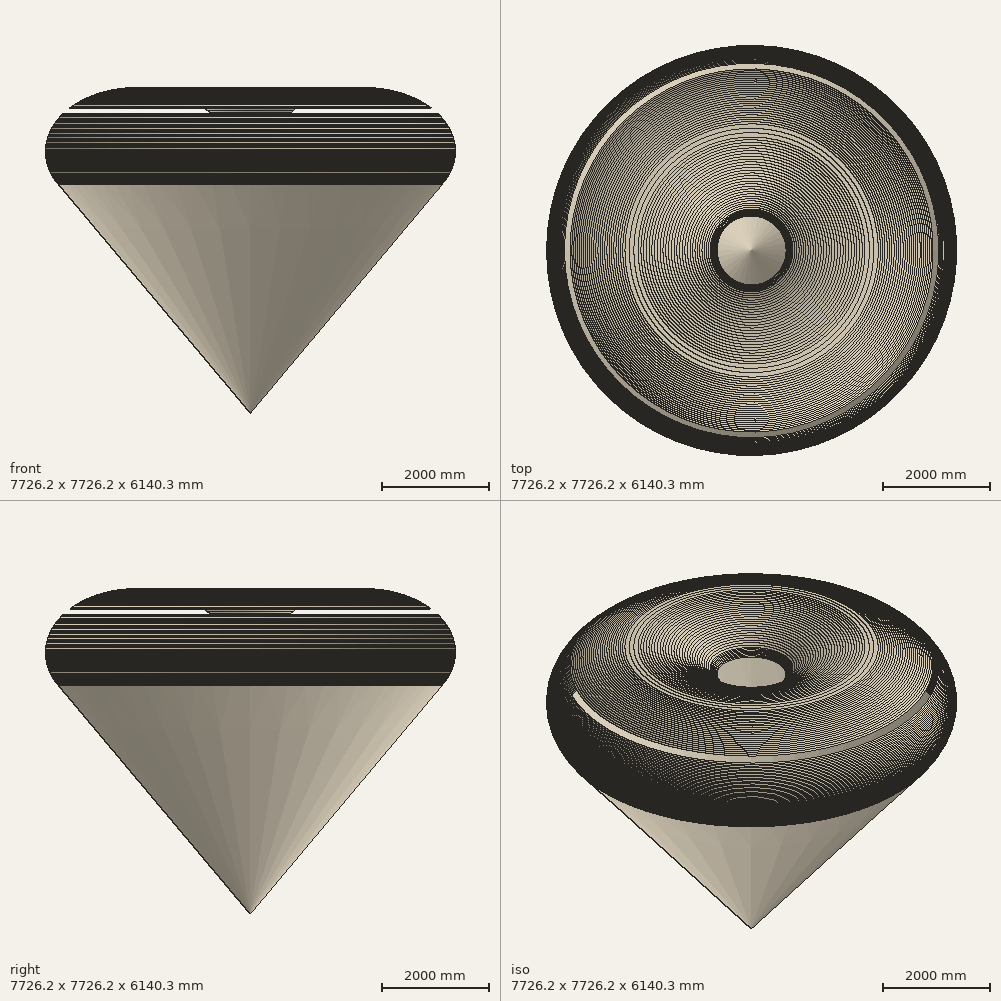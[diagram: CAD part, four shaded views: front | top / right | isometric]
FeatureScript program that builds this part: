
annotation { "Feature Type Name" : "Feature", "Feature Type Description" : "" }
export const myFeature = defineFeature(function(context is Context, id is Id, definition is map)
    precondition{}
    {
        {
            var Q0;
            Q0=qCreatedBy(makeId("Front.planeOp"),FACE);
            var sketch = newSketch(context, id + "F0", { "sketchPlane" : qUnion([Q0])});
            skCircle(sketch, "E0", {"center": v(-6064.54, 1467.13) * mm, "radius": 655.98 * mm});
            skLineSegment(sketch, "E1", {"start": v(-3070, -4796.93) * mm, "end": v(-3002.74, -4740.49) * mm});
            skLineSegment(sketch, "E2", {"start": v(-5930.64, -5948.92) * mm, "end": v(-6060.41, -6057.82) * mm});
            skLineSegment(sketch, "E3", {"start": v(-3096.96, -4796.05) * mm, "end": v(-3134.07, -4768.85) * mm});
            skLineSegment(sketch, "E4", {"start": v(-3134.07, -4768.85) * mm, "end": v(-3335.22, -4786.8) * mm});
            skLineSegment(sketch, "E5", {"start": v(-3112.53, -4828.64) * mm, "end": v(-3070, -4796.93) * mm});
            skLineSegment(sketch, "E6", {"start": v(-3066.53, -4801.07) * mm, "end": v(-3109.32, -4834.33) * mm});
            skLineSegment(sketch, "E7", {"start": v(-3109.32, -4834.33) * mm, "end": v(-3122.09, -4880.14) * mm});
            skLineSegment(sketch, "E8", {"start": v(-3074.34, -4791.79) * mm, "end": v(-3116.78, -4823.52) * mm});
            skLineSegment(sketch, "E9", {"start": v(-3116.78, -4823.52) * mm, "end": v(-3165.41, -4828.64) * mm});
            skLineSegment(sketch, "E10", {"start": v(-3112.53, -4828.64) * mm, "end": v(-3155.06, -4860.36) * mm});
            skLineSegment(sketch, "E11", {"start": v(-3070, -4796.93) * mm, "end": v(-1762.35, -4796.93) * mm});
            skLineSegment(sketch, "E12", {"start": v(-2683.52, -4505.2) * mm, "end": v(-2144.54, -4505.2) * mm});
            skLineSegment(sketch, "E13", {"start": v(-2144.54, -4505.2) * mm, "end": v(-2144.54, -4796.93) * mm});
            skLineSegment(sketch, "E14", {"start": v(-2144.54, -4796.93) * mm, "end": v(-2683.52, -4796.93) * mm});
            skLineSegment(sketch, "E15", {"start": v(-2683.52, -4796.93) * mm, "end": v(-2683.52, -4505.2) * mm});
            skLineSegment(sketch, "E16", {"start": v(-2683.52, -4651.07) * mm, "end": v(-2144.54, -4651.07) * mm});
            skLineSegment(sketch, "E17", {"start": v(-5676.95, -4745.2) * mm, "end": v(-5902.44, -4455.47) * mm});
            skLineSegment(sketch, "E18", {"start": v(-5755.47, -4796.53) * mm, "end": v(-5992.33, -4535.27) * mm});
            skLineSegment(sketch, "E19", {"start": v(-2557.41, -4806.02) * mm, "end": v(-2584.41, -4759.86) * mm});
            skLineSegment(sketch, "E20", {"start": v(-2584.41, -4759.86) * mm, "end": v(-2612.27, -4714.26) * mm});
            skLineSegment(sketch, "E21", {"start": v(-2612.27, -4714.26) * mm, "end": v(-2640.96, -4669.21) * mm});
            skLineSegment(sketch, "E22", {"start": v(-2640.96, -4669.21) * mm, "end": v(-2670.47, -4624.74) * mm});
            skLineSegment(sketch, "E23", {"start": v(-2670.47, -4624.74) * mm, "end": v(-2700.77, -4580.85) * mm});
            skLineSegment(sketch, "E24", {"start": v(-2700.77, -4580.85) * mm, "end": v(-2731.85, -4537.55) * mm});
            skLineSegment(sketch, "E25", {"start": v(-2731.85, -4537.55) * mm, "end": v(-2763.68, -4494.86) * mm});
            skLineSegment(sketch, "E26", {"start": v(-2763.68, -4494.86) * mm, "end": v(-2796.25, -4452.78) * mm});
            skLineSegment(sketch, "E27", {"start": v(-2796.25, -4452.78) * mm, "end": v(-2829.53, -4411.33) * mm});
            skLineSegment(sketch, "E28", {"start": v(-2829.53, -4411.33) * mm, "end": v(-2863.5, -4370.5) * mm});
            skLineSegment(sketch, "E29", {"start": v(-2863.5, -4370.5) * mm, "end": v(-2933.46, -4290.78) * mm});
            skLineSegment(sketch, "E30", {"start": v(-2933.46, -4290.78) * mm, "end": v(-3005.97, -4213.68) * mm});
            skLineSegment(sketch, "E31", {"start": v(-3005.97, -4213.68) * mm, "end": v(-3080.85, -4139.27) * mm});
            skLineSegment(sketch, "E32", {"start": v(-3080.85, -4139.27) * mm, "end": v(-3157.98, -4067.6) * mm});
            skLineSegment(sketch, "E33", {"start": v(-3157.98, -4067.6) * mm, "end": v(-3237.2, -3998.74) * mm});
            skLineSegment(sketch, "E34", {"start": v(-3237.2, -3998.74) * mm, "end": v(-3318.34, -3932.72) * mm});
            skLineSegment(sketch, "E35", {"start": v(-3318.34, -3932.72) * mm, "end": v(-3401.29, -3869.58) * mm});
            skLineSegment(sketch, "E36", {"start": v(-3401.29, -3869.58) * mm, "end": v(-3485.88, -3809.38) * mm});
            skLineSegment(sketch, "E37", {"start": v(-3485.88, -3809.38) * mm, "end": v(-3571.98, -3752.14) * mm});
            skLineSegment(sketch, "E38", {"start": v(-3571.98, -3752.14) * mm, "end": v(-3659.44, -3697.9) * mm});
            skLineSegment(sketch, "E39", {"start": v(-3659.44, -3697.9) * mm, "end": v(-3748.14, -3646.7) * mm});
            skLineSegment(sketch, "E40", {"start": v(-3748.14, -3646.7) * mm, "end": v(-3837.94, -3598.55) * mm});
            skLineSegment(sketch, "E41", {"start": v(-3837.94, -3598.55) * mm, "end": v(-3928.7, -3553.47) * mm});
            skLineSegment(sketch, "E42", {"start": v(-3928.7, -3553.47) * mm, "end": v(-4020.28, -3511.48) * mm});
            skLineSegment(sketch, "E43", {"start": v(-4020.28, -3511.48) * mm, "end": v(-4112.57, -3472.6) * mm});
            skLineSegment(sketch, "E44", {"start": v(-4112.57, -3472.6) * mm, "end": v(-4205.43, -3436.84) * mm});
            skLineSegment(sketch, "E45", {"start": v(-4205.43, -3436.84) * mm, "end": v(-4298.75, -3404.2) * mm});
            skLineSegment(sketch, "E46", {"start": v(-4298.75, -3404.2) * mm, "end": v(-4392.4, -3374.7) * mm});
            skLineSegment(sketch, "E47", {"start": v(-4392.4, -3374.7) * mm, "end": v(-4486.26, -3348.33) * mm});
            skLineSegment(sketch, "E48", {"start": v(-4486.26, -3348.33) * mm, "end": v(-4580.2, -3325.08) * mm});
            skLineSegment(sketch, "E49", {"start": v(-4580.2, -3325.08) * mm, "end": v(-4674.13, -3304.96) * mm});
            skLineSegment(sketch, "E50", {"start": v(-4674.13, -3304.96) * mm, "end": v(-4767.9, -3287.96) * mm});
            skLineSegment(sketch, "E51", {"start": v(-4767.9, -3287.96) * mm, "end": v(-4861.44, -3274.06) * mm});
            skLineSegment(sketch, "E52", {"start": v(-4861.44, -3274.06) * mm, "end": v(-4954.6, -3263.25) * mm});
            skLineSegment(sketch, "E53", {"start": v(-4954.6, -3263.25) * mm, "end": v(-5047.31, -3255.52) * mm});
            skLineSegment(sketch, "E54", {"start": v(-5047.31, -3255.52) * mm, "end": v(-5139.44, -3250.85) * mm});
            skLineSegment(sketch, "E55", {"start": v(-5139.44, -3250.85) * mm, "end": v(-5230.89, -3249.21) * mm});
            skLineSegment(sketch, "E56", {"start": v(-5230.89, -3249.21) * mm, "end": v(-5321.56, -3250.59) * mm});
            skLineSegment(sketch, "E57", {"start": v(-5321.56, -3250.59) * mm, "end": v(-5411.35, -3254.95) * mm});
            skLineSegment(sketch, "E58", {"start": v(-5411.35, -3254.95) * mm, "end": v(-5500.17, -3262.27) * mm});
            skLineSegment(sketch, "E59", {"start": v(-5500.17, -3262.27) * mm, "end": v(-5587.91, -3272.52) * mm});
            skLineSegment(sketch, "E60", {"start": v(-5587.91, -3272.52) * mm, "end": v(-5674.5, -3285.66) * mm});
            skLineSegment(sketch, "E61", {"start": v(-5674.5, -3285.66) * mm, "end": v(-5717.32, -3293.3) * mm});
            skLineSegment(sketch, "E62", {"start": v(-5717.32, -3293.3) * mm, "end": v(-5759.82, -3301.67) * mm});
            skLineSegment(sketch, "E63", {"start": v(-5759.82, -3301.67) * mm, "end": v(-5801.98, -3310.73) * mm});
            skLineSegment(sketch, "E64", {"start": v(-5801.98, -3310.73) * mm, "end": v(-5843.8, -3320.5) * mm});
            skLineSegment(sketch, "E65", {"start": v(-5843.8, -3320.5) * mm, "end": v(-5885.26, -3330.95) * mm});
            skLineSegment(sketch, "E66", {"start": v(-5885.26, -3330.95) * mm, "end": v(-5926.35, -3342.1) * mm});
            skLineSegment(sketch, "E67", {"start": v(-5926.35, -3342.1) * mm, "end": v(-5967.06, -3353.94) * mm});
            skLineSegment(sketch, "E68", {"start": v(-5967.06, -3353.94) * mm, "end": v(-6007.38, -3366.46) * mm});
            skLineSegment(sketch, "E69", {"start": v(-6007.38, -3366.46) * mm, "end": v(-6047.3, -3379.65) * mm});
            skLineSegment(sketch, "E70", {"start": v(-6047.3, -3379.65) * mm, "end": v(-6086.82, -3393.52) * mm});
            skLineSegment(sketch, "E71", {"start": v(-6086.82, -3393.52) * mm, "end": v(-6125.91, -3408.05) * mm});
            skLineSegment(sketch, "E72", {"start": v(-6125.91, -3408.05) * mm, "end": v(-6164.58, -3423.24) * mm});
            skLineSegment(sketch, "E73", {"start": v(-6164.58, -3423.24) * mm, "end": v(-6202.8, -3439.08) * mm});
            skLineSegment(sketch, "E74", {"start": v(-6202.8, -3439.08) * mm, "end": v(-6240.57, -3455.57) * mm});
            skLineSegment(sketch, "E75", {"start": v(-6240.57, -3455.57) * mm, "end": v(-6277.89, -3472.7) * mm});
            skLineSegment(sketch, "E76", {"start": v(-6277.89, -3472.7) * mm, "end": v(-6314.74, -3490.46) * mm});
            skLineSegment(sketch, "E77", {"start": v(-6314.74, -3490.46) * mm, "end": v(-6351.1, -3508.86) * mm});
            skLineSegment(sketch, "E78", {"start": v(-6351.1, -3508.86) * mm, "end": v(-6387, -3527.88) * mm});
            skLineSegment(sketch, "E79", {"start": v(-6387, -3527.88) * mm, "end": v(-6422.38, -3547.52) * mm});
            skLineSegment(sketch, "E80", {"start": v(-6422.38, -3547.52) * mm, "end": v(-6457.26, -3567.77) * mm});
            skLineSegment(sketch, "E81", {"start": v(-6457.26, -3567.77) * mm, "end": v(-6491.63, -3588.62) * mm});
            skLineSegment(sketch, "E82", {"start": v(-6491.63, -3588.62) * mm, "end": v(-6525.48, -3610.07) * mm});
            skLineSegment(sketch, "E83", {"start": v(-6525.48, -3610.07) * mm, "end": v(-6558.8, -3632.11) * mm});
            skLineSegment(sketch, "E84", {"start": v(-6558.8, -3632.11) * mm, "end": v(-6591.58, -3654.74) * mm});
            skLineSegment(sketch, "E85", {"start": v(-6591.58, -3654.74) * mm, "end": v(-6623.81, -3677.95) * mm});
            skLineSegment(sketch, "E86", {"start": v(-6623.81, -3677.95) * mm, "end": v(-6655.5, -3701.73) * mm});
            skLineSegment(sketch, "E87", {"start": v(-6655.5, -3701.73) * mm, "end": v(-6686.6, -3726.07) * mm});
            skLineSegment(sketch, "E88", {"start": v(-6686.6, -3726.07) * mm, "end": v(-6717.15, -3750.97) * mm});
            skLineSegment(sketch, "E89", {"start": v(-6717.15, -3750.97) * mm, "end": v(-6747.12, -3776.42) * mm});
            skLineSegment(sketch, "E90", {"start": v(-6747.12, -3776.42) * mm, "end": v(-6776.5, -3802.42) * mm});
            skLineSegment(sketch, "E91", {"start": v(-6776.5, -3802.42) * mm, "end": v(-6805.29, -3828.96) * mm});
            skLineSegment(sketch, "E92", {"start": v(-6805.29, -3828.96) * mm, "end": v(-6833.47, -3856.02) * mm});
            skLineSegment(sketch, "E93", {"start": v(-6833.47, -3856.02) * mm, "end": v(-6861.05, -3883.6) * mm});
            skLineSegment(sketch, "E94", {"start": v(-6861.05, -3883.6) * mm, "end": v(-6888.01, -3911.71) * mm});
            skLineSegment(sketch, "E95", {"start": v(-6888.01, -3911.71) * mm, "end": v(-6914.35, -3940.33) * mm});
            skLineSegment(sketch, "E96", {"start": v(-6914.35, -3940.33) * mm, "end": v(-6940.06, -3969.44) * mm});
            skLineSegment(sketch, "E97", {"start": v(-6940.06, -3969.44) * mm, "end": v(-6965.14, -3999.05) * mm});
            skLineSegment(sketch, "E98", {"start": v(-6965.14, -3999.05) * mm, "end": v(-6989.57, -4029.15) * mm});
            skLineSegment(sketch, "E99", {"start": v(-6989.57, -4029.15) * mm, "end": v(-7013.36, -4059.73) * mm});
            skLineSegment(sketch, "E100", {"start": v(-7013.36, -4059.73) * mm, "end": v(-7036.49, -4090.78) * mm});
            skLineSegment(sketch, "E101", {"start": v(-7036.49, -4090.78) * mm, "end": v(-7058.95, -4122.3) * mm});
            skLineSegment(sketch, "E102", {"start": v(-7058.95, -4122.3) * mm, "end": v(-7080.75, -4154.26) * mm});
            skLineSegment(sketch, "E103", {"start": v(-7080.75, -4154.26) * mm, "end": v(-7101.88, -4186.69) * mm});
            skLineSegment(sketch, "E104", {"start": v(-7101.88, -4186.69) * mm, "end": v(-7122.33, -4219.56) * mm});
            skLineSegment(sketch, "E105", {"start": v(-7122.33, -4219.56) * mm, "end": v(-7142.1, -4252.86) * mm});
            skLineSegment(sketch, "E106", {"start": v(-7142.1, -4252.86) * mm, "end": v(-7161.16, -4286.6) * mm});
            skLineSegment(sketch, "E107", {"start": v(-7161.16, -4286.6) * mm, "end": v(-7179.54, -4320.74) * mm});
            skLineSegment(sketch, "E108", {"start": v(-7179.54, -4320.74) * mm, "end": v(-7197.22, -4355.31) * mm});
            skLineSegment(sketch, "E109", {"start": v(-7197.22, -4355.31) * mm, "end": v(-7214.18, -4390.28) * mm});
            skLineSegment(sketch, "E110", {"start": v(-7214.18, -4390.28) * mm, "end": v(-7230.44, -4425.65) * mm});
            skLineSegment(sketch, "E111", {"start": v(-7230.44, -4425.65) * mm, "end": v(-7245.98, -4461.42) * mm});
            skLineSegment(sketch, "E112", {"start": v(-7245.98, -4461.42) * mm, "end": v(-7260.8, -4497.56) * mm});
            skLineSegment(sketch, "E113", {"start": v(-7260.8, -4497.56) * mm, "end": v(-7274.9, -4534.09) * mm});
            skLineSegment(sketch, "E114", {"start": v(-7274.9, -4534.09) * mm, "end": v(-7288.26, -4570.98) * mm});
            skLineSegment(sketch, "E115", {"start": v(-7288.26, -4570.98) * mm, "end": v(-7300.88, -4608.23) * mm});
            skLineSegment(sketch, "E116", {"start": v(-7300.88, -4608.23) * mm, "end": v(-7312.77, -4645.84) * mm});
            skLineSegment(sketch, "E117", {"start": v(-7312.77, -4645.84) * mm, "end": v(-7323.92, -4683.8) * mm});
            skLineSegment(sketch, "E118", {"start": v(-7323.92, -4683.8) * mm, "end": v(-7334.31, -4722.09) * mm});
            skLineSegment(sketch, "E119", {"start": v(-7334.31, -4722.09) * mm, "end": v(-7343.96, -4760.72) * mm});
            skLineSegment(sketch, "E120", {"start": v(-7343.96, -4760.72) * mm, "end": v(-7352.85, -4799.67) * mm});
            skLineSegment(sketch, "E121", {"start": v(-7352.85, -4799.67) * mm, "end": v(-7360.98, -4838.93) * mm});
            skLineSegment(sketch, "E122", {"start": v(-7360.98, -4838.93) * mm, "end": v(-7368.35, -4878.51) * mm});
            skLineSegment(sketch, "E123", {"start": v(-7368.35, -4878.51) * mm, "end": v(-7374.95, -4918.4) * mm});
            skLineSegment(sketch, "E124", {"start": v(-7374.95, -4918.4) * mm, "end": v(-7380.78, -4958.57) * mm});
            skLineSegment(sketch, "E125", {"start": v(-7380.78, -4958.57) * mm, "end": v(-7385.84, -4999.04) * mm});
            skLineSegment(sketch, "E126", {"start": v(-7385.84, -4999.04) * mm, "end": v(-7390.12, -5039.79) * mm});
            skLineSegment(sketch, "E127", {"start": v(-7390.12, -5039.79) * mm, "end": v(-7393.63, -5080.8) * mm});
            skLineSegment(sketch, "E128", {"start": v(-7393.63, -5080.8) * mm, "end": v(-7396.35, -5122.1) * mm});
            skLineSegment(sketch, "E129", {"start": v(-7396.35, -5122.1) * mm, "end": v(-7398.29, -5163.65) * mm});
            skLineSegment(sketch, "E130", {"start": v(-7398.29, -5163.65) * mm, "end": v(-7399.44, -5205.45) * mm});
            skLineSegment(sketch, "E131", {"start": v(-7399.44, -5205.45) * mm, "end": v(-7399.8, -5247.5) * mm});
            skLineSegment(sketch, "E132", {"start": v(-7399.8, -5247.5) * mm, "end": v(-7399.37, -5289.8) * mm});
            skLineSegment(sketch, "E133", {"start": v(-7399.37, -5289.8) * mm, "end": v(-7398.15, -5332.32) * mm});
            skLineSegment(sketch, "E134", {"start": v(-7398.15, -5332.32) * mm, "end": v(-7396.13, -5375.06) * mm});
            skLineSegment(sketch, "E135", {"start": v(-7396.13, -5375.06) * mm, "end": v(-7393.3, -5418.03) * mm});
            skLineSegment(sketch, "E136", {"start": v(-7393.3, -5418.03) * mm, "end": v(-7389.7, -5461.21) * mm});
            skLineSegment(sketch, "E137", {"start": v(-7389.7, -5461.21) * mm, "end": v(-7385.27, -5504.6) * mm});
            skLineSegment(sketch, "E138", {"start": v(-7385.27, -5504.6) * mm, "end": v(-7380.05, -5548.2) * mm});
            skLineSegment(sketch, "E139", {"start": v(-7380.05, -5548.2) * mm, "end": v(-7367.19, -5635.94) * mm});
            skLineSegment(sketch, "E140", {"start": v(-7367.19, -5635.94) * mm, "end": v(-7351.1, -5724.42) * mm});
            skLineSegment(sketch, "E141", {"start": v(-7351.1, -5724.42) * mm, "end": v(-7331.77, -5813.57) * mm});
            skLineSegment(sketch, "E142", {"start": v(-7331.77, -5813.57) * mm, "end": v(-7309.2, -5903.35) * mm});
            skLineSegment(sketch, "E143", {"start": v(-7309.2, -5903.35) * mm, "end": v(-7283.37, -5993.7) * mm});
            skLineSegment(sketch, "E144", {"start": v(-7283.37, -5993.7) * mm, "end": v(-7254.3, -6084.6) * mm});
            skLineSegment(sketch, "E145", {"start": v(-7254.3, -6084.6) * mm, "end": v(-7221.98, -6176) * mm});
            skLineSegment(sketch, "E146", {"start": v(-7221.98, -6176) * mm, "end": v(-7186.4, -6267.84) * mm});
            skLineSegment(sketch, "E147", {"start": v(-7186.4, -6267.84) * mm, "end": v(-7147.58, -6360.1) * mm});
            skLineSegment(sketch, "E148", {"start": v(-7147.58, -6360.1) * mm, "end": v(-7105.51, -6452.72) * mm});
            skLineSegment(sketch, "E149", {"start": v(-7105.51, -6452.72) * mm, "end": v(-7060.21, -6545.7) * mm});
            skLineSegment(sketch, "E150", {"start": v(-7060.21, -6545.7) * mm, "end": v(-7011.69, -6638.97) * mm});
            skLineSegment(sketch, "E151", {"start": v(-7011.69, -6638.97) * mm, "end": v(-6959.95, -6732.52) * mm});
            skLineSegment(sketch, "E152", {"start": v(-6959.95, -6732.52) * mm, "end": v(-6905, -6826.3) * mm});
            skLineSegment(sketch, "E153", {"start": v(-6905, -6826.3) * mm, "end": v(-6846.88, -6920.32) * mm});
            skLineSegment(sketch, "E154", {"start": v(-6846.88, -6920.32) * mm, "end": v(-6785.58, -7014.52) * mm});
            skLineSegment(sketch, "E155", {"start": v(-6785.58, -7014.52) * mm, "end": v(-6721.12, -7108.88) * mm});
            skLineSegment(sketch, "E156", {"start": v(-6721.12, -7108.88) * mm, "end": v(-6653.54, -7203.4) * mm});
            skLineSegment(sketch, "E157", {"start": v(-6653.54, -7203.4) * mm, "end": v(-6582.85, -7298.04) * mm});
            skLineSegment(sketch, "E158", {"start": v(-6582.85, -7298.04) * mm, "end": v(-6509.08, -7392.8) * mm});
            skLineSegment(sketch, "E159", {"start": v(-6509.08, -7392.8) * mm, "end": v(-6432.24, -7487.66) * mm});
            skLineSegment(sketch, "E160", {"start": v(-6432.24, -7487.66) * mm, "end": v(-6352.38, -7582.62) * mm});
            skLineSegment(sketch, "E161", {"start": v(-6352.38, -7582.62) * mm, "end": v(-6183.7, -7772.78) * mm});
            skLineSegment(sketch, "E162", {"start": v(-6183.7, -7772.78) * mm, "end": v(-6003.28, -7963.27) * mm});
            skLineSegment(sketch, "E163", {"start": v(-6003.28, -7963.27) * mm, "end": v(-5811.43, -8154.13) * mm});
            skLineSegment(sketch, "E164", {"start": v(-5811.43, -8154.13) * mm, "end": v(-5608.46, -8345.43) * mm});
            skLineSegment(sketch, "E165", {"start": v(-5608.46, -8345.43) * mm, "end": v(-5394.75, -8537.32) * mm});
            skLineSegment(sketch, "E166", {"start": v(-5394.75, -8537.32) * mm, "end": v(-5170.66, -8730) * mm});
            skLineSegment(sketch, "E167", {"start": v(-5170.66, -8730) * mm, "end": v(-4936.62, -8923.7) * mm});
            skLineSegment(sketch, "E168", {"start": v(-4936.62, -8923.7) * mm, "end": v(-4440.49, -9315.6) * mm});
            skLineSegment(sketch, "E169", {"start": v(-4440.49, -9315.6) * mm, "end": v(-3910.27, -9716.36) * mm});
            skLineSegment(sketch, "E170", {"start": v(-3910.27, -9716.36) * mm, "end": v(-2765.64, -10563.66) * mm});
            skLineSegment(sketch, "E171", {"start": v(-3092.98, -4789.79) * mm, "end": v(-3093.29, -4801.97) * mm});
            skLineSegment(sketch, "E172", {"start": v(-3093.29, -4801.97) * mm, "end": v(-3104.06, -4799.16) * mm});
            skLineSegment(sketch, "E173", {"start": v(-3104.06, -4799.16) * mm, "end": v(-3092.98, -4789.79) * mm});
            skCircle(sketch, "E174", {"center": v(-6064.54, 1467.13) * mm, "radius": 755.98 * mm});
            skLineSegment(sketch, "E175", {"start": v(-6318.54, 1625.88) * mm, "end": v(-5810.54, 1625.88) * mm});
            skLineSegment(sketch, "E176", {"start": v(-5810.54, 1625.88) * mm, "end": v(-5810.54, 1308.38) * mm});
            skLineSegment(sketch, "E177", {"start": v(-5810.54, 1308.38) * mm, "end": v(-6318.54, 1308.38) * mm});
            skLineSegment(sketch, "E178", {"start": v(-6318.54, 1308.38) * mm, "end": v(-6318.54, 1625.88) * mm});
            skLineSegment(sketch, "E179", {"start": v(-6318.54, 1546.5) * mm, "end": v(-5810.54, 1546.5) * mm});
            skLineSegment(sketch, "E180", {"start": v(-6318.54, 1387.75) * mm, "end": v(-5810.54, 1387.75) * mm});
            skLineSegment(sketch, "E181", {"start": v(-5310.22, 1517.13) * mm, "end": v(-6818.86, 1517.13) * mm});
            skLineSegment(sketch, "E182", {"start": v(-5310.22, 1417.13) * mm, "end": v(-6818.86, 1417.13) * mm});
            skLineSegment(sketch, "E183", {"start": v(-6022.98, -5953.64) * mm, "end": v(-2397.59, -10274.2) * mm});
            skLineSegment(sketch, "E184", {"start": v(-2397.59, -5504) * mm, "end": v(-2397.59, -10274.2) * mm});
            skLineSegment(sketch, "E185", {"start": v(-3047.01, -4730.04) * mm, "end": v(-2397.59, -5504) * mm});
            skLineSegment(sketch, "E186", {"start": v(-5818.02, -4534.01) * mm, "end": v(-5785.77, -4509.6) * mm});
            skLineSegment(sketch, "E187", {"start": v(-5785.77, -4509.6) * mm, "end": v(-5752.56, -4485.8) * mm});
            skLineSegment(sketch, "E188", {"start": v(-5752.56, -4485.8) * mm, "end": v(-5718.42, -4462.66) * mm});
            skLineSegment(sketch, "E189", {"start": v(-5718.42, -4462.66) * mm, "end": v(-5683.4, -4440.2) * mm});
            skLineSegment(sketch, "E190", {"start": v(-5683.4, -4440.2) * mm, "end": v(-5647.54, -4418.42) * mm});
            skLineSegment(sketch, "E191", {"start": v(-5647.54, -4418.42) * mm, "end": v(-5610.89, -4397.38) * mm});
            skLineSegment(sketch, "E192", {"start": v(-5610.89, -4397.38) * mm, "end": v(-5573.47, -4377.08) * mm});
            skLineSegment(sketch, "E193", {"start": v(-5573.47, -4377.08) * mm, "end": v(-5535.35, -4357.54) * mm});
            skLineSegment(sketch, "E194", {"start": v(-5535.35, -4357.54) * mm, "end": v(-5496.58, -4338.78) * mm});
            skLineSegment(sketch, "E195", {"start": v(-5496.58, -4338.78) * mm, "end": v(-5457.18, -4320.82) * mm});
            skLineSegment(sketch, "E196", {"start": v(-5457.18, -4320.82) * mm, "end": v(-5417.23, -4303.66) * mm});
            skLineSegment(sketch, "E197", {"start": v(-5417.23, -4303.66) * mm, "end": v(-5376.76, -4287.33) * mm});
            skLineSegment(sketch, "E198", {"start": v(-5376.76, -4287.33) * mm, "end": v(-5335.84, -4271.82) * mm});
            skLineSegment(sketch, "E199", {"start": v(-5335.84, -4271.82) * mm, "end": v(-5294.5, -4257.15) * mm});
            skLineSegment(sketch, "E200", {"start": v(-5294.5, -4257.15) * mm, "end": v(-5252.8, -4243.33) * mm});
            skLineSegment(sketch, "E201", {"start": v(-5252.8, -4243.33) * mm, "end": v(-5210.8, -4230.35) * mm});
            skLineSegment(sketch, "E202", {"start": v(-5210.8, -4230.35) * mm, "end": v(-5168.52, -4218.21) * mm});
            skLineSegment(sketch, "E203", {"start": v(-5168.52, -4218.21) * mm, "end": v(-5126.04, -4206.93) * mm});
            skLineSegment(sketch, "E204", {"start": v(-5126.04, -4206.93) * mm, "end": v(-5083.4, -4196.49) * mm});
            skLineSegment(sketch, "E205", {"start": v(-5083.4, -4196.49) * mm, "end": v(-5040.66, -4186.9) * mm});
            skLineSegment(sketch, "E206", {"start": v(-5040.66, -4186.9) * mm, "end": v(-4997.84, -4178.13) * mm});
            skLineSegment(sketch, "E207", {"start": v(-4997.84, -4178.13) * mm, "end": v(-4955.01, -4170.2) * mm});
            skLineSegment(sketch, "E208", {"start": v(-4955.01, -4170.2) * mm, "end": v(-4912.21, -4163.08) * mm});
            skLineSegment(sketch, "E209", {"start": v(-4912.21, -4163.08) * mm, "end": v(-4869.48, -4156.78) * mm});
            skLineSegment(sketch, "E210", {"start": v(-4869.48, -4156.78) * mm, "end": v(-4826.87, -4151.27) * mm});
            skLineSegment(sketch, "E211", {"start": v(-4826.87, -4151.27) * mm, "end": v(-4784.4, -4146.55) * mm});
            skLineSegment(sketch, "E212", {"start": v(-4784.4, -4146.55) * mm, "end": v(-4700.1, -4139.4) * mm});
            skLineSegment(sketch, "E213", {"start": v(-4700.1, -4139.4) * mm, "end": v(-4616.88, -4135.23) * mm});
            skLineSegment(sketch, "E214", {"start": v(-4616.88, -4135.23) * mm, "end": v(-4535, -4133.87) * mm});
            skLineSegment(sketch, "E215", {"start": v(-4535, -4133.87) * mm, "end": v(-4484.8, -4134.38) * mm});
            skLineSegment(sketch, "E216", {"start": v(-4484.8, -4134.38) * mm, "end": v(-4434.07, -4135.93) * mm});
            skLineSegment(sketch, "E217", {"start": v(-4434.07, -4135.93) * mm, "end": v(-4382.85, -4138.57) * mm});
            skLineSegment(sketch, "E218", {"start": v(-4382.85, -4138.57) * mm, "end": v(-4331.2, -4142.32) * mm});
            skLineSegment(sketch, "E219", {"start": v(-4331.2, -4142.32) * mm, "end": v(-4279.2, -4147.21) * mm});
            skLineSegment(sketch, "E220", {"start": v(-4279.2, -4147.21) * mm, "end": v(-4226.92, -4153.27) * mm});
            skLineSegment(sketch, "E221", {"start": v(-4226.92, -4153.27) * mm, "end": v(-4174.42, -4160.53) * mm});
            skLineSegment(sketch, "E222", {"start": v(-4174.42, -4160.53) * mm, "end": v(-4121.79, -4169) * mm});
            skLineSegment(sketch, "E223", {"start": v(-4121.79, -4169) * mm, "end": v(-4069.1, -4178.72) * mm});
            skLineSegment(sketch, "E224", {"start": v(-4069.1, -4178.72) * mm, "end": v(-4016.45, -4189.7) * mm});
            skLineSegment(sketch, "E225", {"start": v(-4016.45, -4189.7) * mm, "end": v(-3963.91, -4201.93) * mm});
            skLineSegment(sketch, "E226", {"start": v(-3963.91, -4201.93) * mm, "end": v(-3911.59, -4215.44) * mm});
            skLineSegment(sketch, "E227", {"start": v(-3911.59, -4215.44) * mm, "end": v(-3859.56, -4230.24) * mm});
            skLineSegment(sketch, "E228", {"start": v(-3859.56, -4230.24) * mm, "end": v(-3807.92, -4246.32) * mm});
            skLineSegment(sketch, "E229", {"start": v(-3807.92, -4246.32) * mm, "end": v(-3756.77, -4263.68) * mm});
            skLineSegment(sketch, "E230", {"start": v(-3756.77, -4263.68) * mm, "end": v(-3706.2, -4282.3) * mm});
            skLineSegment(sketch, "E231", {"start": v(-3706.2, -4282.3) * mm, "end": v(-3656.3, -4302.2) * mm});
            skLineSegment(sketch, "E232", {"start": v(-3656.3, -4302.2) * mm, "end": v(-3607.17, -4323.32) * mm});
            skLineSegment(sketch, "E233", {"start": v(-3607.17, -4323.32) * mm, "end": v(-3558.9, -4345.67) * mm});
            skLineSegment(sketch, "E234", {"start": v(-3558.9, -4345.67) * mm, "end": v(-3511.6, -4369.22) * mm});
            skLineSegment(sketch, "E235", {"start": v(-3511.6, -4369.22) * mm, "end": v(-3465.32, -4393.93) * mm});
            skLineSegment(sketch, "E236", {"start": v(-3465.32, -4393.93) * mm, "end": v(-3420.18, -4419.77) * mm});
            skLineSegment(sketch, "E237", {"start": v(-3420.18, -4419.77) * mm, "end": v(-3376.25, -4446.7) * mm});
            skLineSegment(sketch, "E238", {"start": v(-3376.25, -4446.7) * mm, "end": v(-3333.6, -4474.68) * mm});
            skLineSegment(sketch, "E239", {"start": v(-3333.6, -4474.68) * mm, "end": v(-3292.34, -4503.66) * mm});
            skLineSegment(sketch, "E240", {"start": v(-3292.34, -4503.66) * mm, "end": v(-3252.5, -4533.6) * mm});
            skLineSegment(sketch, "E241", {"start": v(-3252.5, -4533.6) * mm, "end": v(-3214.18, -4564.43) * mm});
            skLineSegment(sketch, "E242", {"start": v(-3214.18, -4564.43) * mm, "end": v(-3177.41, -4596.1) * mm});
            skLineSegment(sketch, "E243", {"start": v(-3177.41, -4596.1) * mm, "end": v(-3159.64, -4612.24) * mm});
            skLineSegment(sketch, "E244", {"start": v(-3159.64, -4612.24) * mm, "end": v(-3142.27, -4628.57) * mm});
            skLineSegment(sketch, "E245", {"start": v(-3142.27, -4628.57) * mm, "end": v(-3125.32, -4645.07) * mm});
            skLineSegment(sketch, "E246", {"start": v(-3125.32, -4645.07) * mm, "end": v(-3108.8, -4661.75) * mm});
            skLineSegment(sketch, "E247", {"start": v(-3108.8, -4661.75) * mm, "end": v(-3092.7, -4678.6) * mm});
            skLineSegment(sketch, "E248", {"start": v(-3092.7, -4678.6) * mm, "end": v(-3077.03, -4695.6) * mm});
            skLineSegment(sketch, "E249", {"start": v(-3077.03, -4695.6) * mm, "end": v(-3061.8, -4712.75) * mm});
            skLineSegment(sketch, "E250", {"start": v(-3061.8, -4712.75) * mm, "end": v(-3047.01, -4730.04) * mm});
            skArc(sketch, "E251", {"start": v(-5860.11, -4568.03) * mm, "mid": v(-5880.68, -4585.61) * mm, "end": v(-5900.9, -4603.6) * mm});
            skLineSegment(sketch, "E252", {"start": v(-5860.11, -4568.03) * mm, "end": v(-5818.02, -4534.01) * mm});
            skLineSegment(sketch, "E253", {"start": v(-6022.98, -5953.64) * mm, "end": v(-6038.12, -5935.22) * mm});
            skLineSegment(sketch, "E254", {"start": v(-6038.12, -5935.22) * mm, "end": v(-6052.76, -5916.67) * mm});
            skLineSegment(sketch, "E255", {"start": v(-6052.76, -5916.67) * mm, "end": v(-6066.9, -5897.99) * mm});
            skLineSegment(sketch, "E256", {"start": v(-6066.9, -5897.99) * mm, "end": v(-6080.54, -5879.19) * mm});
            skLineSegment(sketch, "E257", {"start": v(-6080.54, -5879.19) * mm, "end": v(-6093.66, -5860.27) * mm});
            skLineSegment(sketch, "E258", {"start": v(-6093.66, -5860.27) * mm, "end": v(-6106.28, -5841.26) * mm});
            skLineSegment(sketch, "E259", {"start": v(-6106.28, -5841.26) * mm, "end": v(-6118.39, -5822.16) * mm});
            skLineSegment(sketch, "E260", {"start": v(-6118.39, -5822.16) * mm, "end": v(-6129.98, -5802.98) * mm});
            skLineSegment(sketch, "E261", {"start": v(-6129.98, -5802.98) * mm, "end": v(-6141.07, -5783.73) * mm});
            skLineSegment(sketch, "E262", {"start": v(-6141.07, -5783.73) * mm, "end": v(-6151.64, -5764.42) * mm});
            skLineSegment(sketch, "E263", {"start": v(-6151.64, -5764.42) * mm, "end": v(-6161.7, -5745.05) * mm});
            skLineSegment(sketch, "E264", {"start": v(-6161.7, -5745.05) * mm, "end": v(-6171.25, -5725.64) * mm});
            skLineSegment(sketch, "E265", {"start": v(-6171.25, -5725.64) * mm, "end": v(-6180.3, -5706.2) * mm});
            skLineSegment(sketch, "E266", {"start": v(-6180.3, -5706.2) * mm, "end": v(-6188.84, -5686.74) * mm});
            skLineSegment(sketch, "E267", {"start": v(-6188.84, -5686.74) * mm, "end": v(-6196.87, -5667.26) * mm});
            skLineSegment(sketch, "E268", {"start": v(-6196.87, -5667.26) * mm, "end": v(-6204.41, -5647.78) * mm});
            skLineSegment(sketch, "E269", {"start": v(-6204.41, -5647.78) * mm, "end": v(-6211.45, -5628.3) * mm});
            skLineSegment(sketch, "E270", {"start": v(-6211.45, -5628.3) * mm, "end": v(-6218, -5608.83) * mm});
            skLineSegment(sketch, "E271", {"start": v(-6218, -5608.83) * mm, "end": v(-6224.05, -5589.38) * mm});
            skLineSegment(sketch, "E272", {"start": v(-6224.05, -5589.38) * mm, "end": v(-6229.62, -5569.96) * mm});
            skLineSegment(sketch, "E273", {"start": v(-6229.62, -5569.96) * mm, "end": v(-6234.72, -5550.57) * mm});
            skLineSegment(sketch, "E274", {"start": v(-6234.72, -5550.57) * mm, "end": v(-6239.33, -5531.23) * mm});
            skLineSegment(sketch, "E275", {"start": v(-6239.33, -5531.23) * mm, "end": v(-6243.48, -5511.94) * mm});
            skLineSegment(sketch, "E276", {"start": v(-6243.48, -5511.94) * mm, "end": v(-6247.16, -5492.71) * mm});
            skLineSegment(sketch, "E277", {"start": v(-6247.16, -5492.71) * mm, "end": v(-6250.38, -5473.55) * mm});
            skLineSegment(sketch, "E278", {"start": v(-6250.38, -5473.55) * mm, "end": v(-6253.16, -5454.46) * mm});
            skLineSegment(sketch, "E279", {"start": v(-6253.16, -5454.46) * mm, "end": v(-6255.48, -5435.45) * mm});
            skLineSegment(sketch, "E280", {"start": v(-6255.48, -5435.45) * mm, "end": v(-6257.37, -5416.53) * mm});
            skLineSegment(sketch, "E281", {"start": v(-6257.37, -5416.53) * mm, "end": v(-6258.83, -5397.7) * mm});
            skLineSegment(sketch, "E282", {"start": v(-6258.83, -5397.7) * mm, "end": v(-6259.86, -5378.98) * mm});
            skLineSegment(sketch, "E283", {"start": v(-6259.86, -5378.98) * mm, "end": v(-6260.47, -5360.35) * mm});
            skLineSegment(sketch, "E284", {"start": v(-6260.47, -5360.35) * mm, "end": v(-6260.67, -5341.84) * mm});
            skLineSegment(sketch, "E285", {"start": v(-6260.67, -5341.84) * mm, "end": v(-6260.37, -5319.19) * mm});
            skLineSegment(sketch, "E286", {"start": v(-6260.37, -5319.19) * mm, "end": v(-6259.45, -5296.37) * mm});
            skLineSegment(sketch, "E287", {"start": v(-6259.45, -5296.37) * mm, "end": v(-6257.9, -5273.4) * mm});
            skLineSegment(sketch, "E288", {"start": v(-6257.9, -5273.4) * mm, "end": v(-6255.7, -5250.29) * mm});
            skLineSegment(sketch, "E289", {"start": v(-6255.7, -5250.29) * mm, "end": v(-6252.86, -5227.04) * mm});
            skLineSegment(sketch, "E290", {"start": v(-6252.86, -5227.04) * mm, "end": v(-6249.35, -5203.68) * mm});
            skLineSegment(sketch, "E291", {"start": v(-6249.35, -5203.68) * mm, "end": v(-6245.16, -5180.2) * mm});
            skLineSegment(sketch, "E292", {"start": v(-6245.16, -5180.2) * mm, "end": v(-6240.27, -5156.65) * mm});
            skLineSegment(sketch, "E293", {"start": v(-6240.27, -5156.65) * mm, "end": v(-6234.69, -5133) * mm});
            skLineSegment(sketch, "E294", {"start": v(-6234.69, -5133) * mm, "end": v(-6228.4, -5109.3) * mm});
            skLineSegment(sketch, "E295", {"start": v(-6228.4, -5109.3) * mm, "end": v(-6221.38, -5085.53) * mm});
            skLineSegment(sketch, "E296", {"start": v(-6221.38, -5085.53) * mm, "end": v(-6213.64, -5061.73) * mm});
            skLineSegment(sketch, "E297", {"start": v(-6213.64, -5061.73) * mm, "end": v(-6205.16, -5037.91) * mm});
            skLineSegment(sketch, "E298", {"start": v(-6205.16, -5037.91) * mm, "end": v(-6195.94, -5014.08) * mm});
            skLineSegment(sketch, "E299", {"start": v(-6195.94, -5014.08) * mm, "end": v(-6185.97, -4990.27) * mm});
            skLineSegment(sketch, "E300", {"start": v(-6185.97, -4990.27) * mm, "end": v(-6175.25, -4966.48) * mm});
            skLineSegment(sketch, "E301", {"start": v(-6175.25, -4966.48) * mm, "end": v(-6163.76, -4942.73) * mm});
            skLineSegment(sketch, "E302", {"start": v(-6163.76, -4942.73) * mm, "end": v(-6151.52, -4919.05) * mm});
            skLineSegment(sketch, "E303", {"start": v(-6151.52, -4919.05) * mm, "end": v(-6138.52, -4895.44) * mm});
            skLineSegment(sketch, "E304", {"start": v(-6138.52, -4895.44) * mm, "end": v(-6124.75, -4871.93) * mm});
            skLineSegment(sketch, "E305", {"start": v(-6124.75, -4871.93) * mm, "end": v(-6110.21, -4848.53) * mm});
            skLineSegment(sketch, "E306", {"start": v(-6110.21, -4848.53) * mm, "end": v(-6094.91, -4825.25) * mm});
            skLineSegment(sketch, "E307", {"start": v(-6094.91, -4825.25) * mm, "end": v(-6078.85, -4802.13) * mm});
            skLineSegment(sketch, "E308", {"start": v(-6078.85, -4802.13) * mm, "end": v(-6062.03, -4779.17) * mm});
            skLineSegment(sketch, "E309", {"start": v(-6062.03, -4779.17) * mm, "end": v(-6044.46, -4756.4) * mm});
            skLineSegment(sketch, "E310", {"start": v(-6044.46, -4756.4) * mm, "end": v(-6026.14, -4733.82) * mm});
            skLineSegment(sketch, "E311", {"start": v(-6026.14, -4733.82) * mm, "end": v(-6007.07, -4711.47) * mm});
            skLineSegment(sketch, "E312", {"start": v(-6007.07, -4711.47) * mm, "end": v(-5987.27, -4689.35) * mm});
            skLineSegment(sketch, "E313", {"start": v(-5987.27, -4689.35) * mm, "end": v(-5966.74, -4667.49) * mm});
            skLineSegment(sketch, "E314", {"start": v(-5966.74, -4667.49) * mm, "end": v(-5945.5, -4645.9) * mm});
            skLineSegment(sketch, "E315", {"start": v(-5945.5, -4645.9) * mm, "end": v(-5923.55, -4624.6) * mm});
            skLineSegment(sketch, "E316", {"start": v(-5923.55, -4624.6) * mm, "end": v(-5900.9, -4603.6) * mm});
            skLineSegment(sketch, "E317", {"start": v(172.04, -1272.82) * mm, "end": v(73.16, -1224.9) * mm});
            skLineSegment(sketch, "E318", {"start": v(73.16, -1224.9) * mm, "end": v(70.63, -1223.72) * mm});
            skLineSegment(sketch, "E319", {"start": v(70.63, -1223.72) * mm, "end": v(-22.45, -1181.77) * mm});
            skLineSegment(sketch, "E320", {"start": v(-22.45, -1181.77) * mm, "end": v(-24.89, -1180.7) * mm});
            skLineSegment(sketch, "E321", {"start": v(-24.89, -1180.7) * mm, "end": v(-121.14, -1140.38) * mm});
            skLineSegment(sketch, "E322", {"start": v(-121.14, -1140.38) * mm, "end": v(-123.72, -1139.34) * mm});
            skLineSegment(sketch, "E323", {"start": v(-123.72, -1139.34) * mm, "end": v(-221.12, -1101.68) * mm});
            skLineSegment(sketch, "E324", {"start": v(-221.12, -1101.68) * mm, "end": v(-223.76, -1100.7) * mm});
            skLineSegment(sketch, "E325", {"start": v(-223.76, -1100.7) * mm, "end": v(-322.24, -1065.77) * mm});
            skLineSegment(sketch, "E326", {"start": v(-322.24, -1065.77) * mm, "end": v(-324.94, -1064.86) * mm});
            skLineSegment(sketch, "E327", {"start": v(-324.94, -1064.86) * mm, "end": v(-424.42, -1032.73) * mm});
            skLineSegment(sketch, "E328", {"start": v(-424.42, -1032.73) * mm, "end": v(-427.16, -1031.89) * mm});
            skLineSegment(sketch, "E329", {"start": v(-427.16, -1031.89) * mm, "end": v(-527.57, -1002.61) * mm});
            skLineSegment(sketch, "E330", {"start": v(-527.57, -1002.61) * mm, "end": v(-530.33, -1001.85) * mm});
            skLineSegment(sketch, "E331", {"start": v(-530.33, -1001.85) * mm, "end": v(-631.58, -975.46) * mm});
            skLineSegment(sketch, "E332", {"start": v(-631.58, -975.46) * mm, "end": v(-634.37, -974.77) * mm});
            skLineSegment(sketch, "E333", {"start": v(-634.37, -974.77) * mm, "end": v(-736.37, -951.3) * mm});
            skLineSegment(sketch, "E334", {"start": v(-736.37, -951.3) * mm, "end": v(-739.2, -950.69) * mm});
            skLineSegment(sketch, "E335", {"start": v(-739.2, -950.69) * mm, "end": v(-841.51, -930.23) * mm});
            skLineSegment(sketch, "E336", {"start": v(-841.51, -930.23) * mm, "end": v(-844.34, -929.7) * mm});
            skLineSegment(sketch, "E337", {"start": v(-844.34, -929.7) * mm, "end": v(-946.37, -912.33) * mm});
            skLineSegment(sketch, "E338", {"start": v(-946.37, -912.33) * mm, "end": v(-949.2, -911.9) * mm});
            skLineSegment(sketch, "E339", {"start": v(-949.2, -911.9) * mm, "end": v(-1051.7, -897.44) * mm});
            skLineSegment(sketch, "E340", {"start": v(-1051.7, -897.44) * mm, "end": v(-1054.53, -897.08) * mm});
            skLineSegment(sketch, "E341", {"start": v(-1054.53, -897.08) * mm, "end": v(-1157.42, -885.57) * mm});
            skLineSegment(sketch, "E342", {"start": v(-1157.42, -885.57) * mm, "end": v(-1160.27, -885.3) * mm});
            skLineSegment(sketch, "E343", {"start": v(-1160.27, -885.3) * mm, "end": v(-1263.46, -876.73) * mm});
            skLineSegment(sketch, "E344", {"start": v(-1263.46, -876.73) * mm, "end": v(-1266.32, -876.53) * mm});
            skLineSegment(sketch, "E345", {"start": v(-1266.32, -876.53) * mm, "end": v(-1369.71, -870.93) * mm});
            skLineSegment(sketch, "E346", {"start": v(-1369.71, -870.93) * mm, "end": v(-1372.58, -870.81) * mm});
            skLineSegment(sketch, "E347", {"start": v(-1372.58, -870.81) * mm, "end": v(-1476.1, -868.17) * mm});
            skLineSegment(sketch, "E348", {"start": v(-1476.1, -868.17) * mm, "end": v(-1478.96, -868.14) * mm});
            skLineSegment(sketch, "E349", {"start": v(-1478.96, -868.14) * mm, "end": v(-1582.51, -868.45) * mm});
            skLineSegment(sketch, "E350", {"start": v(-1582.51, -868.45) * mm, "end": v(-1585.37, -868.5) * mm});
            skLineSegment(sketch, "E351", {"start": v(-1585.37, -868.5) * mm, "end": v(-1688.88, -871.78) * mm});
            skLineSegment(sketch, "E352", {"start": v(-1688.88, -871.78) * mm, "end": v(-1691.74, -871.9) * mm});
            skLineSegment(sketch, "E353", {"start": v(-1691.74, -871.9) * mm, "end": v(-1795.1, -878.15) * mm});
            skLineSegment(sketch, "E354", {"start": v(-1795.1, -878.15) * mm, "end": v(-1797.96, -878.36) * mm});
            skLineSegment(sketch, "E355", {"start": v(-1797.96, -878.36) * mm, "end": v(-1901.09, -887.56) * mm});
            skLineSegment(sketch, "E356", {"start": v(-1901.09, -887.56) * mm, "end": v(-1903.94, -887.86) * mm});
            skLineSegment(sketch, "E357", {"start": v(-1903.94, -887.86) * mm, "end": v(-2006.75, -900) * mm});
            skLineSegment(sketch, "E358", {"start": v(-2006.75, -900) * mm, "end": v(-2009.6, -900.38) * mm});
            skLineSegment(sketch, "E359", {"start": v(-2009.6, -900.38) * mm, "end": v(-2112, -915.46) * mm});
            skLineSegment(sketch, "E360", {"start": v(-2112, -915.46) * mm, "end": v(-2114.82, -915.91) * mm});
            skLineSegment(sketch, "E361", {"start": v(-2114.82, -915.91) * mm, "end": v(-2216.74, -933.9) * mm});
            skLineSegment(sketch, "E362", {"start": v(-2216.74, -933.9) * mm, "end": v(-2219.55, -934.44) * mm});
            skLineSegment(sketch, "E363", {"start": v(-2219.55, -934.44) * mm, "end": v(-2320.89, -955.34) * mm});
            skLineSegment(sketch, "E364", {"start": v(-2320.89, -955.34) * mm, "end": v(-2323.67, -955.96) * mm});
            skLineSegment(sketch, "E365", {"start": v(-2323.67, -955.96) * mm, "end": v(-2424.35, -979.73) * mm});
            skLineSegment(sketch, "E366", {"start": v(-2424.35, -979.73) * mm, "end": v(-2427.1, -980.43) * mm});
            skLineSegment(sketch, "E367", {"start": v(-2427.1, -980.43) * mm, "end": v(-2527.03, -1007.04) * mm});
            skLineSegment(sketch, "E368", {"start": v(-2527.03, -1007.04) * mm, "end": v(-2529.76, -1007.81) * mm});
            skLineSegment(sketch, "E369", {"start": v(-2529.76, -1007.81) * mm, "end": v(-2628.85, -1037.24) * mm});
            skLineSegment(sketch, "E370", {"start": v(-2628.85, -1037.24) * mm, "end": v(-2631.55, -1038.09) * mm});
            skLineSegment(sketch, "E371", {"start": v(-2631.55, -1038.09) * mm, "end": v(-2729.73, -1070.3) * mm});
            skLineSegment(sketch, "E372", {"start": v(-2729.73, -1070.3) * mm, "end": v(-2732.38, -1071.21) * mm});
            skLineSegment(sketch, "E373", {"start": v(-2732.38, -1071.21) * mm, "end": v(-2829.56, -1106.15) * mm});
            skLineSegment(sketch, "E374", {"start": v(-2829.56, -1106.15) * mm, "end": v(-2832.17, -1107.13) * mm});
            skLineSegment(sketch, "E375", {"start": v(-2832.17, -1107.13) * mm, "end": v(-2928.28, -1144.73) * mm});
            skLineSegment(sketch, "E376", {"start": v(-2928.28, -1144.73) * mm, "end": v(-2930.83, -1145.77) * mm});
            skLineSegment(sketch, "E377", {"start": v(-2930.83, -1145.77) * mm, "end": v(-3025.82, -1185.97) * mm});
            skLineSegment(sketch, "E378", {"start": v(-3025.82, -1185.97) * mm, "end": v(-3028.28, -1187.05) * mm});
            skLineSegment(sketch, "E379", {"start": v(-3028.28, -1187.05) * mm, "end": v(-3122.08, -1229.77) * mm});
            skLineSegment(sketch, "E380", {"start": v(-3122.08, -1229.77) * mm, "end": v(-3124.44, -1230.88) * mm});
            skLineSegment(sketch, "E381", {"start": v(-3124.44, -1230.88) * mm, "end": v(-3217.03, -1275.98) * mm});
            skLineSegment(sketch, "E382", {"start": v(-3217.03, -1275.98) * mm, "end": v(-3219.25, -1277.1) * mm});
            skLineSegment(sketch, "E383", {"start": v(-3219.25, -1277.1) * mm, "end": v(-3310.63, -1324.45) * mm});
            skLineSegment(sketch, "E384", {"start": v(-3310.63, -1324.45) * mm, "end": v(-3399.12, -1370.3) * mm});
            skLineSegment(sketch, "E385", {"start": v(-3399.12, -1370.3) * mm, "end": v(-3353.56, -1458.95) * mm});
            skLineSegment(sketch, "E386", {"start": v(-3353.56, -1458.95) * mm, "end": v(-3305.7, -1552.06) * mm});
            skLineSegment(sketch, "E387", {"start": v(-3305.7, -1552.06) * mm, "end": v(-3257.82, -1644.5) * mm});
            skLineSegment(sketch, "E388", {"start": v(-3257.82, -1644.5) * mm, "end": v(-3208.64, -1738.63) * mm});
            skLineSegment(sketch, "E389", {"start": v(-3208.64, -1738.63) * mm, "end": v(-3158.2, -1834.18) * mm});
            skLineSegment(sketch, "E390", {"start": v(-3158.2, -1834.18) * mm, "end": v(-3107.77, -1928.61) * mm});
            skLineSegment(sketch, "E391", {"start": v(-3107.77, -1928.61) * mm, "end": v(-3056.52, -2023.57) * mm});
            skLineSegment(sketch, "E392", {"start": v(-3056.52, -2023.57) * mm, "end": v(-3004.73, -2118.52) * mm});
            skLineSegment(sketch, "E393", {"start": v(-3004.73, -2118.52) * mm, "end": v(-2952.67, -2213.08) * mm});
            skLineSegment(sketch, "E394", {"start": v(-2952.67, -2213.08) * mm, "end": v(-2900.58, -2306.87) * mm});
            skLineSegment(sketch, "E395", {"start": v(-2900.58, -2306.87) * mm, "end": v(-2848.75, -2399.54) * mm});
            skLineSegment(sketch, "E396", {"start": v(-2848.75, -2399.54) * mm, "end": v(-2797.42, -2490.78) * mm});
            skLineSegment(sketch, "E397", {"start": v(-2797.42, -2490.78) * mm, "end": v(-2746.84, -2580.33) * mm});
            skLineSegment(sketch, "E398", {"start": v(-2746.84, -2580.33) * mm, "end": v(-2697.22, -2668.01) * mm});
            skLineSegment(sketch, "E399", {"start": v(-2697.22, -2668.01) * mm, "end": v(-2645.62, -2758.9) * mm});
            skLineSegment(sketch, "E400", {"start": v(-2645.62, -2758.9) * mm, "end": v(-2594.67, -2848.54) * mm});
            skLineSegment(sketch, "E401", {"start": v(-2594.67, -2848.54) * mm, "end": v(-2543, -2939.38) * mm});
            skLineSegment(sketch, "E402", {"start": v(-2543, -2939.38) * mm, "end": v(-2490.75, -3031.36) * mm});
            skLineSegment(sketch, "E403", {"start": v(-2490.75, -3031.36) * mm, "end": v(-2438.23, -3124.23) * mm});
            skLineSegment(sketch, "E404", {"start": v(-2438.23, -3124.23) * mm, "end": v(-2384.58, -3219.73) * mm});
            skLineSegment(sketch, "E405", {"start": v(-2384.58, -3219.73) * mm, "end": v(-2334.09, -3310.92) * mm});
            skLineSegment(sketch, "E406", {"start": v(-2334.09, -3310.92) * mm, "end": v(-2284.32, -3402.27) * mm});
            skLineSegment(sketch, "E407", {"start": v(-2284.32, -3402.27) * mm, "end": v(-2235.5, -3493.8) * mm});
            skLineSegment(sketch, "E408", {"start": v(-2235.5, -3493.8) * mm, "end": v(-2187.87, -3585.62) * mm});
            skLineSegment(sketch, "E409", {"start": v(-2187.87, -3585.62) * mm, "end": v(-2141.7, -3677.7) * mm});
            skLineSegment(sketch, "E410", {"start": v(-2141.7, -3677.7) * mm, "end": v(-2095.46, -3774.38) * mm});
            skLineSegment(sketch, "E411", {"start": v(-2095.46, -3774.38) * mm, "end": v(-2052.24, -3869.54) * mm});
            skLineSegment(sketch, "E412", {"start": v(-2052.24, -3869.54) * mm, "end": v(-2012.32, -3962.97) * mm});
            skLineSegment(sketch, "E413", {"start": v(-2012.32, -3962.97) * mm, "end": v(-1975.75, -4054.63) * mm});
            skLineSegment(sketch, "E414", {"start": v(-1975.75, -4054.63) * mm, "end": v(-1941.88, -4145.48) * mm});
            skLineSegment(sketch, "E415", {"start": v(-1941.88, -4145.48) * mm, "end": v(-1904.17, -4246.63) * mm});
            skLineSegment(sketch, "E416", {"start": v(-1904.17, -4246.63) * mm, "end": v(-1806.2, -4201.3) * mm});
            skLineSegment(sketch, "E417", {"start": v(-1806.2, -4201.3) * mm, "end": v(-1738, -4170.35) * mm});
            skLineSegment(sketch, "E418", {"start": v(-1738, -4170.35) * mm, "end": v(-1721.87, -4163.7) * mm});
            skLineSegment(sketch, "E419", {"start": v(-1721.87, -4163.7) * mm, "end": v(-1705.87, -4157.54) * mm});
            skLineSegment(sketch, "E420", {"start": v(-1705.87, -4157.54) * mm, "end": v(-1689.93, -4151.85) * mm});
            skLineSegment(sketch, "E421", {"start": v(-1689.93, -4151.85) * mm, "end": v(-1674, -4146.64) * mm});
            skLineSegment(sketch, "E422", {"start": v(-1674, -4146.64) * mm, "end": v(-1658.06, -4141.93) * mm});
            skLineSegment(sketch, "E423", {"start": v(-1658.06, -4141.93) * mm, "end": v(-1642.09, -4137.72) * mm});
            skLineSegment(sketch, "E424", {"start": v(-1642.09, -4137.72) * mm, "end": v(-1626.07, -4134.01) * mm});
            skLineSegment(sketch, "E425", {"start": v(-1626.07, -4134.01) * mm, "end": v(-1610.01, -4130.81) * mm});
            skLineSegment(sketch, "E426", {"start": v(-1610.01, -4130.81) * mm, "end": v(-1593.91, -4128.13) * mm});
            skLineSegment(sketch, "E427", {"start": v(-1593.91, -4128.13) * mm, "end": v(-1577.77, -4125.97) * mm});
            skLineSegment(sketch, "E428", {"start": v(-1577.77, -4125.97) * mm, "end": v(-1561.59, -4124.34) * mm});
            skLineSegment(sketch, "E429", {"start": v(-1561.59, -4124.34) * mm, "end": v(-1545.38, -4123.23) * mm});
            skLineSegment(sketch, "E430", {"start": v(-1545.38, -4123.23) * mm, "end": v(-1529.16, -4122.65) * mm});
            skLineSegment(sketch, "E431", {"start": v(-1529.16, -4122.65) * mm, "end": v(-1512.92, -4122.6) * mm});
            skLineSegment(sketch, "E432", {"start": v(-1512.92, -4122.6) * mm, "end": v(-1496.7, -4123.07) * mm});
            skLineSegment(sketch, "E433", {"start": v(-1496.7, -4123.07) * mm, "end": v(-1480.49, -4124.07) * mm});
            skLineSegment(sketch, "E434", {"start": v(-1480.49, -4124.07) * mm, "end": v(-1464.3, -4125.6) * mm});
            skLineSegment(sketch, "E435", {"start": v(-1464.3, -4125.6) * mm, "end": v(-1448.16, -4127.65) * mm});
            skLineSegment(sketch, "E436", {"start": v(-1448.16, -4127.65) * mm, "end": v(-1432.06, -4130.23) * mm});
            skLineSegment(sketch, "E437", {"start": v(-1432.06, -4130.23) * mm, "end": v(-1415.98, -4133.33) * mm});
            skLineSegment(sketch, "E438", {"start": v(-1415.98, -4133.33) * mm, "end": v(-1399.78, -4136.97) * mm});
            skLineSegment(sketch, "E439", {"start": v(-1399.78, -4136.97) * mm, "end": v(-1383.6, -4141.13) * mm});
            skLineSegment(sketch, "E440", {"start": v(-1383.6, -4141.13) * mm, "end": v(-1367.46, -4145.8) * mm});
            skLineSegment(sketch, "E441", {"start": v(-1367.46, -4145.8) * mm, "end": v(-1351.33, -4150.98) * mm});
            skLineSegment(sketch, "E442", {"start": v(-1351.33, -4150.98) * mm, "end": v(-1335.2, -4156.65) * mm});
            skLineSegment(sketch, "E443", {"start": v(-1335.2, -4156.65) * mm, "end": v(-1319, -4162.82) * mm});
            skLineSegment(sketch, "E444", {"start": v(-1319, -4162.82) * mm, "end": v(-1302.69, -4169.46) * mm});
            skLineSegment(sketch, "E445", {"start": v(-1302.69, -4169.46) * mm, "end": v(-1232.6, -4201.09) * mm});
            skLineSegment(sketch, "E446", {"start": v(-1232.6, -4201.09) * mm, "end": v(-1134.64, -4246.27) * mm});
            skLineSegment(sketch, "E447", {"start": v(-1134.64, -4246.27) * mm, "end": v(-1097, -4145.17) * mm});
            skLineSegment(sketch, "E448", {"start": v(-1097, -4145.17) * mm, "end": v(-1063.18, -4054.3) * mm});
            skLineSegment(sketch, "E449", {"start": v(-1063.18, -4054.3) * mm, "end": v(-1026.66, -3962.61) * mm});
            skLineSegment(sketch, "E450", {"start": v(-1026.66, -3962.61) * mm, "end": v(-986.8, -3869.17) * mm});
            skLineSegment(sketch, "E451", {"start": v(-986.8, -3869.17) * mm, "end": v(-943.65, -3773.99) * mm});
            skLineSegment(sketch, "E452", {"start": v(-943.65, -3773.99) * mm, "end": v(-897.5, -3677.3) * mm});
            skLineSegment(sketch, "E453", {"start": v(-897.5, -3677.3) * mm, "end": v(-851.4, -3585.2) * mm});
            skLineSegment(sketch, "E454", {"start": v(-851.4, -3585.2) * mm, "end": v(-803.82, -3493.36) * mm});
            skLineSegment(sketch, "E455", {"start": v(-803.82, -3493.36) * mm, "end": v(-755.07, -3401.8) * mm});
            skLineSegment(sketch, "E456", {"start": v(-755.07, -3401.8) * mm, "end": v(-705.37, -3310.43) * mm});
            skLineSegment(sketch, "E457", {"start": v(-705.37, -3310.43) * mm, "end": v(-654.94, -3219.21) * mm});
            skLineSegment(sketch, "E458", {"start": v(-654.94, -3219.21) * mm, "end": v(-601.36, -3123.68) * mm});
            skLineSegment(sketch, "E459", {"start": v(-601.36, -3123.68) * mm, "end": v(-548.9, -3030.79) * mm});
            skLineSegment(sketch, "E460", {"start": v(-548.9, -3030.79) * mm, "end": v(-496.7, -2938.77) * mm});
            skLineSegment(sketch, "E461", {"start": v(-496.7, -2938.77) * mm, "end": v(-445.1, -2847.9) * mm});
            skLineSegment(sketch, "E462", {"start": v(-445.1, -2847.9) * mm, "end": v(-394.2, -2758.24) * mm});
            skLineSegment(sketch, "E463", {"start": v(-394.2, -2758.24) * mm, "end": v(-342.66, -2667.31) * mm});
            skLineSegment(sketch, "E464", {"start": v(-342.66, -2667.31) * mm, "end": v(-293.1, -2579.6) * mm});
            skLineSegment(sketch, "E465", {"start": v(-293.1, -2579.6) * mm, "end": v(-242.57, -2490.03) * mm});
            skLineSegment(sketch, "E466", {"start": v(-242.57, -2490.03) * mm, "end": v(-191.3, -2398.75) * mm});
            skLineSegment(sketch, "E467", {"start": v(-191.3, -2398.75) * mm, "end": v(-139.51, -2306.05) * mm});
            skLineSegment(sketch, "E468", {"start": v(-139.51, -2306.05) * mm, "end": v(-87.48, -2212.23) * mm});
            skLineSegment(sketch, "E469", {"start": v(-87.48, -2212.23) * mm, "end": v(-35.47, -2117.65) * mm});
            skLineSegment(sketch, "E470", {"start": v(-35.47, -2117.65) * mm, "end": v(16.26, -2022.66) * mm});
            skLineSegment(sketch, "E471", {"start": v(16.26, -2022.66) * mm, "end": v(67.46, -1927.68) * mm});
            skLineSegment(sketch, "E472", {"start": v(67.46, -1927.68) * mm, "end": v(117.82, -1833.22) * mm});
            skLineSegment(sketch, "E473", {"start": v(117.82, -1833.22) * mm, "end": v(168.2, -1737.63) * mm});
            skLineSegment(sketch, "E474", {"start": v(168.2, -1737.63) * mm, "end": v(217.32, -1643.48) * mm});
            skLineSegment(sketch, "E475", {"start": v(217.32, -1643.48) * mm, "end": v(265.14, -1550.99) * mm});
            skLineSegment(sketch, "E476", {"start": v(265.14, -1550.99) * mm, "end": v(312.92, -1457.84) * mm});
            skLineSegment(sketch, "E477", {"start": v(312.92, -1457.84) * mm, "end": v(358.43, -1369.15) * mm});
            skLineSegment(sketch, "E478", {"start": v(358.43, -1369.15) * mm, "end": v(269.88, -1323.37) * mm});
            skLineSegment(sketch, "E479", {"start": v(269.88, -1323.37) * mm, "end": v(174.36, -1273.98) * mm});
            skLineSegment(sketch, "E480", {"start": v(174.36, -1273.98) * mm, "end": v(172.04, -1272.82) * mm});
            skLineSegment(sketch, "E481", {"start": v(341.38, 392.49) * mm, "end": v(352.32, 467.95) * mm});
            skLineSegment(sketch, "E482", {"start": v(352.32, 467.95) * mm, "end": v(362.92, 542) * mm});
            skLineSegment(sketch, "E483", {"start": v(362.92, 542) * mm, "end": v(372.88, 614.55) * mm});
            skLineSegment(sketch, "E484", {"start": v(372.88, 614.55) * mm, "end": v(382.74, 689.93) * mm});
            skLineSegment(sketch, "E485", {"start": v(382.74, 689.93) * mm, "end": v(391.85, 765.83) * mm});
            skLineSegment(sketch, "E486", {"start": v(391.85, 765.83) * mm, "end": v(399.97, 842.14) * mm});
            skLineSegment(sketch, "E487", {"start": v(399.97, 842.14) * mm, "end": v(406.9, 918.65) * mm});
            skLineSegment(sketch, "E488", {"start": v(406.9, 918.65) * mm, "end": v(412.68, 996.31) * mm});
            skLineSegment(sketch, "E489", {"start": v(412.68, 996.31) * mm, "end": v(412.8, 998.12) * mm});
            skLineSegment(sketch, "E490", {"start": v(412.8, 998.12) * mm, "end": v(417.04, 1073.76) * mm});
            skLineSegment(sketch, "E491", {"start": v(417.04, 1073.76) * mm, "end": v(417.12, 1075.6) * mm});
            skLineSegment(sketch, "E492", {"start": v(417.12, 1075.6) * mm, "end": v(419.94, 1150.55) * mm});
            skLineSegment(sketch, "E493", {"start": v(419.94, 1150.55) * mm, "end": v(420, 1152.37) * mm});
            skLineSegment(sketch, "E494", {"start": v(420, 1152.37) * mm, "end": v(421.41, 1225.7) * mm});
            skLineSegment(sketch, "E495", {"start": v(421.41, 1225.7) * mm, "end": v(421.43, 1227.5) * mm});
            skLineSegment(sketch, "E496", {"start": v(421.43, 1227.5) * mm, "end": v(421.53, 1302.11) * mm});
            skLineSegment(sketch, "E497", {"start": v(421.53, 1302.11) * mm, "end": v(421.52, 1303.88) * mm});
            skLineSegment(sketch, "E498", {"start": v(421.52, 1303.88) * mm, "end": v(420.24, 1381.42) * mm});
            skLineSegment(sketch, "E499", {"start": v(420.24, 1381.42) * mm, "end": v(417.58, 1461.65) * mm});
            skLineSegment(sketch, "E500", {"start": v(417.58, 1461.65) * mm, "end": v(414.26, 1538.05) * mm});
            skLineSegment(sketch, "E501", {"start": v(414.26, 1538.05) * mm, "end": v(410.26, 1613.83) * mm});
            skLineSegment(sketch, "E502", {"start": v(410.26, 1613.83) * mm, "end": v(406.02, 1687.52) * mm});
            skLineSegment(sketch, "E503", {"start": v(406.02, 1687.52) * mm, "end": v(401.46, 1762.7) * mm});
            skLineSegment(sketch, "E504", {"start": v(401.46, 1762.7) * mm, "end": v(397.1, 1837.77) * mm});
            skLineSegment(sketch, "E505", {"start": v(397.1, 1837.77) * mm, "end": v(391.7, 1930.84) * mm});
            skLineSegment(sketch, "E506", {"start": v(391.7, 1930.84) * mm, "end": v(298.48, 1931.97) * mm});
            skLineSegment(sketch, "E507", {"start": v(298.48, 1931.97) * mm, "end": v(223.15, 1932.87) * mm});
            skLineSegment(sketch, "E508", {"start": v(223.15, 1932.87) * mm, "end": v(148.05, 1934.67) * mm});
            skLineSegment(sketch, "E509", {"start": v(148.05, 1934.67) * mm, "end": v(72.44, 1937.1) * mm});
            skLineSegment(sketch, "E510", {"start": v(72.44, 1937.1) * mm, "end": v(-1.26, 1939.7) * mm});
            skLineSegment(sketch, "E511", {"start": v(-1.26, 1939.7) * mm, "end": v(-75.19, 1942.56) * mm});
            skLineSegment(sketch, "E512", {"start": v(-75.19, 1942.56) * mm, "end": v(-149.47, 1945.58) * mm});
            skLineSegment(sketch, "E513", {"start": v(-149.47, 1945.58) * mm, "end": v(-223.98, 1948.62) * mm});
            skLineSegment(sketch, "E514", {"start": v(-223.98, 1948.62) * mm, "end": v(-298.72, 1951.62) * mm});
            skLineSegment(sketch, "E515", {"start": v(-298.72, 1951.62) * mm, "end": v(-373.63, 1954.55) * mm});
            skLineSegment(sketch, "E516", {"start": v(-373.63, 1954.55) * mm, "end": v(-448.7, 1957.35) * mm});
            skLineSegment(sketch, "E517", {"start": v(-448.7, 1957.35) * mm, "end": v(-523.94, 1959.96) * mm});
            skLineSegment(sketch, "E518", {"start": v(-523.94, 1959.96) * mm, "end": v(-599.21, 1962.38) * mm});
            skLineSegment(sketch, "E519", {"start": v(-599.21, 1962.38) * mm, "end": v(-674.55, 1964.63) * mm});
            skLineSegment(sketch, "E520", {"start": v(-674.55, 1964.63) * mm, "end": v(-749.96, 1966.73) * mm});
            skLineSegment(sketch, "E521", {"start": v(-749.96, 1966.73) * mm, "end": v(-825.42, 1968.66) * mm});
            skLineSegment(sketch, "E522", {"start": v(-825.42, 1968.66) * mm, "end": v(-900.6, 1970.4) * mm});
            skLineSegment(sketch, "E523", {"start": v(-900.6, 1970.4) * mm, "end": v(-975.25, 1971.95) * mm});
            skLineSegment(sketch, "E524", {"start": v(-975.25, 1971.95) * mm, "end": v(-1049.96, 1973.34) * mm});
            skLineSegment(sketch, "E525", {"start": v(-1049.96, 1973.34) * mm, "end": v(-1124.69, 1974.54) * mm});
            skLineSegment(sketch, "E526", {"start": v(-1124.69, 1974.54) * mm, "end": v(-1199.41, 1975.57) * mm});
            skLineSegment(sketch, "E527", {"start": v(-1199.41, 1975.57) * mm, "end": v(-1274.18, 1976.44) * mm});
            skLineSegment(sketch, "E528", {"start": v(-1274.18, 1976.44) * mm, "end": v(-1348.96, 1977.12) * mm});
            skLineSegment(sketch, "E529", {"start": v(-1348.96, 1977.12) * mm, "end": v(-1423.73, 1977.63) * mm});
            skLineSegment(sketch, "E530", {"start": v(-1423.73, 1977.63) * mm, "end": v(-1498.55, 1977.97) * mm});
            skLineSegment(sketch, "E531", {"start": v(-1498.55, 1977.97) * mm, "end": v(-1573.34, 1978.11) * mm});
            skLineSegment(sketch, "E532", {"start": v(-1573.34, 1978.11) * mm, "end": v(-1648.12, 1978.1) * mm});
            skLineSegment(sketch, "E533", {"start": v(-1648.12, 1978.1) * mm, "end": v(-1722.93, 1977.94) * mm});
            skLineSegment(sketch, "E534", {"start": v(-1722.93, 1977.94) * mm, "end": v(-1797.73, 1977.57) * mm});
            skLineSegment(sketch, "E535", {"start": v(-1797.73, 1977.57) * mm, "end": v(-1872.52, 1977.03) * mm});
            skLineSegment(sketch, "E536", {"start": v(-1872.52, 1977.03) * mm, "end": v(-1947.31, 1976.32) * mm});
            skLineSegment(sketch, "E537", {"start": v(-1947.31, 1976.32) * mm, "end": v(-2022.07, 1975.42) * mm});
            skLineSegment(sketch, "E538", {"start": v(-2022.07, 1975.42) * mm, "end": v(-2096.82, 1974.36) * mm});
            skLineSegment(sketch, "E539", {"start": v(-2096.82, 1974.36) * mm, "end": v(-2171.56, 1973.11) * mm});
            skLineSegment(sketch, "E540", {"start": v(-2171.56, 1973.11) * mm, "end": v(-2246.26, 1971.67) * mm});
            skLineSegment(sketch, "E541", {"start": v(-2246.26, 1971.67) * mm, "end": v(-2320.93, 1970.07) * mm});
            skLineSegment(sketch, "E542", {"start": v(-2320.93, 1970.07) * mm, "end": v(-2395.54, 1968.3) * mm});
            skLineSegment(sketch, "E543", {"start": v(-2395.54, 1968.3) * mm, "end": v(-2470.1, 1966.35) * mm});
            skLineSegment(sketch, "E544", {"start": v(-2470.1, 1966.35) * mm, "end": v(-2544.62, 1964.24) * mm});
            skLineSegment(sketch, "E545", {"start": v(-2544.62, 1964.24) * mm, "end": v(-2619.05, 1961.98) * mm});
            skLineSegment(sketch, "E546", {"start": v(-2619.05, 1961.98) * mm, "end": v(-2693.45, 1959.56) * mm});
            skLineSegment(sketch, "E547", {"start": v(-2693.45, 1959.56) * mm, "end": v(-2767.77, 1956.95) * mm});
            skLineSegment(sketch, "E548", {"start": v(-2767.77, 1956.95) * mm, "end": v(-2841.97, 1954.16) * mm});
            skLineSegment(sketch, "E549", {"start": v(-2841.97, 1954.16) * mm, "end": v(-2915.98, 1951.25) * mm});
            skLineSegment(sketch, "E550", {"start": v(-2915.98, 1951.25) * mm, "end": v(-2989.81, 1948.27) * mm});
            skLineSegment(sketch, "E551", {"start": v(-2989.81, 1948.27) * mm, "end": v(-3063.44, 1945.25) * mm});
            skLineSegment(sketch, "E552", {"start": v(-3063.44, 1945.25) * mm, "end": v(-3136.82, 1942.27) * mm});
            skLineSegment(sketch, "E553", {"start": v(-3136.82, 1942.27) * mm, "end": v(-3209.86, 1939.45) * mm});
            skLineSegment(sketch, "E554", {"start": v(-3209.86, 1939.45) * mm, "end": v(-3282.57, 1936.9) * mm});
            skLineSegment(sketch, "E555", {"start": v(-3282.57, 1936.9) * mm, "end": v(-3354.9, 1934.75) * mm});
            skLineSegment(sketch, "E556", {"start": v(-3354.9, 1934.75) * mm, "end": v(-3426.71, 1933.22) * mm});
            skLineSegment(sketch, "E557", {"start": v(-3426.71, 1933.22) * mm, "end": v(-3498.78, 1932.52) * mm});
            skLineSegment(sketch, "E558", {"start": v(-3498.78, 1932.52) * mm, "end": v(-3592.24, 1931.62) * mm});
            skLineSegment(sketch, "E559", {"start": v(-3592.24, 1931.62) * mm, "end": v(-3597.65, 1838.32) * mm});
            skLineSegment(sketch, "E560", {"start": v(-3597.65, 1838.32) * mm, "end": v(-3602, 1763.26) * mm});
            skLineSegment(sketch, "E561", {"start": v(-3602, 1763.26) * mm, "end": v(-3606.55, 1688.05) * mm});
            skLineSegment(sketch, "E562", {"start": v(-3606.55, 1688.05) * mm, "end": v(-3610.78, 1614.35) * mm});
            skLineSegment(sketch, "E563", {"start": v(-3610.78, 1614.35) * mm, "end": v(-3614.77, 1538.57) * mm});
            skLineSegment(sketch, "E564", {"start": v(-3614.77, 1538.57) * mm, "end": v(-3618.08, 1462.17) * mm});
            skLineSegment(sketch, "E565", {"start": v(-3618.08, 1462.17) * mm, "end": v(-3620.74, 1381.92) * mm});
            skLineSegment(sketch, "E566", {"start": v(-3620.74, 1381.92) * mm, "end": v(-3622.02, 1304.37) * mm});
            skLineSegment(sketch, "E567", {"start": v(-3622.02, 1304.37) * mm, "end": v(-3622.03, 1302.6) * mm});
            skLineSegment(sketch, "E568", {"start": v(-3622.03, 1302.6) * mm, "end": v(-3621.93, 1227.98) * mm});
            skLineSegment(sketch, "E569", {"start": v(-3621.93, 1227.98) * mm, "end": v(-3621.91, 1226.19) * mm});
            skLineSegment(sketch, "E570", {"start": v(-3621.91, 1226.19) * mm, "end": v(-3620.5, 1152.83) * mm});
            skLineSegment(sketch, "E571", {"start": v(-3620.5, 1152.83) * mm, "end": v(-3620.45, 1151.02) * mm});
            skLineSegment(sketch, "E572", {"start": v(-3620.45, 1151.02) * mm, "end": v(-3617.65, 1076.05) * mm});
            skLineSegment(sketch, "E573", {"start": v(-3617.65, 1076.05) * mm, "end": v(-3617.56, 1074.22) * mm});
            skLineSegment(sketch, "E574", {"start": v(-3617.56, 1074.22) * mm, "end": v(-3613.34, 998.56) * mm});
            skLineSegment(sketch, "E575", {"start": v(-3613.34, 998.56) * mm, "end": v(-3613.23, 996.76) * mm});
            skLineSegment(sketch, "E576", {"start": v(-3613.23, 996.76) * mm, "end": v(-3607.48, 919.07) * mm});
            skLineSegment(sketch, "E577", {"start": v(-3607.48, 919.07) * mm, "end": v(-3600.57, 842.55) * mm});
            skLineSegment(sketch, "E578", {"start": v(-3600.57, 842.55) * mm, "end": v(-3592.49, 766.23) * mm});
            skLineSegment(sketch, "E579", {"start": v(-3592.49, 766.23) * mm, "end": v(-3583.42, 690.31) * mm});
            skLineSegment(sketch, "E580", {"start": v(-3583.42, 690.31) * mm, "end": v(-3573.6, 614.93) * mm});
            skLineSegment(sketch, "E581", {"start": v(-3573.6, 614.93) * mm, "end": v(-3563.7, 542.38) * mm});
            skLineSegment(sketch, "E582", {"start": v(-3563.7, 542.38) * mm, "end": v(-3553.12, 468.3) * mm});
            skLineSegment(sketch, "E583", {"start": v(-3553.12, 468.3) * mm, "end": v(-3542.22, 392.8) * mm});
            skLineSegment(sketch, "E584", {"start": v(-3542.22, 392.8) * mm, "end": v(-3531.15, 315.66) * mm});
            skLineSegment(sketch, "E585", {"start": v(-3531.15, 315.66) * mm, "end": v(-3517.8, 222.63) * mm});
            skLineSegment(sketch, "E586", {"start": v(-3517.8, 222.63) * mm, "end": v(-3424.13, 230.18) * mm});
            skLineSegment(sketch, "E587", {"start": v(-3424.13, 230.18) * mm, "end": v(-3354.92, 235.77) * mm});
            skLineSegment(sketch, "E588", {"start": v(-3354.92, 235.77) * mm, "end": v(-3286.1, 240.26) * mm});
            skLineSegment(sketch, "E589", {"start": v(-3286.1, 240.26) * mm, "end": v(-3216.81, 243.94) * mm});
            skLineSegment(sketch, "E590", {"start": v(-3216.81, 243.94) * mm, "end": v(-3147.13, 246.94) * mm});
            skLineSegment(sketch, "E591", {"start": v(-3147.13, 246.94) * mm, "end": v(-3077.11, 249.37) * mm});
            skLineSegment(sketch, "E592", {"start": v(-3077.11, 249.37) * mm, "end": v(-3006.77, 251.37) * mm});
            skLineSegment(sketch, "E593", {"start": v(-3006.77, 251.37) * mm, "end": v(-2936.15, 253.02) * mm});
            skLineSegment(sketch, "E594", {"start": v(-2936.15, 253.02) * mm, "end": v(-2865.3, 254.4) * mm});
            skLineSegment(sketch, "E595", {"start": v(-2865.3, 254.4) * mm, "end": v(-2794.27, 255.58) * mm});
            skLineSegment(sketch, "E596", {"start": v(-2794.27, 255.58) * mm, "end": v(-2723.06, 256.59) * mm});
            skLineSegment(sketch, "E597", {"start": v(-2723.06, 256.59) * mm, "end": v(-2651.7, 257.47) * mm});
            skLineSegment(sketch, "E598", {"start": v(-2651.7, 257.47) * mm, "end": v(-2580.27, 258.26) * mm});
            skLineSegment(sketch, "E599", {"start": v(-2580.27, 258.26) * mm, "end": v(-2508.76, 258.94) * mm});
            skLineSegment(sketch, "E600", {"start": v(-2508.76, 258.94) * mm, "end": v(-2437.16, 259.52) * mm});
            skLineSegment(sketch, "E601", {"start": v(-2437.16, 259.52) * mm, "end": v(-2365.48, 260.02) * mm});
            skLineSegment(sketch, "E602", {"start": v(-2365.48, 260.02) * mm, "end": v(-2293.75, 260.46) * mm});
            skLineSegment(sketch, "E603", {"start": v(-2293.75, 260.46) * mm, "end": v(-2222, 260.83) * mm});
            skLineSegment(sketch, "E604", {"start": v(-2222, 260.83) * mm, "end": v(-2150.2, 261.1) * mm});
            skLineSegment(sketch, "E605", {"start": v(-2150.2, 261.1) * mm, "end": v(-2078.35, 261.31) * mm});
            skLineSegment(sketch, "E606", {"start": v(-2078.35, 261.31) * mm, "end": v(-2006.45, 261.48) * mm});
            skLineSegment(sketch, "E607", {"start": v(-2006.45, 261.48) * mm, "end": v(-1934.52, 261.6) * mm});
            skLineSegment(sketch, "E608", {"start": v(-1934.52, 261.6) * mm, "end": v(-1862.54, 261.68) * mm});
            skLineSegment(sketch, "E609", {"start": v(-1862.54, 261.68) * mm, "end": v(-1790.54, 261.75) * mm});
            skLineSegment(sketch, "E610", {"start": v(-1790.54, 261.75) * mm, "end": v(-1718.55, 261.8) * mm});
            skLineSegment(sketch, "E611", {"start": v(-1718.55, 261.8) * mm, "end": v(-1646.55, 261.81) * mm});
            skLineSegment(sketch, "E612", {"start": v(-1646.55, 261.81) * mm, "end": v(-1574.52, 261.8) * mm});
            skLineSegment(sketch, "E613", {"start": v(-1574.52, 261.8) * mm, "end": v(-1502.5, 261.8) * mm});
            skLineSegment(sketch, "E614", {"start": v(-1502.5, 261.8) * mm, "end": v(-1430.52, 261.75) * mm});
            skLineSegment(sketch, "E615", {"start": v(-1430.52, 261.75) * mm, "end": v(-1358.53, 261.68) * mm});
            skLineSegment(sketch, "E616", {"start": v(-1358.53, 261.68) * mm, "end": v(-1286.54, 261.59) * mm});
            skLineSegment(sketch, "E617", {"start": v(-1286.54, 261.59) * mm, "end": v(-1214.61, 261.48) * mm});
            skLineSegment(sketch, "E618", {"start": v(-1214.61, 261.48) * mm, "end": v(-1142.72, 261.3) * mm});
            skLineSegment(sketch, "E619", {"start": v(-1142.72, 261.3) * mm, "end": v(-1070.86, 261.08) * mm});
            skLineSegment(sketch, "E620", {"start": v(-1070.86, 261.08) * mm, "end": v(-999.06, 260.8) * mm});
            skLineSegment(sketch, "E621", {"start": v(-999.06, 260.8) * mm, "end": v(-927.31, 260.44) * mm});
            skLineSegment(sketch, "E622", {"start": v(-927.31, 260.44) * mm, "end": v(-855.05, 259.98) * mm});
            skLineSegment(sketch, "E623", {"start": v(-855.05, 259.98) * mm, "end": v(-782.52, 259.47) * mm});
            skLineSegment(sketch, "E624", {"start": v(-782.52, 259.47) * mm, "end": v(-710.04, 258.88) * mm});
            skLineSegment(sketch, "E625", {"start": v(-710.04, 258.88) * mm, "end": v(-637.67, 258.2) * mm});
            skLineSegment(sketch, "E626", {"start": v(-637.67, 258.2) * mm, "end": v(-565.37, 257.4) * mm});
            skLineSegment(sketch, "E627", {"start": v(-565.37, 257.4) * mm, "end": v(-493.16, 256.51) * mm});
            skLineSegment(sketch, "E628", {"start": v(-493.16, 256.51) * mm, "end": v(-421.09, 255.5) * mm});
            skLineSegment(sketch, "E629", {"start": v(-421.09, 255.5) * mm, "end": v(-349.19, 254.32) * mm});
            skLineSegment(sketch, "E630", {"start": v(-349.19, 254.32) * mm, "end": v(-277.49, 252.94) * mm});
            skLineSegment(sketch, "E631", {"start": v(-277.49, 252.94) * mm, "end": v(-206, 251.28) * mm});
            skLineSegment(sketch, "E632", {"start": v(-206, 251.28) * mm, "end": v(-134.8, 249.28) * mm});
            skLineSegment(sketch, "E633", {"start": v(-134.8, 249.28) * mm, "end": v(-63.91, 246.84) * mm});
            skLineSegment(sketch, "E634", {"start": v(-63.91, 246.84) * mm, "end": v(6.7, 243.84) * mm});
            skLineSegment(sketch, "E635", {"start": v(6.7, 243.84) * mm, "end": v(79.14, 240.15) * mm});
            skLineSegment(sketch, "E636", {"start": v(79.14, 240.15) * mm, "end": v(151.1, 235.6) * mm});
            skLineSegment(sketch, "E637", {"start": v(151.1, 235.6) * mm, "end": v(223.45, 229.88) * mm});
            skLineSegment(sketch, "E638", {"start": v(223.45, 229.88) * mm, "end": v(316.95, 222.5) * mm});
            skLineSegment(sketch, "E639", {"start": v(316.95, 222.5) * mm, "end": v(330.3, 315.35) * mm});
            skLineSegment(sketch, "E640", {"start": v(330.3, 315.35) * mm, "end": v(341.38, 392.49) * mm});
            skLineSegment(sketch, "E641", {"start": v(169.84, -224.79) * mm, "end": v(138.59, -221.15) * mm});
            skLineSegment(sketch, "E642", {"start": v(138.59, -221.15) * mm, "end": v(107.3, -217.75) * mm});
            skLineSegment(sketch, "E643", {"start": v(107.3, -217.75) * mm, "end": v(76, -214.58) * mm});
            skLineSegment(sketch, "E644", {"start": v(76, -214.58) * mm, "end": v(44.72, -211.65) * mm});
            skLineSegment(sketch, "E645", {"start": v(44.72, -211.65) * mm, "end": v(13.44, -208.94) * mm});
            skLineSegment(sketch, "E646", {"start": v(13.44, -208.94) * mm, "end": v(-17.8, -206.45) * mm});
            skLineSegment(sketch, "E647", {"start": v(-17.8, -206.45) * mm, "end": v(-48.25, -204.2) * mm});
            skLineSegment(sketch, "E648", {"start": v(-48.25, -204.2) * mm, "end": v(-78.48, -202.17) * mm});
            skLineSegment(sketch, "E649", {"start": v(-78.48, -202.17) * mm, "end": v(-108.68, -200.3) * mm});
            skLineSegment(sketch, "E650", {"start": v(-108.68, -200.3) * mm, "end": v(-138.87, -198.62) * mm});
            skLineSegment(sketch, "E651", {"start": v(-138.87, -198.62) * mm, "end": v(-169.05, -197.1) * mm});
            skLineSegment(sketch, "E652", {"start": v(-169.05, -197.1) * mm, "end": v(-199.2, -195.74) * mm});
            skLineSegment(sketch, "E653", {"start": v(-199.2, -195.74) * mm, "end": v(-229.32, -194.54) * mm});
            skLineSegment(sketch, "E654", {"start": v(-229.32, -194.54) * mm, "end": v(-259.4, -193.48) * mm});
            skLineSegment(sketch, "E655", {"start": v(-259.4, -193.48) * mm, "end": v(-289.47, -192.56) * mm});
            skLineSegment(sketch, "E656", {"start": v(-289.47, -192.56) * mm, "end": v(-319.5, -191.77) * mm});
            skLineSegment(sketch, "E657", {"start": v(-319.5, -191.77) * mm, "end": v(-349.48, -191.11) * mm});
            skLineSegment(sketch, "E658", {"start": v(-349.48, -191.11) * mm, "end": v(-379.42, -190.56) * mm});
            skLineSegment(sketch, "E659", {"start": v(-379.42, -190.56) * mm, "end": v(-409.32, -190.11) * mm});
            skLineSegment(sketch, "E660", {"start": v(-409.32, -190.11) * mm, "end": v(-439.2, -189.76) * mm});
            skLineSegment(sketch, "E661", {"start": v(-439.2, -189.76) * mm, "end": v(-469.03, -189.5) * mm});
            skLineSegment(sketch, "E662", {"start": v(-469.03, -189.5) * mm, "end": v(-498.83, -189.31) * mm});
            skLineSegment(sketch, "E663", {"start": v(-498.83, -189.31) * mm, "end": v(-528.6, -189.2) * mm});
            skLineSegment(sketch, "E664", {"start": v(-528.6, -189.2) * mm, "end": v(-558.34, -189.16) * mm});
            skLineSegment(sketch, "E665", {"start": v(-558.34, -189.16) * mm, "end": v(-588.05, -189.18) * mm});
            skLineSegment(sketch, "E666", {"start": v(-588.05, -189.18) * mm, "end": v(-617.73, -189.26) * mm});
            skLineSegment(sketch, "E667", {"start": v(-617.73, -189.26) * mm, "end": v(-647.37, -189.39) * mm});
            skLineSegment(sketch, "E668", {"start": v(-647.37, -189.39) * mm, "end": v(-676.98, -189.56) * mm});
            skLineSegment(sketch, "E669", {"start": v(-676.98, -189.56) * mm, "end": v(-706.56, -189.77) * mm});
            skLineSegment(sketch, "E670", {"start": v(-706.56, -189.77) * mm, "end": v(-736.1, -190) * mm});
            skLineSegment(sketch, "E671", {"start": v(-736.1, -190) * mm, "end": v(-765.63, -190.27) * mm});
            skLineSegment(sketch, "E672", {"start": v(-765.63, -190.27) * mm, "end": v(-795.13, -190.55) * mm});
            skLineSegment(sketch, "E673", {"start": v(-795.13, -190.55) * mm, "end": v(-824.61, -190.85) * mm});
            skLineSegment(sketch, "E674", {"start": v(-824.61, -190.85) * mm, "end": v(-854.09, -191.16) * mm});
            skLineSegment(sketch, "E675", {"start": v(-854.09, -191.16) * mm, "end": v(-883.54, -191.48) * mm});
            skLineSegment(sketch, "E676", {"start": v(-883.54, -191.48) * mm, "end": v(-912.96, -191.81) * mm});
            skLineSegment(sketch, "E677", {"start": v(-912.96, -191.81) * mm, "end": v(-942.36, -192.14) * mm});
            skLineSegment(sketch, "E678", {"start": v(-942.36, -192.14) * mm, "end": v(-971.5, -192.47) * mm});
            skLineSegment(sketch, "E679", {"start": v(-971.5, -192.47) * mm, "end": v(-1000.54, -192.79) * mm});
            skLineSegment(sketch, "E680", {"start": v(-1000.54, -192.79) * mm, "end": v(-1029.57, -193.1) * mm});
            skLineSegment(sketch, "E681", {"start": v(-1029.57, -193.1) * mm, "end": v(-1058.6, -193.4) * mm});
            skLineSegment(sketch, "E682", {"start": v(-1058.6, -193.4) * mm, "end": v(-1087.61, -193.7) * mm});
            skLineSegment(sketch, "E683", {"start": v(-1087.61, -193.7) * mm, "end": v(-1116.62, -194) * mm});
            skLineSegment(sketch, "E684", {"start": v(-1116.62, -194) * mm, "end": v(-1145.62, -194.28) * mm});
            skLineSegment(sketch, "E685", {"start": v(-1145.62, -194.28) * mm, "end": v(-1174.6, -194.54) * mm});
            skLineSegment(sketch, "E686", {"start": v(-1174.6, -194.54) * mm, "end": v(-1203.6, -194.8) * mm});
            skLineSegment(sketch, "E687", {"start": v(-1203.6, -194.8) * mm, "end": v(-1232.59, -195.05) * mm});
            skLineSegment(sketch, "E688", {"start": v(-1232.59, -195.05) * mm, "end": v(-1261.56, -195.28) * mm});
            skLineSegment(sketch, "E689", {"start": v(-1261.56, -195.28) * mm, "end": v(-1290.52, -195.5) * mm});
            skLineSegment(sketch, "E690", {"start": v(-1290.52, -195.5) * mm, "end": v(-1319.47, -195.7) * mm});
            skLineSegment(sketch, "E691", {"start": v(-1319.47, -195.7) * mm, "end": v(-1348.43, -195.88) * mm});
            skLineSegment(sketch, "E692", {"start": v(-1348.43, -195.88) * mm, "end": v(-1377.4, -196.04) * mm});
            skLineSegment(sketch, "E693", {"start": v(-1377.4, -196.04) * mm, "end": v(-1406.34, -196.19) * mm});
            skLineSegment(sketch, "E694", {"start": v(-1406.34, -196.19) * mm, "end": v(-1435.3, -196.32) * mm});
            skLineSegment(sketch, "E695", {"start": v(-1435.3, -196.32) * mm, "end": v(-1464.26, -196.43) * mm});
            skLineSegment(sketch, "E696", {"start": v(-1464.26, -196.43) * mm, "end": v(-1493.22, -196.53) * mm});
            skLineSegment(sketch, "E697", {"start": v(-1493.22, -196.53) * mm, "end": v(-1522.18, -196.6) * mm});
            skLineSegment(sketch, "E698", {"start": v(-1522.18, -196.6) * mm, "end": v(-1551.14, -196.68) * mm});
            skLineSegment(sketch, "E699", {"start": v(-1551.14, -196.68) * mm, "end": v(-1580.08, -196.73) * mm});
            skLineSegment(sketch, "E700", {"start": v(-1580.08, -196.73) * mm, "end": v(-1609.02, -196.76) * mm});
            skLineSegment(sketch, "E701", {"start": v(-1609.02, -196.76) * mm, "end": v(-1637.96, -196.78) * mm});
            skLineSegment(sketch, "E702", {"start": v(-1637.96, -196.78) * mm, "end": v(-1666.9, -196.77) * mm});
            skLineSegment(sketch, "E703", {"start": v(-1666.9, -196.77) * mm, "end": v(-1695.85, -196.75) * mm});
            skLineSegment(sketch, "E704", {"start": v(-1695.85, -196.75) * mm, "end": v(-1724.8, -196.7) * mm});
            skLineSegment(sketch, "E705", {"start": v(-1724.8, -196.7) * mm, "end": v(-1753.75, -196.65) * mm});
            skLineSegment(sketch, "E706", {"start": v(-1753.75, -196.65) * mm, "end": v(-1782.71, -196.58) * mm});
            skLineSegment(sketch, "E707", {"start": v(-1782.71, -196.58) * mm, "end": v(-1811.67, -196.5) * mm});
            skLineSegment(sketch, "E708", {"start": v(-1811.67, -196.5) * mm, "end": v(-1840.62, -196.4) * mm});
            skLineSegment(sketch, "E709", {"start": v(-1840.62, -196.4) * mm, "end": v(-1869.57, -196.27) * mm});
            skLineSegment(sketch, "E710", {"start": v(-1869.57, -196.27) * mm, "end": v(-1898.52, -196.13) * mm});
            skLineSegment(sketch, "E711", {"start": v(-1898.52, -196.13) * mm, "end": v(-1927.48, -195.98) * mm});
            skLineSegment(sketch, "E712", {"start": v(-1927.48, -195.98) * mm, "end": v(-1956.43, -195.8) * mm});
            skLineSegment(sketch, "E713", {"start": v(-1956.43, -195.8) * mm, "end": v(-1985.38, -195.61) * mm});
            skLineSegment(sketch, "E714", {"start": v(-1985.38, -195.61) * mm, "end": v(-2014.33, -195.4) * mm});
            skLineSegment(sketch, "E715", {"start": v(-2014.33, -195.4) * mm, "end": v(-2043.3, -195.17) * mm});
            skLineSegment(sketch, "E716", {"start": v(-2043.3, -195.17) * mm, "end": v(-2072.29, -194.93) * mm});
            skLineSegment(sketch, "E717", {"start": v(-2072.29, -194.93) * mm, "end": v(-2101.27, -194.68) * mm});
            skLineSegment(sketch, "E718", {"start": v(-2101.27, -194.68) * mm, "end": v(-2130.26, -194.41) * mm});
            skLineSegment(sketch, "E719", {"start": v(-2130.26, -194.41) * mm, "end": v(-2159.24, -194.13) * mm});
            skLineSegment(sketch, "E720", {"start": v(-2159.24, -194.13) * mm, "end": v(-2188.24, -193.84) * mm});
            skLineSegment(sketch, "E721", {"start": v(-2188.24, -193.84) * mm, "end": v(-2217.25, -193.54) * mm});
            skLineSegment(sketch, "E722", {"start": v(-2217.25, -193.54) * mm, "end": v(-2246.26, -193.23) * mm});
            skLineSegment(sketch, "E723", {"start": v(-2246.26, -193.23) * mm, "end": v(-2275.28, -192.9) * mm});
            skLineSegment(sketch, "E724", {"start": v(-2275.28, -192.9) * mm, "end": v(-2304.31, -192.58) * mm});
            skLineSegment(sketch, "E725", {"start": v(-2304.31, -192.58) * mm, "end": v(-2333.36, -192.25) * mm});
            skLineSegment(sketch, "E726", {"start": v(-2333.36, -192.25) * mm, "end": v(-2362.42, -191.92) * mm});
            skLineSegment(sketch, "E727", {"start": v(-2362.42, -191.92) * mm, "end": v(-2391.5, -191.58) * mm});
            skLineSegment(sketch, "E728", {"start": v(-2391.5, -191.58) * mm, "end": v(-2420.6, -191.25) * mm});
            skLineSegment(sketch, "E729", {"start": v(-2420.6, -191.25) * mm, "end": v(-2449.73, -190.94) * mm});
            skLineSegment(sketch, "E730", {"start": v(-2449.73, -190.94) * mm, "end": v(-2478.87, -190.63) * mm});
            skLineSegment(sketch, "E731", {"start": v(-2478.87, -190.63) * mm, "end": v(-2508.02, -190.34) * mm});
            skLineSegment(sketch, "E732", {"start": v(-2508.02, -190.34) * mm, "end": v(-2537.19, -190.07) * mm});
            skLineSegment(sketch, "E733", {"start": v(-2537.19, -190.07) * mm, "end": v(-2566.38, -189.82) * mm});
            skLineSegment(sketch, "E734", {"start": v(-2566.38, -189.82) * mm, "end": v(-2595.6, -189.6) * mm});
            skLineSegment(sketch, "E735", {"start": v(-2595.6, -189.6) * mm, "end": v(-2624.86, -189.4) * mm});
            skLineSegment(sketch, "E736", {"start": v(-2624.86, -189.4) * mm, "end": v(-2654.14, -189.25) * mm});
            skLineSegment(sketch, "E737", {"start": v(-2654.14, -189.25) * mm, "end": v(-2683.46, -189.14) * mm});
            skLineSegment(sketch, "E738", {"start": v(-2683.46, -189.14) * mm, "end": v(-2712.81, -189.09) * mm});
            skLineSegment(sketch, "E739", {"start": v(-2712.81, -189.09) * mm, "end": v(-2742.2, -189.1) * mm});
            skLineSegment(sketch, "E740", {"start": v(-2742.2, -189.1) * mm, "end": v(-2771.6, -189.16) * mm});
            skLineSegment(sketch, "E741", {"start": v(-2771.6, -189.16) * mm, "end": v(-2801.03, -189.3) * mm});
            skLineSegment(sketch, "E742", {"start": v(-2801.03, -189.3) * mm, "end": v(-2830.5, -189.5) * mm});
            skLineSegment(sketch, "E743", {"start": v(-2830.5, -189.5) * mm, "end": v(-2860, -189.8) * mm});
            skLineSegment(sketch, "E744", {"start": v(-2860, -189.8) * mm, "end": v(-2889.54, -190.18) * mm});
            skLineSegment(sketch, "E745", {"start": v(-2889.54, -190.18) * mm, "end": v(-2919.11, -190.66) * mm});
            skLineSegment(sketch, "E746", {"start": v(-2919.11, -190.66) * mm, "end": v(-2948.72, -191.24) * mm});
            skLineSegment(sketch, "E747", {"start": v(-2948.72, -191.24) * mm, "end": v(-2978.38, -191.94) * mm});
            skLineSegment(sketch, "E748", {"start": v(-2978.38, -191.94) * mm, "end": v(-3008.07, -192.76) * mm});
            skLineSegment(sketch, "E749", {"start": v(-3008.07, -192.76) * mm, "end": v(-3037.79, -193.71) * mm});
            skLineSegment(sketch, "E750", {"start": v(-3037.79, -193.71) * mm, "end": v(-3067.53, -194.8) * mm});
            skLineSegment(sketch, "E751", {"start": v(-3067.53, -194.8) * mm, "end": v(-3097.31, -196.03) * mm});
            skLineSegment(sketch, "E752", {"start": v(-3097.31, -196.03) * mm, "end": v(-3127.13, -197.42) * mm});
            skLineSegment(sketch, "E753", {"start": v(-3127.13, -197.42) * mm, "end": v(-3156.95, -198.97) * mm});
            skLineSegment(sketch, "E754", {"start": v(-3156.95, -198.97) * mm, "end": v(-3186.79, -200.68) * mm});
            skLineSegment(sketch, "E755", {"start": v(-3186.79, -200.68) * mm, "end": v(-3216.65, -202.56) * mm});
            skLineSegment(sketch, "E756", {"start": v(-3216.65, -202.56) * mm, "end": v(-3246.54, -204.61) * mm});
            skLineSegment(sketch, "E757", {"start": v(-3246.54, -204.61) * mm, "end": v(-3276.45, -206.86) * mm});
            skLineSegment(sketch, "E758", {"start": v(-3276.45, -206.86) * mm, "end": v(-3306.37, -209.3) * mm});
            skLineSegment(sketch, "E759", {"start": v(-3306.37, -209.3) * mm, "end": v(-3336.3, -211.93) * mm});
            skLineSegment(sketch, "E760", {"start": v(-3336.3, -211.93) * mm, "end": v(-3366.25, -214.77) * mm});
            skLineSegment(sketch, "E761", {"start": v(-3366.25, -214.77) * mm, "end": v(-3396.2, -217.82) * mm});
            skLineSegment(sketch, "E762", {"start": v(-3396.2, -217.82) * mm, "end": v(-3426.14, -221.1) * mm});
            skLineSegment(sketch, "E763", {"start": v(-3426.14, -221.1) * mm, "end": v(-3456.04, -224.57) * mm});
            skLineSegment(sketch, "E764", {"start": v(-3456.04, -224.57) * mm, "end": v(-3485.57, -228.21) * mm});
            skLineSegment(sketch, "E765", {"start": v(-3485.57, -228.21) * mm, "end": v(-3585.16, -240.5) * mm});
            skLineSegment(sketch, "E766", {"start": v(-3585.16, -240.5) * mm, "end": v(-3572.53, -340.04) * mm});
            skLineSegment(sketch, "E767", {"start": v(-3572.53, -340.04) * mm, "end": v(-3558.75, -448.28) * mm});
            skLineSegment(sketch, "E768", {"start": v(-3558.75, -448.28) * mm, "end": v(-3546.16, -547.06) * mm});
            skLineSegment(sketch, "E769", {"start": v(-3546.16, -547.06) * mm, "end": v(-3447.32, -534.88) * mm});
            skLineSegment(sketch, "E770", {"start": v(-3447.32, -534.88) * mm, "end": v(-3419.17, -531.4) * mm});
            skLineSegment(sketch, "E771", {"start": v(-3419.17, -531.4) * mm, "end": v(-3391.35, -528.18) * mm});
            skLineSegment(sketch, "E772", {"start": v(-3391.35, -528.18) * mm, "end": v(-3363.5, -525.14) * mm});
            skLineSegment(sketch, "E773", {"start": v(-3363.5, -525.14) * mm, "end": v(-3335.65, -522.3) * mm});
            skLineSegment(sketch, "E774", {"start": v(-3335.65, -522.3) * mm, "end": v(-3307.74, -519.67) * mm});
            skLineSegment(sketch, "E775", {"start": v(-3307.74, -519.67) * mm, "end": v(-3279.79, -517.21) * mm});
            skLineSegment(sketch, "E776", {"start": v(-3279.79, -517.21) * mm, "end": v(-3251.8, -514.94) * mm});
            skLineSegment(sketch, "E777", {"start": v(-3251.8, -514.94) * mm, "end": v(-3223.76, -512.85) * mm});
            skLineSegment(sketch, "E778", {"start": v(-3223.76, -512.85) * mm, "end": v(-3195.68, -510.92) * mm});
            skLineSegment(sketch, "E779", {"start": v(-3195.68, -510.92) * mm, "end": v(-3167.54, -509.16) * mm});
            skLineSegment(sketch, "E780", {"start": v(-3167.54, -509.16) * mm, "end": v(-3139.36, -507.55) * mm});
            skLineSegment(sketch, "E781", {"start": v(-3139.36, -507.55) * mm, "end": v(-3111.15, -506.1) * mm});
            skLineSegment(sketch, "E782", {"start": v(-3111.15, -506.1) * mm, "end": v(-3082.92, -504.79) * mm});
            skLineSegment(sketch, "E783", {"start": v(-3082.92, -504.79) * mm, "end": v(-3054.65, -503.62) * mm});
            skLineSegment(sketch, "E784", {"start": v(-3054.65, -503.62) * mm, "end": v(-3026.33, -502.6) * mm});
            skLineSegment(sketch, "E785", {"start": v(-3026.33, -502.6) * mm, "end": v(-2997.96, -501.68) * mm});
            skLineSegment(sketch, "E786", {"start": v(-2997.96, -501.68) * mm, "end": v(-2969.57, -500.9) * mm});
            skLineSegment(sketch, "E787", {"start": v(-2969.57, -500.9) * mm, "end": v(-2941.15, -500.24) * mm});
            skLineSegment(sketch, "E788", {"start": v(-2941.15, -500.24) * mm, "end": v(-2912.67, -499.68) * mm});
            skLineSegment(sketch, "E789", {"start": v(-2912.67, -499.68) * mm, "end": v(-2884.14, -499.22) * mm});
            skLineSegment(sketch, "E790", {"start": v(-2884.14, -499.22) * mm, "end": v(-2855.58, -498.86) * mm});
            skLineSegment(sketch, "E791", {"start": v(-2855.58, -498.86) * mm, "end": v(-2826.99, -498.58) * mm});
            skLineSegment(sketch, "E792", {"start": v(-2826.99, -498.58) * mm, "end": v(-2798.36, -498.38) * mm});
            skLineSegment(sketch, "E793", {"start": v(-2798.36, -498.38) * mm, "end": v(-2769.7, -498.25) * mm});
            skLineSegment(sketch, "E794", {"start": v(-2769.7, -498.25) * mm, "end": v(-2741, -498.18) * mm});
            skLineSegment(sketch, "E795", {"start": v(-2741, -498.18) * mm, "end": v(-2712.28, -498.18) * mm});
            skLineSegment(sketch, "E796", {"start": v(-2712.28, -498.18) * mm, "end": v(-2683.54, -498.24) * mm});
            skLineSegment(sketch, "E797", {"start": v(-2683.54, -498.24) * mm, "end": v(-2654.76, -498.35) * mm});
            skLineSegment(sketch, "E798", {"start": v(-2654.76, -498.35) * mm, "end": v(-2625.94, -498.5) * mm});
            skLineSegment(sketch, "E799", {"start": v(-2625.94, -498.5) * mm, "end": v(-2597.1, -498.69) * mm});
            skLineSegment(sketch, "E800", {"start": v(-2597.1, -498.69) * mm, "end": v(-2568.22, -498.9) * mm});
            skLineSegment(sketch, "E801", {"start": v(-2568.22, -498.9) * mm, "end": v(-2539.32, -499.16) * mm});
            skLineSegment(sketch, "E802", {"start": v(-2539.32, -499.16) * mm, "end": v(-2510.4, -499.43) * mm});
            skLineSegment(sketch, "E803", {"start": v(-2510.4, -499.43) * mm, "end": v(-2481.45, -499.71) * mm});
            skLineSegment(sketch, "E804", {"start": v(-2481.45, -499.71) * mm, "end": v(-2452.49, -500.01) * mm});
            skLineSegment(sketch, "E805", {"start": v(-2452.49, -500.01) * mm, "end": v(-2423.52, -500.33) * mm});
            skLineSegment(sketch, "E806", {"start": v(-2423.52, -500.33) * mm, "end": v(-2394.53, -500.66) * mm});
            skLineSegment(sketch, "E807", {"start": v(-2394.53, -500.66) * mm, "end": v(-2365.52, -500.99) * mm});
            skLineSegment(sketch, "E808", {"start": v(-2365.52, -500.99) * mm, "end": v(-2336.5, -501.33) * mm});
            skLineSegment(sketch, "E809", {"start": v(-2336.5, -501.33) * mm, "end": v(-2307.45, -501.66) * mm});
            skLineSegment(sketch, "E810", {"start": v(-2307.45, -501.66) * mm, "end": v(-2278.39, -501.99) * mm});
            skLineSegment(sketch, "E811", {"start": v(-2278.39, -501.99) * mm, "end": v(-2249.32, -502.31) * mm});
            skLineSegment(sketch, "E812", {"start": v(-2249.32, -502.31) * mm, "end": v(-2220.24, -502.63) * mm});
            skLineSegment(sketch, "E813", {"start": v(-2220.24, -502.63) * mm, "end": v(-2191.16, -502.93) * mm});
            skLineSegment(sketch, "E814", {"start": v(-2191.16, -502.93) * mm, "end": v(-2162.07, -503.23) * mm});
            skLineSegment(sketch, "E815", {"start": v(-2162.07, -503.23) * mm, "end": v(-2132.97, -503.51) * mm});
            skLineSegment(sketch, "E816", {"start": v(-2132.97, -503.51) * mm, "end": v(-2103.87, -503.78) * mm});
            skLineSegment(sketch, "E817", {"start": v(-2103.87, -503.78) * mm, "end": v(-2074.77, -504.04) * mm});
            skLineSegment(sketch, "E818", {"start": v(-2074.77, -504.04) * mm, "end": v(-2045.66, -504.28) * mm});
            skLineSegment(sketch, "E819", {"start": v(-2045.66, -504.28) * mm, "end": v(-2016.55, -504.51) * mm});
            skLineSegment(sketch, "E820", {"start": v(-2016.55, -504.51) * mm, "end": v(-1987.43, -504.73) * mm});
            skLineSegment(sketch, "E821", {"start": v(-1987.43, -504.73) * mm, "end": v(-1958.3, -504.92) * mm});
            skLineSegment(sketch, "E822", {"start": v(-1958.3, -504.92) * mm, "end": v(-1929.17, -505.1) * mm});
            skLineSegment(sketch, "E823", {"start": v(-1929.17, -505.1) * mm, "end": v(-1900.04, -505.25) * mm});
            skLineSegment(sketch, "E824", {"start": v(-1900.04, -505.25) * mm, "end": v(-1870.92, -505.4) * mm});
            skLineSegment(sketch, "E825", {"start": v(-1870.92, -505.4) * mm, "end": v(-1841.79, -505.51) * mm});
            skLineSegment(sketch, "E826", {"start": v(-1841.79, -505.51) * mm, "end": v(-1812.67, -505.62) * mm});
            skLineSegment(sketch, "E827", {"start": v(-1812.67, -505.62) * mm, "end": v(-1783.55, -505.7) * mm});
            skLineSegment(sketch, "E828", {"start": v(-1783.55, -505.7) * mm, "end": v(-1754.43, -505.78) * mm});
            skLineSegment(sketch, "E829", {"start": v(-1754.43, -505.78) * mm, "end": v(-1725.31, -505.84) * mm});
            skLineSegment(sketch, "E830", {"start": v(-1725.31, -505.84) * mm, "end": v(-1696.19, -505.89) * mm});
            skLineSegment(sketch, "E831", {"start": v(-1696.19, -505.89) * mm, "end": v(-1667.05, -505.91) * mm});
            skLineSegment(sketch, "E832", {"start": v(-1667.05, -505.91) * mm, "end": v(-1637.91, -505.92) * mm});
            skLineSegment(sketch, "E833", {"start": v(-1637.91, -505.92) * mm, "end": v(-1608.77, -505.9) * mm});
            skLineSegment(sketch, "E834", {"start": v(-1608.77, -505.9) * mm, "end": v(-1579.64, -505.87) * mm});
            skLineSegment(sketch, "E835", {"start": v(-1579.64, -505.87) * mm, "end": v(-1550.5, -505.81) * mm});
            skLineSegment(sketch, "E836", {"start": v(-1550.5, -505.81) * mm, "end": v(-1521.39, -505.74) * mm});
            skLineSegment(sketch, "E837", {"start": v(-1521.39, -505.74) * mm, "end": v(-1492.28, -505.65) * mm});
            skLineSegment(sketch, "E838", {"start": v(-1492.28, -505.65) * mm, "end": v(-1463.16, -505.55) * mm});
            skLineSegment(sketch, "E839", {"start": v(-1463.16, -505.55) * mm, "end": v(-1434.05, -505.44) * mm});
            skLineSegment(sketch, "E840", {"start": v(-1434.05, -505.44) * mm, "end": v(-1404.92, -505.3) * mm});
            skLineSegment(sketch, "E841", {"start": v(-1404.92, -505.3) * mm, "end": v(-1375.8, -505.16) * mm});
            skLineSegment(sketch, "E842", {"start": v(-1375.8, -505.16) * mm, "end": v(-1346.67, -505) * mm});
            skLineSegment(sketch, "E843", {"start": v(-1346.67, -505) * mm, "end": v(-1317.55, -504.81) * mm});
            skLineSegment(sketch, "E844", {"start": v(-1317.55, -504.81) * mm, "end": v(-1288.43, -504.61) * mm});
            skLineSegment(sketch, "E845", {"start": v(-1288.43, -504.61) * mm, "end": v(-1259.3, -504.4) * mm});
            skLineSegment(sketch, "E846", {"start": v(-1259.3, -504.4) * mm, "end": v(-1230.2, -504.16) * mm});
            skLineSegment(sketch, "E847", {"start": v(-1230.2, -504.16) * mm, "end": v(-1201.1, -503.9) * mm});
            skLineSegment(sketch, "E848", {"start": v(-1201.1, -503.9) * mm, "end": v(-1172, -503.65) * mm});
            skLineSegment(sketch, "E849", {"start": v(-1172, -503.65) * mm, "end": v(-1142.9, -503.38) * mm});
            skLineSegment(sketch, "E850", {"start": v(-1142.9, -503.38) * mm, "end": v(-1113.82, -503.1) * mm});
            skLineSegment(sketch, "E851", {"start": v(-1113.82, -503.1) * mm, "end": v(-1084.73, -502.8) * mm});
            skLineSegment(sketch, "E852", {"start": v(-1084.73, -502.8) * mm, "end": v(-1055.66, -502.5) * mm});
            skLineSegment(sketch, "E853", {"start": v(-1055.66, -502.5) * mm, "end": v(-1026.6, -502.18) * mm});
            skLineSegment(sketch, "E854", {"start": v(-1026.6, -502.18) * mm, "end": v(-997.53, -501.87) * mm});
            skLineSegment(sketch, "E855", {"start": v(-997.53, -501.87) * mm, "end": v(-968.48, -501.55) * mm});
            skLineSegment(sketch, "E856", {"start": v(-968.48, -501.55) * mm, "end": v(-939.34, -501.22) * mm});
            skLineSegment(sketch, "E857", {"start": v(-939.34, -501.22) * mm, "end": v(-909.97, -500.89) * mm});
            skLineSegment(sketch, "E858", {"start": v(-909.97, -500.89) * mm, "end": v(-880.62, -500.56) * mm});
            skLineSegment(sketch, "E859", {"start": v(-880.62, -500.56) * mm, "end": v(-851.3, -500.23) * mm});
            skLineSegment(sketch, "E860", {"start": v(-851.3, -500.23) * mm, "end": v(-822, -499.93) * mm});
            skLineSegment(sketch, "E861", {"start": v(-822, -499.93) * mm, "end": v(-792.7, -499.63) * mm});
            skLineSegment(sketch, "E862", {"start": v(-792.7, -499.63) * mm, "end": v(-763.43, -499.36) * mm});
            skLineSegment(sketch, "E863", {"start": v(-763.43, -499.36) * mm, "end": v(-734.18, -499.1) * mm});
            skLineSegment(sketch, "E864", {"start": v(-734.18, -499.1) * mm, "end": v(-704.95, -498.87) * mm});
            skLineSegment(sketch, "E865", {"start": v(-704.95, -498.87) * mm, "end": v(-675.74, -498.66) * mm});
            skLineSegment(sketch, "E866", {"start": v(-675.74, -498.66) * mm, "end": v(-646.56, -498.49) * mm});
            skLineSegment(sketch, "E867", {"start": v(-646.56, -498.49) * mm, "end": v(-617.43, -498.36) * mm});
            skLineSegment(sketch, "E868", {"start": v(-617.43, -498.36) * mm, "end": v(-588.33, -498.28) * mm});
            skLineSegment(sketch, "E869", {"start": v(-588.33, -498.28) * mm, "end": v(-559.26, -498.26) * mm});
            skLineSegment(sketch, "E870", {"start": v(-559.26, -498.26) * mm, "end": v(-530.21, -498.3) * mm});
            skLineSegment(sketch, "E871", {"start": v(-530.21, -498.3) * mm, "end": v(-501.2, -498.4) * mm});
            skLineSegment(sketch, "E872", {"start": v(-501.2, -498.4) * mm, "end": v(-472.23, -498.57) * mm});
            skLineSegment(sketch, "E873", {"start": v(-472.23, -498.57) * mm, "end": v(-443.28, -498.82) * mm});
            skLineSegment(sketch, "E874", {"start": v(-443.28, -498.82) * mm, "end": v(-414.37, -499.16) * mm});
            skLineSegment(sketch, "E875", {"start": v(-414.37, -499.16) * mm, "end": v(-385.5, -499.59) * mm});
            skLineSegment(sketch, "E876", {"start": v(-385.5, -499.59) * mm, "end": v(-356.67, -500.12) * mm});
            skLineSegment(sketch, "E877", {"start": v(-356.67, -500.12) * mm, "end": v(-327.88, -500.75) * mm});
            skLineSegment(sketch, "E878", {"start": v(-327.88, -500.75) * mm, "end": v(-299.14, -501.5) * mm});
            skLineSegment(sketch, "E879", {"start": v(-299.14, -501.5) * mm, "end": v(-270.45, -502.37) * mm});
            skLineSegment(sketch, "E880", {"start": v(-270.45, -502.37) * mm, "end": v(-241.79, -503.38) * mm});
            skLineSegment(sketch, "E881", {"start": v(-241.79, -503.38) * mm, "end": v(-213.16, -504.52) * mm});
            skLineSegment(sketch, "E882", {"start": v(-213.16, -504.52) * mm, "end": v(-184.58, -505.8) * mm});
            skLineSegment(sketch, "E883", {"start": v(-184.58, -505.8) * mm, "end": v(-156.05, -507.23) * mm});
            skLineSegment(sketch, "E884", {"start": v(-156.05, -507.23) * mm, "end": v(-127.54, -508.82) * mm});
            skLineSegment(sketch, "E885", {"start": v(-127.54, -508.82) * mm, "end": v(-99.06, -510.57) * mm});
            skLineSegment(sketch, "E886", {"start": v(-99.06, -510.57) * mm, "end": v(-70.62, -512.47) * mm});
            skLineSegment(sketch, "E887", {"start": v(-70.62, -512.47) * mm, "end": v(-42.02, -514.57) * mm});
            skLineSegment(sketch, "E888", {"start": v(-42.02, -514.57) * mm, "end": v(-12.74, -516.9) * mm});
            skLineSegment(sketch, "E889", {"start": v(-12.74, -516.9) * mm, "end": v(16.47, -519.41) * mm});
            skLineSegment(sketch, "E890", {"start": v(16.47, -519.41) * mm, "end": v(45.63, -522.14) * mm});
            skLineSegment(sketch, "E891", {"start": v(45.63, -522.14) * mm, "end": v(74.74, -525.08) * mm});
            skLineSegment(sketch, "E892", {"start": v(74.74, -525.08) * mm, "end": v(103.82, -528.24) * mm});
            skLineSegment(sketch, "E893", {"start": v(103.82, -528.24) * mm, "end": v(132.88, -531.62) * mm});
            skLineSegment(sketch, "E894", {"start": v(132.88, -531.62) * mm, "end": v(162.28, -535.26) * mm});
            skLineSegment(sketch, "E895", {"start": v(162.28, -535.26) * mm, "end": v(261.1, -547.49) * mm});
            skLineSegment(sketch, "E896", {"start": v(261.1, -547.49) * mm, "end": v(273.75, -448.72) * mm});
            skLineSegment(sketch, "E897", {"start": v(273.75, -448.72) * mm, "end": v(287.6, -340.5) * mm});
            skLineSegment(sketch, "E898", {"start": v(287.6, -340.5) * mm, "end": v(300.3, -240.94) * mm});
            skLineSegment(sketch, "E899", {"start": v(300.3, -240.94) * mm, "end": v(200.7, -228.6) * mm});
            skLineSegment(sketch, "E900", {"start": v(200.7, -228.6) * mm, "end": v(169.84, -224.79) * mm});
            skLineSegment(sketch, "E901", {"start": v(157.92, -324.08) * mm, "end": v(127.4, -320.52) * mm});
            skLineSegment(sketch, "E902", {"start": v(127.4, -320.52) * mm, "end": v(96.86, -317.2) * mm});
            skLineSegment(sketch, "E903", {"start": v(96.86, -317.2) * mm, "end": v(66.3, -314.11) * mm});
            skLineSegment(sketch, "E904", {"start": v(66.3, -314.11) * mm, "end": v(35.73, -311.24) * mm});
            skLineSegment(sketch, "E905", {"start": v(35.73, -311.24) * mm, "end": v(5.15, -308.6) * mm});
            skLineSegment(sketch, "E906", {"start": v(5.15, -308.6) * mm, "end": v(-25.44, -306.15) * mm});
            skLineSegment(sketch, "E907", {"start": v(-25.44, -306.15) * mm, "end": v(-55.28, -303.96) * mm});
            skLineSegment(sketch, "E908", {"start": v(-55.28, -303.96) * mm, "end": v(-84.92, -301.96) * mm});
            skLineSegment(sketch, "E909", {"start": v(-84.92, -301.96) * mm, "end": v(-114.55, -300.14) * mm});
            skLineSegment(sketch, "E910", {"start": v(-114.55, -300.14) * mm, "end": v(-144.18, -298.48) * mm});
            skLineSegment(sketch, "E911", {"start": v(-144.18, -298.48) * mm, "end": v(-173.82, -296.98) * mm});
            skLineSegment(sketch, "E912", {"start": v(-173.82, -296.98) * mm, "end": v(-203.45, -295.65) * mm});
            skLineSegment(sketch, "E913", {"start": v(-203.45, -295.65) * mm, "end": v(-233.07, -294.47) * mm});
            skLineSegment(sketch, "E914", {"start": v(-233.07, -294.47) * mm, "end": v(-262.7, -293.42) * mm});
            skLineSegment(sketch, "E915", {"start": v(-262.7, -293.42) * mm, "end": v(-292.3, -292.52) * mm});
            skLineSegment(sketch, "E916", {"start": v(-292.3, -292.52) * mm, "end": v(-321.9, -291.75) * mm});
            skLineSegment(sketch, "E917", {"start": v(-321.9, -291.75) * mm, "end": v(-351.5, -291.1) * mm});
            skLineSegment(sketch, "E918", {"start": v(-351.5, -291.1) * mm, "end": v(-381.09, -290.55) * mm});
            skLineSegment(sketch, "E919", {"start": v(-381.09, -290.55) * mm, "end": v(-410.66, -290.1) * mm});
            skLineSegment(sketch, "E920", {"start": v(-410.66, -290.1) * mm, "end": v(-440.23, -289.75) * mm});
            skLineSegment(sketch, "E921", {"start": v(-440.23, -289.75) * mm, "end": v(-469.78, -289.5) * mm});
            skLineSegment(sketch, "E922", {"start": v(-469.78, -289.5) * mm, "end": v(-499.32, -289.3) * mm});
            skLineSegment(sketch, "E923", {"start": v(-499.32, -289.3) * mm, "end": v(-528.85, -289.2) * mm});
            skLineSegment(sketch, "E924", {"start": v(-528.85, -289.2) * mm, "end": v(-558.37, -289.16) * mm});
            skLineSegment(sketch, "E925", {"start": v(-558.37, -289.16) * mm, "end": v(-587.88, -289.18) * mm});
            skLineSegment(sketch, "E926", {"start": v(-587.88, -289.18) * mm, "end": v(-617.38, -289.26) * mm});
            skLineSegment(sketch, "E927", {"start": v(-617.38, -289.26) * mm, "end": v(-646.86, -289.39) * mm});
            skLineSegment(sketch, "E928", {"start": v(-646.86, -289.39) * mm, "end": v(-676.34, -289.56) * mm});
            skLineSegment(sketch, "E929", {"start": v(-676.34, -289.56) * mm, "end": v(-705.8, -289.77) * mm});
            skLineSegment(sketch, "E930", {"start": v(-705.8, -289.77) * mm, "end": v(-735.26, -290) * mm});
            skLineSegment(sketch, "E931", {"start": v(-735.26, -290) * mm, "end": v(-764.71, -290.27) * mm});
            skLineSegment(sketch, "E932", {"start": v(-764.71, -290.27) * mm, "end": v(-794.15, -290.55) * mm});
            skLineSegment(sketch, "E933", {"start": v(-794.15, -290.55) * mm, "end": v(-823.58, -290.84) * mm});
            skLineSegment(sketch, "E934", {"start": v(-823.58, -290.84) * mm, "end": v(-853, -291.15) * mm});
            skLineSegment(sketch, "E935", {"start": v(-853, -291.15) * mm, "end": v(-882.43, -291.48) * mm});
            skLineSegment(sketch, "E936", {"start": v(-882.43, -291.48) * mm, "end": v(-911.84, -291.8) * mm});
            skLineSegment(sketch, "E937", {"start": v(-911.84, -291.8) * mm, "end": v(-941.24, -292.14) * mm});
            skLineSegment(sketch, "E938", {"start": v(-941.24, -292.14) * mm, "end": v(-970.4, -292.46) * mm});
            skLineSegment(sketch, "E939", {"start": v(-970.4, -292.46) * mm, "end": v(-999.45, -292.78) * mm});
            skLineSegment(sketch, "E940", {"start": v(-999.45, -292.78) * mm, "end": v(-1028.5, -293.1) * mm});
            skLineSegment(sketch, "E941", {"start": v(-1028.5, -293.1) * mm, "end": v(-1057.55, -293.4) * mm});
            skLineSegment(sketch, "E942", {"start": v(-1057.55, -293.4) * mm, "end": v(-1086.6, -293.7) * mm});
            skLineSegment(sketch, "E943", {"start": v(-1086.6, -293.7) * mm, "end": v(-1115.64, -294) * mm});
            skLineSegment(sketch, "E944", {"start": v(-1115.64, -294) * mm, "end": v(-1144.67, -294.27) * mm});
            skLineSegment(sketch, "E945", {"start": v(-1144.67, -294.27) * mm, "end": v(-1173.7, -294.54) * mm});
            skLineSegment(sketch, "E946", {"start": v(-1173.7, -294.54) * mm, "end": v(-1202.73, -294.8) * mm});
            skLineSegment(sketch, "E947", {"start": v(-1202.73, -294.8) * mm, "end": v(-1231.76, -295.04) * mm});
            skLineSegment(sketch, "E948", {"start": v(-1231.76, -295.04) * mm, "end": v(-1260.78, -295.28) * mm});
            skLineSegment(sketch, "E949", {"start": v(-1260.78, -295.28) * mm, "end": v(-1289.8, -295.5) * mm});
            skLineSegment(sketch, "E950", {"start": v(-1289.8, -295.5) * mm, "end": v(-1318.82, -295.7) * mm});
            skLineSegment(sketch, "E951", {"start": v(-1318.82, -295.7) * mm, "end": v(-1347.84, -295.87) * mm});
            skLineSegment(sketch, "E952", {"start": v(-1347.84, -295.87) * mm, "end": v(-1376.85, -296.04) * mm});
            skLineSegment(sketch, "E953", {"start": v(-1376.85, -296.04) * mm, "end": v(-1405.87, -296.19) * mm});
            skLineSegment(sketch, "E954", {"start": v(-1405.87, -296.19) * mm, "end": v(-1434.88, -296.32) * mm});
            skLineSegment(sketch, "E955", {"start": v(-1434.88, -296.32) * mm, "end": v(-1463.9, -296.43) * mm});
            skLineSegment(sketch, "E956", {"start": v(-1463.9, -296.43) * mm, "end": v(-1492.9, -296.53) * mm});
            skLineSegment(sketch, "E957", {"start": v(-1492.9, -296.53) * mm, "end": v(-1521.92, -296.6) * mm});
            skLineSegment(sketch, "E958", {"start": v(-1521.92, -296.6) * mm, "end": v(-1550.92, -296.68) * mm});
            skLineSegment(sketch, "E959", {"start": v(-1550.92, -296.68) * mm, "end": v(-1579.93, -296.73) * mm});
            skLineSegment(sketch, "E960", {"start": v(-1579.93, -296.73) * mm, "end": v(-1608.94, -296.76) * mm});
            skLineSegment(sketch, "E961", {"start": v(-1608.94, -296.76) * mm, "end": v(-1637.95, -296.78) * mm});
            skLineSegment(sketch, "E962", {"start": v(-1637.95, -296.78) * mm, "end": v(-1666.95, -296.77) * mm});
            skLineSegment(sketch, "E963", {"start": v(-1666.95, -296.77) * mm, "end": v(-1695.96, -296.75) * mm});
            skLineSegment(sketch, "E964", {"start": v(-1695.96, -296.75) * mm, "end": v(-1724.97, -296.7) * mm});
            skLineSegment(sketch, "E965", {"start": v(-1724.97, -296.7) * mm, "end": v(-1753.97, -296.65) * mm});
            skLineSegment(sketch, "E966", {"start": v(-1753.97, -296.65) * mm, "end": v(-1782.98, -296.58) * mm});
            skLineSegment(sketch, "E967", {"start": v(-1782.98, -296.58) * mm, "end": v(-1812, -296.5) * mm});
            skLineSegment(sketch, "E968", {"start": v(-1812, -296.5) * mm, "end": v(-1841, -296.4) * mm});
            skLineSegment(sketch, "E969", {"start": v(-1841, -296.4) * mm, "end": v(-1870.02, -296.27) * mm});
            skLineSegment(sketch, "E970", {"start": v(-1870.02, -296.27) * mm, "end": v(-1899.03, -296.13) * mm});
            skLineSegment(sketch, "E971", {"start": v(-1899.03, -296.13) * mm, "end": v(-1928.04, -295.97) * mm});
            skLineSegment(sketch, "E972", {"start": v(-1928.04, -295.97) * mm, "end": v(-1957.06, -295.8) * mm});
            skLineSegment(sketch, "E973", {"start": v(-1957.06, -295.8) * mm, "end": v(-1986.08, -295.6) * mm});
            skLineSegment(sketch, "E974", {"start": v(-1986.08, -295.6) * mm, "end": v(-2015.1, -295.4) * mm});
            skLineSegment(sketch, "E975", {"start": v(-2015.1, -295.4) * mm, "end": v(-2044.12, -295.17) * mm});
            skLineSegment(sketch, "E976", {"start": v(-2044.12, -295.17) * mm, "end": v(-2073.14, -294.92) * mm});
            skLineSegment(sketch, "E977", {"start": v(-2073.14, -294.92) * mm, "end": v(-2102.17, -294.67) * mm});
            skLineSegment(sketch, "E978", {"start": v(-2102.17, -294.67) * mm, "end": v(-2131.2, -294.4) * mm});
            skLineSegment(sketch, "E979", {"start": v(-2131.2, -294.4) * mm, "end": v(-2160.23, -294.13) * mm});
            skLineSegment(sketch, "E980", {"start": v(-2160.23, -294.13) * mm, "end": v(-2189.26, -293.83) * mm});
            skLineSegment(sketch, "E981", {"start": v(-2189.26, -293.83) * mm, "end": v(-2218.3, -293.53) * mm});
            skLineSegment(sketch, "E982", {"start": v(-2218.3, -293.53) * mm, "end": v(-2247.35, -293.22) * mm});
            skLineSegment(sketch, "E983", {"start": v(-2247.35, -293.22) * mm, "end": v(-2276.4, -292.9) * mm});
            skLineSegment(sketch, "E984", {"start": v(-2276.4, -292.9) * mm, "end": v(-2305.45, -292.57) * mm});
            skLineSegment(sketch, "E985", {"start": v(-2305.45, -292.57) * mm, "end": v(-2334.5, -292.24) * mm});
            skLineSegment(sketch, "E986", {"start": v(-2334.5, -292.24) * mm, "end": v(-2363.57, -291.9) * mm});
            skLineSegment(sketch, "E987", {"start": v(-2363.57, -291.9) * mm, "end": v(-2392.64, -291.58) * mm});
            skLineSegment(sketch, "E988", {"start": v(-2392.64, -291.58) * mm, "end": v(-2421.71, -291.25) * mm});
            skLineSegment(sketch, "E989", {"start": v(-2421.71, -291.25) * mm, "end": v(-2450.8, -290.93) * mm});
            skLineSegment(sketch, "E990", {"start": v(-2450.8, -290.93) * mm, "end": v(-2479.88, -290.63) * mm});
            skLineSegment(sketch, "E991", {"start": v(-2479.88, -290.63) * mm, "end": v(-2508.98, -290.34) * mm});
            skLineSegment(sketch, "E992", {"start": v(-2508.98, -290.34) * mm, "end": v(-2538.08, -290.07) * mm});
            skLineSegment(sketch, "E993", {"start": v(-2538.08, -290.07) * mm, "end": v(-2567.2, -289.81) * mm});
            skLineSegment(sketch, "E994", {"start": v(-2567.2, -289.81) * mm, "end": v(-2596.32, -289.6) * mm});
            skLineSegment(sketch, "E995", {"start": v(-2596.32, -289.6) * mm, "end": v(-2625.44, -289.4) * mm});
            skLineSegment(sketch, "E996", {"start": v(-2625.44, -289.4) * mm, "end": v(-2654.58, -289.25) * mm});
            skLineSegment(sketch, "E997", {"start": v(-2654.58, -289.25) * mm, "end": v(-2683.73, -289.14) * mm});
            skLineSegment(sketch, "E998", {"start": v(-2683.73, -289.14) * mm, "end": v(-2712.9, -289.09) * mm});
            skLineSegment(sketch, "E999", {"start": v(-2712.9, -289.09) * mm, "end": v(-2742.07, -289.1) * mm});
            skLineSegment(sketch, "E1000", {"start": v(-2742.07, -289.1) * mm, "end": v(-2771.25, -289.16) * mm});
            skLineSegment(sketch, "E1001", {"start": v(-2771.25, -289.16) * mm, "end": v(-2800.44, -289.3) * mm});
            skLineSegment(sketch, "E1002", {"start": v(-2800.44, -289.3) * mm, "end": v(-2829.65, -289.5) * mm});
            skLineSegment(sketch, "E1003", {"start": v(-2829.65, -289.5) * mm, "end": v(-2858.86, -289.8) * mm});
            skLineSegment(sketch, "E1004", {"start": v(-2858.86, -289.8) * mm, "end": v(-2888.09, -290.17) * mm});
            skLineSegment(sketch, "E1005", {"start": v(-2888.09, -290.17) * mm, "end": v(-2917.32, -290.65) * mm});
            skLineSegment(sketch, "E1006", {"start": v(-2917.32, -290.65) * mm, "end": v(-2946.57, -291.22) * mm});
            skLineSegment(sketch, "E1007", {"start": v(-2946.57, -291.22) * mm, "end": v(-2975.82, -291.9) * mm});
            skLineSegment(sketch, "E1008", {"start": v(-2975.82, -291.9) * mm, "end": v(-3005.09, -292.71) * mm});
            skLineSegment(sketch, "E1009", {"start": v(-3005.09, -292.71) * mm, "end": v(-3034.36, -293.65) * mm});
            skLineSegment(sketch, "E1010", {"start": v(-3034.36, -293.65) * mm, "end": v(-3063.64, -294.72) * mm});
            skLineSegment(sketch, "E1011", {"start": v(-3063.64, -294.72) * mm, "end": v(-3092.92, -295.94) * mm});
            skLineSegment(sketch, "E1012", {"start": v(-3092.92, -295.94) * mm, "end": v(-3122.2, -297.3) * mm});
            skLineSegment(sketch, "E1013", {"start": v(-3122.2, -297.3) * mm, "end": v(-3151.5, -298.82) * mm});
            skLineSegment(sketch, "E1014", {"start": v(-3151.5, -298.82) * mm, "end": v(-3180.79, -300.5) * mm});
            skLineSegment(sketch, "E1015", {"start": v(-3180.79, -300.5) * mm, "end": v(-3210.08, -302.34) * mm});
            skLineSegment(sketch, "E1016", {"start": v(-3210.08, -302.34) * mm, "end": v(-3239.37, -304.36) * mm});
            skLineSegment(sketch, "E1017", {"start": v(-3239.37, -304.36) * mm, "end": v(-3268.65, -306.55) * mm});
            skLineSegment(sketch, "E1018", {"start": v(-3268.65, -306.55) * mm, "end": v(-3297.93, -308.94) * mm});
            skLineSegment(sketch, "E1019", {"start": v(-3297.93, -308.94) * mm, "end": v(-3327.2, -311.51) * mm});
            skLineSegment(sketch, "E1020", {"start": v(-3327.2, -311.51) * mm, "end": v(-3356.46, -314.29) * mm});
            skLineSegment(sketch, "E1021", {"start": v(-3356.46, -314.29) * mm, "end": v(-3385.7, -317.27) * mm});
            skLineSegment(sketch, "E1022", {"start": v(-3385.7, -317.27) * mm, "end": v(-3414.94, -320.46) * mm});
            skLineSegment(sketch, "E1023", {"start": v(-3414.94, -320.46) * mm, "end": v(-3444.14, -323.86) * mm});
            skLineSegment(sketch, "E1024", {"start": v(-3444.14, -323.86) * mm, "end": v(-3473.33, -327.46) * mm});
            skLineSegment(sketch, "E1025", {"start": v(-3473.33, -327.46) * mm, "end": v(-3471.62, -340.98) * mm});
            skLineSegment(sketch, "E1026", {"start": v(-3471.62, -340.98) * mm, "end": v(-3469.9, -354.46) * mm});
            skLineSegment(sketch, "E1027", {"start": v(-3469.9, -354.46) * mm, "end": v(-3468.18, -367.97) * mm});
            skLineSegment(sketch, "E1028", {"start": v(-3468.18, -367.97) * mm, "end": v(-3466.45, -381.55) * mm});
            skLineSegment(sketch, "E1029", {"start": v(-3466.45, -381.55) * mm, "end": v(-3464.73, -395.06) * mm});
            skLineSegment(sketch, "E1030", {"start": v(-3464.73, -395.06) * mm, "end": v(-3463, -408.55) * mm});
            skLineSegment(sketch, "E1031", {"start": v(-3463, -408.55) * mm, "end": v(-3461.28, -422.06) * mm});
            skLineSegment(sketch, "E1032", {"start": v(-3461.28, -422.06) * mm, "end": v(-3459.55, -435.63) * mm});
            skLineSegment(sketch, "E1033", {"start": v(-3459.55, -435.63) * mm, "end": v(-3431.06, -432.12) * mm});
            skLineSegment(sketch, "E1034", {"start": v(-3431.06, -432.12) * mm, "end": v(-3402.54, -428.8) * mm});
            skLineSegment(sketch, "E1035", {"start": v(-3402.54, -428.8) * mm, "end": v(-3373.99, -425.7) * mm});
            skLineSegment(sketch, "E1036", {"start": v(-3373.99, -425.7) * mm, "end": v(-3345.42, -422.79) * mm});
            skLineSegment(sketch, "E1037", {"start": v(-3345.42, -422.79) * mm, "end": v(-3316.82, -420.08) * mm});
            skLineSegment(sketch, "E1038", {"start": v(-3316.82, -420.08) * mm, "end": v(-3288.2, -417.57) * mm});
            skLineSegment(sketch, "E1039", {"start": v(-3288.2, -417.57) * mm, "end": v(-3259.56, -415.24) * mm});
            skLineSegment(sketch, "E1040", {"start": v(-3259.56, -415.24) * mm, "end": v(-3230.9, -413.1) * mm});
            skLineSegment(sketch, "E1041", {"start": v(-3230.9, -413.1) * mm, "end": v(-3202.21, -411.14) * mm});
            skLineSegment(sketch, "E1042", {"start": v(-3202.21, -411.14) * mm, "end": v(-3173.51, -409.34) * mm});
            skLineSegment(sketch, "E1043", {"start": v(-3173.51, -409.34) * mm, "end": v(-3144.8, -407.7) * mm});
            skLineSegment(sketch, "E1044", {"start": v(-3144.8, -407.7) * mm, "end": v(-3116.05, -406.22) * mm});
            skLineSegment(sketch, "E1045", {"start": v(-3116.05, -406.22) * mm, "end": v(-3087.3, -404.88) * mm});
            skLineSegment(sketch, "E1046", {"start": v(-3087.3, -404.88) * mm, "end": v(-3058.53, -403.7) * mm});
            skLineSegment(sketch, "E1047", {"start": v(-3058.53, -403.7) * mm, "end": v(-3029.74, -402.65) * mm});
            skLineSegment(sketch, "E1048", {"start": v(-3029.74, -402.65) * mm, "end": v(-3000.94, -401.73) * mm});
            skLineSegment(sketch, "E1049", {"start": v(-3000.94, -401.73) * mm, "end": v(-2972.12, -400.93) * mm});
            skLineSegment(sketch, "E1050", {"start": v(-2972.12, -400.93) * mm, "end": v(-2943.29, -400.26) * mm});
            skLineSegment(sketch, "E1051", {"start": v(-2943.29, -400.26) * mm, "end": v(-2914.44, -399.7) * mm});
            skLineSegment(sketch, "E1052", {"start": v(-2914.44, -399.7) * mm, "end": v(-2885.59, -399.24) * mm});
            skLineSegment(sketch, "E1053", {"start": v(-2885.59, -399.24) * mm, "end": v(-2856.72, -398.87) * mm});
            skLineSegment(sketch, "E1054", {"start": v(-2856.72, -398.87) * mm, "end": v(-2827.83, -398.58) * mm});
            skLineSegment(sketch, "E1055", {"start": v(-2827.83, -398.58) * mm, "end": v(-2798.94, -398.38) * mm});
            skLineSegment(sketch, "E1056", {"start": v(-2798.94, -398.38) * mm, "end": v(-2770.03, -398.25) * mm});
            skLineSegment(sketch, "E1057", {"start": v(-2770.03, -398.25) * mm, "end": v(-2741.11, -398.18) * mm});
            skLineSegment(sketch, "E1058", {"start": v(-2741.11, -398.18) * mm, "end": v(-2712.19, -398.18) * mm});
            skLineSegment(sketch, "E1059", {"start": v(-2712.19, -398.18) * mm, "end": v(-2683.25, -398.24) * mm});
            skLineSegment(sketch, "E1060", {"start": v(-2683.25, -398.24) * mm, "end": v(-2654.3, -398.35) * mm});
            skLineSegment(sketch, "E1061", {"start": v(-2654.3, -398.35) * mm, "end": v(-2625.35, -398.5) * mm});
            skLineSegment(sketch, "E1062", {"start": v(-2625.35, -398.5) * mm, "end": v(-2596.38, -398.7) * mm});
            skLineSegment(sketch, "E1063", {"start": v(-2596.38, -398.7) * mm, "end": v(-2567.4, -398.91) * mm});
            skLineSegment(sketch, "E1064", {"start": v(-2567.4, -398.91) * mm, "end": v(-2538.42, -399.16) * mm});
            skLineSegment(sketch, "E1065", {"start": v(-2538.42, -399.16) * mm, "end": v(-2509.43, -399.43) * mm});
            skLineSegment(sketch, "E1066", {"start": v(-2509.43, -399.43) * mm, "end": v(-2480.43, -399.72) * mm});
            skLineSegment(sketch, "E1067", {"start": v(-2480.43, -399.72) * mm, "end": v(-2451.43, -400.02) * mm});
            skLineSegment(sketch, "E1068", {"start": v(-2451.43, -400.02) * mm, "end": v(-2422.41, -400.34) * mm});
            skLineSegment(sketch, "E1069", {"start": v(-2422.41, -400.34) * mm, "end": v(-2393.4, -400.66) * mm});
            skLineSegment(sketch, "E1070", {"start": v(-2393.4, -400.66) * mm, "end": v(-2364.37, -401) * mm});
            skLineSegment(sketch, "E1071", {"start": v(-2364.37, -401) * mm, "end": v(-2335.34, -401.33) * mm});
            skLineSegment(sketch, "E1072", {"start": v(-2335.34, -401.33) * mm, "end": v(-2306.3, -401.67) * mm});
            skLineSegment(sketch, "E1073", {"start": v(-2306.3, -401.67) * mm, "end": v(-2277.26, -402) * mm});
            skLineSegment(sketch, "E1074", {"start": v(-2277.26, -402) * mm, "end": v(-2248.22, -402.32) * mm});
            skLineSegment(sketch, "E1075", {"start": v(-2248.22, -402.32) * mm, "end": v(-2219.17, -402.63) * mm});
            skLineSegment(sketch, "E1076", {"start": v(-2219.17, -402.63) * mm, "end": v(-2190.12, -402.94) * mm});
            skLineSegment(sketch, "E1077", {"start": v(-2190.12, -402.94) * mm, "end": v(-2161.07, -403.23) * mm});
            skLineSegment(sketch, "E1078", {"start": v(-2161.07, -403.23) * mm, "end": v(-2132.02, -403.52) * mm});
            skLineSegment(sketch, "E1079", {"start": v(-2132.02, -403.52) * mm, "end": v(-2102.96, -403.79) * mm});
            skLineSegment(sketch, "E1080", {"start": v(-2102.96, -403.79) * mm, "end": v(-2073.9, -404.04) * mm});
            skLineSegment(sketch, "E1081", {"start": v(-2073.9, -404.04) * mm, "end": v(-2044.85, -404.28) * mm});
            skLineSegment(sketch, "E1082", {"start": v(-2044.85, -404.28) * mm, "end": v(-2015.79, -404.51) * mm});
            skLineSegment(sketch, "E1083", {"start": v(-2015.79, -404.51) * mm, "end": v(-1986.73, -404.73) * mm});
            skLineSegment(sketch, "E1084", {"start": v(-1986.73, -404.73) * mm, "end": v(-1957.66, -404.92) * mm});
            skLineSegment(sketch, "E1085", {"start": v(-1957.66, -404.92) * mm, "end": v(-1928.6, -405.1) * mm});
            skLineSegment(sketch, "E1086", {"start": v(-1928.6, -405.1) * mm, "end": v(-1899.53, -405.25) * mm});
            skLineSegment(sketch, "E1087", {"start": v(-1899.53, -405.25) * mm, "end": v(-1870.47, -405.4) * mm});
            skLineSegment(sketch, "E1088", {"start": v(-1870.47, -405.4) * mm, "end": v(-1841.4, -405.51) * mm});
            skLineSegment(sketch, "E1089", {"start": v(-1841.4, -405.51) * mm, "end": v(-1812.33, -405.62) * mm});
            skLineSegment(sketch, "E1090", {"start": v(-1812.33, -405.62) * mm, "end": v(-1783.27, -405.7) * mm});
            skLineSegment(sketch, "E1091", {"start": v(-1783.27, -405.7) * mm, "end": v(-1754.2, -405.78) * mm});
            skLineSegment(sketch, "E1092", {"start": v(-1754.2, -405.78) * mm, "end": v(-1725.13, -405.84) * mm});
            skLineSegment(sketch, "E1093", {"start": v(-1725.13, -405.84) * mm, "end": v(-1696.07, -405.89) * mm});
            skLineSegment(sketch, "E1094", {"start": v(-1696.07, -405.89) * mm, "end": v(-1667, -405.91) * mm});
            skLineSegment(sketch, "E1095", {"start": v(-1667, -405.91) * mm, "end": v(-1637.93, -405.92) * mm});
            skLineSegment(sketch, "E1096", {"start": v(-1637.93, -405.92) * mm, "end": v(-1608.86, -405.9) * mm});
            skLineSegment(sketch, "E1097", {"start": v(-1608.86, -405.9) * mm, "end": v(-1579.8, -405.87) * mm});
            skLineSegment(sketch, "E1098", {"start": v(-1579.8, -405.87) * mm, "end": v(-1550.73, -405.81) * mm});
            skLineSegment(sketch, "E1099", {"start": v(-1550.73, -405.81) * mm, "end": v(-1521.66, -405.74) * mm});
            skLineSegment(sketch, "E1100", {"start": v(-1521.66, -405.74) * mm, "end": v(-1492.6, -405.65) * mm});
            skLineSegment(sketch, "E1101", {"start": v(-1492.6, -405.65) * mm, "end": v(-1463.53, -405.55) * mm});
            skLineSegment(sketch, "E1102", {"start": v(-1463.53, -405.55) * mm, "end": v(-1434.47, -405.44) * mm});
            skLineSegment(sketch, "E1103", {"start": v(-1434.47, -405.44) * mm, "end": v(-1405.4, -405.3) * mm});
            skLineSegment(sketch, "E1104", {"start": v(-1405.4, -405.3) * mm, "end": v(-1376.33, -405.16) * mm});
            skLineSegment(sketch, "E1105", {"start": v(-1376.33, -405.16) * mm, "end": v(-1347.27, -405) * mm});
            skLineSegment(sketch, "E1106", {"start": v(-1347.27, -405) * mm, "end": v(-1318.2, -404.81) * mm});
            skLineSegment(sketch, "E1107", {"start": v(-1318.2, -404.81) * mm, "end": v(-1289.15, -404.61) * mm});
            skLineSegment(sketch, "E1108", {"start": v(-1289.15, -404.61) * mm, "end": v(-1260.08, -404.4) * mm});
            skLineSegment(sketch, "E1109", {"start": v(-1260.08, -404.4) * mm, "end": v(-1231.03, -404.16) * mm});
            skLineSegment(sketch, "E1110", {"start": v(-1231.03, -404.16) * mm, "end": v(-1201.97, -403.9) * mm});
            skLineSegment(sketch, "E1111", {"start": v(-1201.97, -403.9) * mm, "end": v(-1172.91, -403.65) * mm});
            skLineSegment(sketch, "E1112", {"start": v(-1172.91, -403.65) * mm, "end": v(-1143.86, -403.38) * mm});
            skLineSegment(sketch, "E1113", {"start": v(-1143.86, -403.38) * mm, "end": v(-1114.8, -403.1) * mm});
            skLineSegment(sketch, "E1114", {"start": v(-1114.8, -403.1) * mm, "end": v(-1085.76, -402.8) * mm});
            skLineSegment(sketch, "E1115", {"start": v(-1085.76, -402.8) * mm, "end": v(-1056.71, -402.5) * mm});
            skLineSegment(sketch, "E1116", {"start": v(-1056.71, -402.5) * mm, "end": v(-1027.67, -402.19) * mm});
            skLineSegment(sketch, "E1117", {"start": v(-1027.67, -402.19) * mm, "end": v(-998.63, -401.87) * mm});
            skLineSegment(sketch, "E1118", {"start": v(-998.63, -401.87) * mm, "end": v(-969.6, -401.55) * mm});
            skLineSegment(sketch, "E1119", {"start": v(-969.6, -401.55) * mm, "end": v(-940.47, -401.23) * mm});
            skLineSegment(sketch, "E1120", {"start": v(-940.47, -401.23) * mm, "end": v(-911.1, -400.9) * mm});
            skLineSegment(sketch, "E1121", {"start": v(-911.1, -400.9) * mm, "end": v(-881.73, -400.56) * mm});
            skLineSegment(sketch, "E1122", {"start": v(-881.73, -400.56) * mm, "end": v(-852.38, -400.24) * mm});
            skLineSegment(sketch, "E1123", {"start": v(-852.38, -400.24) * mm, "end": v(-823.02, -399.93) * mm});
            skLineSegment(sketch, "E1124", {"start": v(-823.02, -399.93) * mm, "end": v(-793.68, -399.64) * mm});
            skLineSegment(sketch, "E1125", {"start": v(-793.68, -399.64) * mm, "end": v(-764.34, -399.36) * mm});
            skLineSegment(sketch, "E1126", {"start": v(-764.34, -399.36) * mm, "end": v(-735.01, -399.1) * mm});
            skLineSegment(sketch, "E1127", {"start": v(-735.01, -399.1) * mm, "end": v(-705.7, -398.87) * mm});
            skLineSegment(sketch, "E1128", {"start": v(-705.7, -398.87) * mm, "end": v(-676.38, -398.66) * mm});
            skLineSegment(sketch, "E1129", {"start": v(-676.38, -398.66) * mm, "end": v(-647.08, -398.5) * mm});
            skLineSegment(sketch, "E1130", {"start": v(-647.08, -398.5) * mm, "end": v(-617.79, -398.36) * mm});
            skLineSegment(sketch, "E1131", {"start": v(-617.79, -398.36) * mm, "end": v(-588.5, -398.28) * mm});
            skLineSegment(sketch, "E1132", {"start": v(-588.5, -398.28) * mm, "end": v(-559.24, -398.26) * mm});
            skLineSegment(sketch, "E1133", {"start": v(-559.24, -398.26) * mm, "end": v(-529.98, -398.3) * mm});
            skLineSegment(sketch, "E1134", {"start": v(-529.98, -398.3) * mm, "end": v(-500.73, -398.4) * mm});
            skLineSegment(sketch, "E1135", {"start": v(-500.73, -398.4) * mm, "end": v(-471.49, -398.57) * mm});
            skLineSegment(sketch, "E1136", {"start": v(-471.49, -398.57) * mm, "end": v(-442.26, -398.83) * mm});
            skLineSegment(sketch, "E1137", {"start": v(-442.26, -398.83) * mm, "end": v(-413.05, -399.17) * mm});
            skLineSegment(sketch, "E1138", {"start": v(-413.05, -399.17) * mm, "end": v(-383.85, -399.6) * mm});
            skLineSegment(sketch, "E1139", {"start": v(-383.85, -399.6) * mm, "end": v(-354.66, -400.14) * mm});
            skLineSegment(sketch, "E1140", {"start": v(-354.66, -400.14) * mm, "end": v(-325.48, -400.78) * mm});
            skLineSegment(sketch, "E1141", {"start": v(-325.48, -400.78) * mm, "end": v(-296.32, -401.54) * mm});
            skLineSegment(sketch, "E1142", {"start": v(-296.32, -401.54) * mm, "end": v(-267.18, -402.42) * mm});
            skLineSegment(sketch, "E1143", {"start": v(-267.18, -402.42) * mm, "end": v(-238.05, -403.45) * mm});
            skLineSegment(sketch, "E1144", {"start": v(-238.05, -403.45) * mm, "end": v(-208.93, -404.6) * mm});
            skLineSegment(sketch, "E1145", {"start": v(-208.93, -404.6) * mm, "end": v(-179.84, -405.9) * mm});
            skLineSegment(sketch, "E1146", {"start": v(-179.84, -405.9) * mm, "end": v(-150.76, -407.37) * mm});
            skLineSegment(sketch, "E1147", {"start": v(-150.76, -407.37) * mm, "end": v(-121.7, -409) * mm});
            skLineSegment(sketch, "E1148", {"start": v(-121.7, -409) * mm, "end": v(-92.65, -410.77) * mm});
            skLineSegment(sketch, "E1149", {"start": v(-92.65, -410.77) * mm, "end": v(-63.63, -412.72) * mm});
            skLineSegment(sketch, "E1150", {"start": v(-63.63, -412.72) * mm, "end": v(-34.41, -414.86) * mm});
            skLineSegment(sketch, "E1151", {"start": v(-34.41, -414.86) * mm, "end": v(-4.48, -417.23) * mm});
            skLineSegment(sketch, "E1152", {"start": v(-4.48, -417.23) * mm, "end": v(25.43, -419.82) * mm});
            skLineSegment(sketch, "E1153", {"start": v(25.43, -419.82) * mm, "end": v(55.3, -422.61) * mm});
            skLineSegment(sketch, "E1154", {"start": v(55.3, -422.61) * mm, "end": v(85.16, -425.62) * mm});
            skLineSegment(sketch, "E1155", {"start": v(85.16, -425.62) * mm, "end": v(115, -428.87) * mm});
            skLineSegment(sketch, "E1156", {"start": v(115, -428.87) * mm, "end": v(144.8, -432.33) * mm});
            skLineSegment(sketch, "E1157", {"start": v(144.8, -432.33) * mm, "end": v(174.56, -436.01) * mm});
            skLineSegment(sketch, "E1158", {"start": v(174.56, -436.01) * mm, "end": v(176.3, -422.45) * mm});
            skLineSegment(sketch, "E1159", {"start": v(176.3, -422.45) * mm, "end": v(178.03, -408.94) * mm});
            skLineSegment(sketch, "E1160", {"start": v(178.03, -408.94) * mm, "end": v(179.76, -395.45) * mm});
            skLineSegment(sketch, "E1161", {"start": v(179.76, -395.45) * mm, "end": v(181.48, -381.93) * mm});
            skLineSegment(sketch, "E1162", {"start": v(181.48, -381.93) * mm, "end": v(183.22, -368.36) * mm});
            skLineSegment(sketch, "E1163", {"start": v(183.22, -368.36) * mm, "end": v(184.96, -354.85) * mm});
            skLineSegment(sketch, "E1164", {"start": v(184.96, -354.85) * mm, "end": v(186.68, -341.37) * mm});
            skLineSegment(sketch, "E1165", {"start": v(186.68, -341.37) * mm, "end": v(188.4, -327.85) * mm});
            skLineSegment(sketch, "E1166", {"start": v(188.4, -327.85) * mm, "end": v(157.92, -324.08) * mm});
            skLineSegment(sketch, "E1167", {"start": v(242.4, 406.77) * mm, "end": v(253.34, 482.2) * mm});
            skLineSegment(sketch, "E1168", {"start": v(253.34, 482.2) * mm, "end": v(263.9, 555.9) * mm});
            skLineSegment(sketch, "E1169", {"start": v(263.9, 555.9) * mm, "end": v(273.77, 627.83) * mm});
            skLineSegment(sketch, "E1170", {"start": v(273.77, 627.83) * mm, "end": v(283.52, 702.38) * mm});
            skLineSegment(sketch, "E1171", {"start": v(283.52, 702.38) * mm, "end": v(292.49, 777.08) * mm});
            skLineSegment(sketch, "E1172", {"start": v(292.49, 777.08) * mm, "end": v(300.45, 851.94) * mm});
            skLineSegment(sketch, "E1173", {"start": v(300.45, 851.94) * mm, "end": v(307.25, 926.87) * mm});
            skLineSegment(sketch, "E1174", {"start": v(307.25, 926.87) * mm, "end": v(312.95, 1003.72) * mm});
            skLineSegment(sketch, "E1175", {"start": v(312.95, 1003.72) * mm, "end": v(317.2, 1079.36) * mm});
            skLineSegment(sketch, "E1176", {"start": v(317.2, 1079.36) * mm, "end": v(320.01, 1154.3) * mm});
            skLineSegment(sketch, "E1177", {"start": v(320.01, 1154.3) * mm, "end": v(321.43, 1227.64) * mm});
            skLineSegment(sketch, "E1178", {"start": v(321.43, 1227.64) * mm, "end": v(321.53, 1302.25) * mm});
            skLineSegment(sketch, "E1179", {"start": v(321.53, 1302.25) * mm, "end": v(320.28, 1378.94) * mm});
            skLineSegment(sketch, "E1180", {"start": v(320.28, 1378.94) * mm, "end": v(317.65, 1457.82) * mm});
            skLineSegment(sketch, "E1181", {"start": v(317.65, 1457.82) * mm, "end": v(314.38, 1533.24) * mm});
            skLineSegment(sketch, "E1182", {"start": v(314.38, 1533.24) * mm, "end": v(310.4, 1608.32) * mm});
            skLineSegment(sketch, "E1183", {"start": v(310.4, 1608.32) * mm, "end": v(306.19, 1681.63) * mm});
            skLineSegment(sketch, "E1184", {"start": v(306.19, 1681.63) * mm, "end": v(301.63, 1756.8) * mm});
            skLineSegment(sketch, "E1185", {"start": v(301.63, 1756.8) * mm, "end": v(297.27, 1831.98) * mm});
            skLineSegment(sketch, "E1186", {"start": v(297.27, 1831.98) * mm, "end": v(221.36, 1832.9) * mm});
            skLineSegment(sketch, "E1187", {"start": v(221.36, 1832.9) * mm, "end": v(145.25, 1834.7) * mm});
            skLineSegment(sketch, "E1188", {"start": v(145.25, 1834.7) * mm, "end": v(69.08, 1837.16) * mm});
            skLineSegment(sketch, "E1189", {"start": v(69.08, 1837.16) * mm, "end": v(-4.96, 1839.76) * mm});
            skLineSegment(sketch, "E1190", {"start": v(-4.96, 1839.76) * mm, "end": v(-79.16, 1842.64) * mm});
            skLineSegment(sketch, "E1191", {"start": v(-79.16, 1842.64) * mm, "end": v(-153.54, 1845.66) * mm});
            skLineSegment(sketch, "E1192", {"start": v(-153.54, 1845.66) * mm, "end": v(-228.03, 1848.7) * mm});
            skLineSegment(sketch, "E1193", {"start": v(-228.03, 1848.7) * mm, "end": v(-302.68, 1851.7) * mm});
            skLineSegment(sketch, "E1194", {"start": v(-302.68, 1851.7) * mm, "end": v(-377.44, 1854.63) * mm});
            skLineSegment(sketch, "E1195", {"start": v(-377.44, 1854.63) * mm, "end": v(-452.3, 1857.41) * mm});
            skLineSegment(sketch, "E1196", {"start": v(-452.3, 1857.41) * mm, "end": v(-527.28, 1860.01) * mm});
            skLineSegment(sketch, "E1197", {"start": v(-527.28, 1860.01) * mm, "end": v(-602.31, 1862.43) * mm});
            skLineSegment(sketch, "E1198", {"start": v(-602.31, 1862.43) * mm, "end": v(-677.44, 1864.67) * mm});
            skLineSegment(sketch, "E1199", {"start": v(-677.44, 1864.67) * mm, "end": v(-752.63, 1866.76) * mm});
            skLineSegment(sketch, "E1200", {"start": v(-752.63, 1866.76) * mm, "end": v(-827.86, 1868.69) * mm});
            skLineSegment(sketch, "E1201", {"start": v(-827.86, 1868.69) * mm, "end": v(-902.8, 1870.42) * mm});
            skLineSegment(sketch, "E1202", {"start": v(-902.8, 1870.42) * mm, "end": v(-977.22, 1871.97) * mm});
            skLineSegment(sketch, "E1203", {"start": v(-977.22, 1871.97) * mm, "end": v(-1051.69, 1873.36) * mm});
            skLineSegment(sketch, "E1204", {"start": v(-1051.69, 1873.36) * mm, "end": v(-1126.18, 1874.55) * mm});
            skLineSegment(sketch, "E1205", {"start": v(-1126.18, 1874.55) * mm, "end": v(-1200.68, 1875.58) * mm});
            skLineSegment(sketch, "E1206", {"start": v(-1200.68, 1875.58) * mm, "end": v(-1275.2, 1876.44) * mm});
            skLineSegment(sketch, "E1207", {"start": v(-1275.2, 1876.44) * mm, "end": v(-1349.76, 1877.12) * mm});
            skLineSegment(sketch, "E1208", {"start": v(-1349.76, 1877.12) * mm, "end": v(-1424.3, 1877.64) * mm});
            skLineSegment(sketch, "E1209", {"start": v(-1424.3, 1877.64) * mm, "end": v(-1498.87, 1877.97) * mm});
            skLineSegment(sketch, "E1210", {"start": v(-1498.87, 1877.97) * mm, "end": v(-1573.44, 1878.11) * mm});
            skLineSegment(sketch, "E1211", {"start": v(-1573.44, 1878.11) * mm, "end": v(-1648, 1878.1) * mm});
            skLineSegment(sketch, "E1212", {"start": v(-1648, 1878.1) * mm, "end": v(-1722.57, 1877.94) * mm});
            skLineSegment(sketch, "E1213", {"start": v(-1722.57, 1877.94) * mm, "end": v(-1797.13, 1877.57) * mm});
            skLineSegment(sketch, "E1214", {"start": v(-1797.13, 1877.57) * mm, "end": v(-1871.68, 1877.04) * mm});
            skLineSegment(sketch, "E1215", {"start": v(-1871.68, 1877.04) * mm, "end": v(-1946.23, 1876.33) * mm});
            skLineSegment(sketch, "E1216", {"start": v(-1946.23, 1876.33) * mm, "end": v(-2020.76, 1875.43) * mm});
            skLineSegment(sketch, "E1217", {"start": v(-2020.76, 1875.43) * mm, "end": v(-2095.27, 1874.37) * mm});
            skLineSegment(sketch, "E1218", {"start": v(-2095.27, 1874.37) * mm, "end": v(-2169.77, 1873.13) * mm});
            skLineSegment(sketch, "E1219", {"start": v(-2169.77, 1873.13) * mm, "end": v(-2244.22, 1871.7) * mm});
            skLineSegment(sketch, "E1220", {"start": v(-2244.22, 1871.7) * mm, "end": v(-2318.66, 1870.1) * mm});
            skLineSegment(sketch, "E1221", {"start": v(-2318.66, 1870.1) * mm, "end": v(-2393.04, 1868.33) * mm});
            skLineSegment(sketch, "E1222", {"start": v(-2393.04, 1868.33) * mm, "end": v(-2467.4, 1866.38) * mm});
            skLineSegment(sketch, "E1223", {"start": v(-2467.4, 1866.38) * mm, "end": v(-2541.69, 1864.29) * mm});
            skLineSegment(sketch, "E1224", {"start": v(-2541.69, 1864.29) * mm, "end": v(-2615.9, 1862.03) * mm});
            skLineSegment(sketch, "E1225", {"start": v(-2615.9, 1862.03) * mm, "end": v(-2690.07, 1859.62) * mm});
            skLineSegment(sketch, "E1226", {"start": v(-2690.07, 1859.62) * mm, "end": v(-2764.14, 1857.01) * mm});
            skLineSegment(sketch, "E1227", {"start": v(-2764.14, 1857.01) * mm, "end": v(-2838.12, 1854.23) * mm});
            skLineSegment(sketch, "E1228", {"start": v(-2838.12, 1854.23) * mm, "end": v(-2912, 1851.33) * mm});
            skLineSegment(sketch, "E1229", {"start": v(-2912, 1851.33) * mm, "end": v(-2985.75, 1848.35) * mm});
            skLineSegment(sketch, "E1230", {"start": v(-2985.75, 1848.35) * mm, "end": v(-3059.37, 1845.33) * mm});
            skLineSegment(sketch, "E1231", {"start": v(-3059.37, 1845.33) * mm, "end": v(-3132.87, 1842.35) * mm});
            skLineSegment(sketch, "E1232", {"start": v(-3132.87, 1842.35) * mm, "end": v(-3206.18, 1839.52) * mm});
            skLineSegment(sketch, "E1233", {"start": v(-3206.18, 1839.52) * mm, "end": v(-3279.34, 1836.96) * mm});
            skLineSegment(sketch, "E1234", {"start": v(-3279.34, 1836.96) * mm, "end": v(-3352.34, 1834.79) * mm});
            skLineSegment(sketch, "E1235", {"start": v(-3352.34, 1834.79) * mm, "end": v(-3425.16, 1833.23) * mm});
            skLineSegment(sketch, "E1236", {"start": v(-3425.16, 1833.23) * mm, "end": v(-3497.82, 1832.53) * mm});
            skLineSegment(sketch, "E1237", {"start": v(-3497.82, 1832.53) * mm, "end": v(-3502.18, 1757.35) * mm});
            skLineSegment(sketch, "E1238", {"start": v(-3502.18, 1757.35) * mm, "end": v(-3506.73, 1682.17) * mm});
            skLineSegment(sketch, "E1239", {"start": v(-3506.73, 1682.17) * mm, "end": v(-3510.93, 1608.86) * mm});
            skLineSegment(sketch, "E1240", {"start": v(-3510.93, 1608.86) * mm, "end": v(-3514.88, 1533.77) * mm});
            skLineSegment(sketch, "E1241", {"start": v(-3514.88, 1533.77) * mm, "end": v(-3518.15, 1458.35) * mm});
            skLineSegment(sketch, "E1242", {"start": v(-3518.15, 1458.35) * mm, "end": v(-3520.78, 1379.44) * mm});
            skLineSegment(sketch, "E1243", {"start": v(-3520.78, 1379.44) * mm, "end": v(-3522.03, 1302.74) * mm});
            skLineSegment(sketch, "E1244", {"start": v(-3522.03, 1302.74) * mm, "end": v(-3521.93, 1228.1) * mm});
            skLineSegment(sketch, "E1245", {"start": v(-3521.93, 1228.1) * mm, "end": v(-3520.52, 1154.75) * mm});
            skLineSegment(sketch, "E1246", {"start": v(-3520.52, 1154.75) * mm, "end": v(-3517.72, 1079.79) * mm});
            skLineSegment(sketch, "E1247", {"start": v(-3517.72, 1079.79) * mm, "end": v(-3513.5, 1004.13) * mm});
            skLineSegment(sketch, "E1248", {"start": v(-3513.5, 1004.13) * mm, "end": v(-3507.82, 927.25) * mm});
            skLineSegment(sketch, "E1249", {"start": v(-3507.82, 927.25) * mm, "end": v(-3501.05, 852.3) * mm});
            skLineSegment(sketch, "E1250", {"start": v(-3501.05, 852.3) * mm, "end": v(-3493.12, 777.43) * mm});
            skLineSegment(sketch, "E1251", {"start": v(-3493.12, 777.43) * mm, "end": v(-3484.19, 702.7) * mm});
            skLineSegment(sketch, "E1252", {"start": v(-3484.19, 702.7) * mm, "end": v(-3474.48, 628.16) * mm});
            skLineSegment(sketch, "E1253", {"start": v(-3474.48, 628.16) * mm, "end": v(-3464.65, 556.2) * mm});
            skLineSegment(sketch, "E1254", {"start": v(-3464.65, 556.2) * mm, "end": v(-3454.14, 482.5) * mm});
            skLineSegment(sketch, "E1255", {"start": v(-3454.14, 482.5) * mm, "end": v(-3443.24, 407.05) * mm});
            skLineSegment(sketch, "E1256", {"start": v(-3443.24, 407.05) * mm, "end": v(-3432.16, 329.86) * mm});
            skLineSegment(sketch, "E1257", {"start": v(-3432.16, 329.86) * mm, "end": v(-3362.2, 335.5) * mm});
            skLineSegment(sketch, "E1258", {"start": v(-3362.2, 335.5) * mm, "end": v(-3292, 340.09) * mm});
            skLineSegment(sketch, "E1259", {"start": v(-3292, 340.09) * mm, "end": v(-3221.6, 343.82) * mm});
            skLineSegment(sketch, "E1260", {"start": v(-3221.6, 343.82) * mm, "end": v(-3151.02, 346.86) * mm});
            skLineSegment(sketch, "E1261", {"start": v(-3151.02, 346.86) * mm, "end": v(-3080.27, 349.32) * mm});
            skLineSegment(sketch, "E1262", {"start": v(-3080.27, 349.32) * mm, "end": v(-3009.36, 351.34) * mm});
            skLineSegment(sketch, "E1263", {"start": v(-3009.36, 351.34) * mm, "end": v(-2938.3, 353) * mm});
            skLineSegment(sketch, "E1264", {"start": v(-2938.3, 353) * mm, "end": v(-2867.1, 354.4) * mm});
            skLineSegment(sketch, "E1265", {"start": v(-2867.1, 354.4) * mm, "end": v(-2795.8, 355.57) * mm});
            skLineSegment(sketch, "E1266", {"start": v(-2795.8, 355.57) * mm, "end": v(-2724.39, 356.58) * mm});
            skLineSegment(sketch, "E1267", {"start": v(-2724.39, 356.58) * mm, "end": v(-2652.87, 357.47) * mm});
            skLineSegment(sketch, "E1268", {"start": v(-2652.87, 357.47) * mm, "end": v(-2581.3, 358.25) * mm});
            skLineSegment(sketch, "E1269", {"start": v(-2581.3, 358.25) * mm, "end": v(-2509.64, 358.93) * mm});
            skLineSegment(sketch, "E1270", {"start": v(-2509.64, 358.93) * mm, "end": v(-2437.92, 359.51) * mm});
            skLineSegment(sketch, "E1271", {"start": v(-2437.92, 359.51) * mm, "end": v(-2366.14, 360.02) * mm});
            skLineSegment(sketch, "E1272", {"start": v(-2366.14, 360.02) * mm, "end": v(-2294.32, 360.46) * mm});
            skLineSegment(sketch, "E1273", {"start": v(-2294.32, 360.46) * mm, "end": v(-2222.45, 360.83) * mm});
            skLineSegment(sketch, "E1274", {"start": v(-2222.45, 360.83) * mm, "end": v(-2150.54, 361.1) * mm});
            skLineSegment(sketch, "E1275", {"start": v(-2150.54, 361.1) * mm, "end": v(-2078.61, 361.31) * mm});
            skLineSegment(sketch, "E1276", {"start": v(-2078.61, 361.31) * mm, "end": v(-2006.65, 361.48) * mm});
            skLineSegment(sketch, "E1277", {"start": v(-2006.65, 361.48) * mm, "end": v(-1934.65, 361.6) * mm});
            skLineSegment(sketch, "E1278", {"start": v(-1934.65, 361.6) * mm, "end": v(-1862.65, 361.68) * mm});
            skLineSegment(sketch, "E1279", {"start": v(-1862.65, 361.68) * mm, "end": v(-1790.63, 361.75) * mm});
            skLineSegment(sketch, "E1280", {"start": v(-1790.63, 361.75) * mm, "end": v(-1718.59, 361.8) * mm});
            skLineSegment(sketch, "E1281", {"start": v(-1718.59, 361.8) * mm, "end": v(-1646.55, 361.81) * mm});
            skLineSegment(sketch, "E1282", {"start": v(-1646.55, 361.81) * mm, "end": v(-1574.5, 361.8) * mm});
            skLineSegment(sketch, "E1283", {"start": v(-1574.5, 361.8) * mm, "end": v(-1502.47, 361.8) * mm});
            skLineSegment(sketch, "E1284", {"start": v(-1502.47, 361.8) * mm, "end": v(-1430.44, 361.75) * mm});
            skLineSegment(sketch, "E1285", {"start": v(-1430.44, 361.75) * mm, "end": v(-1358.41, 361.68) * mm});
            skLineSegment(sketch, "E1286", {"start": v(-1358.41, 361.68) * mm, "end": v(-1286.4, 361.59) * mm});
            skLineSegment(sketch, "E1287", {"start": v(-1286.4, 361.59) * mm, "end": v(-1214.42, 361.48) * mm});
            skLineSegment(sketch, "E1288", {"start": v(-1214.42, 361.48) * mm, "end": v(-1142.45, 361.3) * mm});
            skLineSegment(sketch, "E1289", {"start": v(-1142.45, 361.3) * mm, "end": v(-1070.51, 361.08) * mm});
            skLineSegment(sketch, "E1290", {"start": v(-1070.51, 361.08) * mm, "end": v(-998.61, 360.8) * mm});
            skLineSegment(sketch, "E1291", {"start": v(-998.61, 360.8) * mm, "end": v(-926.74, 360.43) * mm});
            skLineSegment(sketch, "E1292", {"start": v(-926.74, 360.43) * mm, "end": v(-854.38, 359.98) * mm});
            skLineSegment(sketch, "E1293", {"start": v(-854.38, 359.98) * mm, "end": v(-781.75, 359.47) * mm});
            skLineSegment(sketch, "E1294", {"start": v(-781.75, 359.47) * mm, "end": v(-709.16, 358.87) * mm});
            skLineSegment(sketch, "E1295", {"start": v(-709.16, 358.87) * mm, "end": v(-636.65, 358.2) * mm});
            skLineSegment(sketch, "E1296", {"start": v(-636.65, 358.2) * mm, "end": v(-564.2, 357.4) * mm});
            skLineSegment(sketch, "E1297", {"start": v(-564.2, 357.4) * mm, "end": v(-491.84, 356.5) * mm});
            skLineSegment(sketch, "E1298", {"start": v(-491.84, 356.5) * mm, "end": v(-419.56, 355.5) * mm});
            skLineSegment(sketch, "E1299", {"start": v(-419.56, 355.5) * mm, "end": v(-347.4, 354.3) * mm});
            skLineSegment(sketch, "E1300", {"start": v(-347.4, 354.3) * mm, "end": v(-275.37, 352.91) * mm});
            skLineSegment(sketch, "E1301", {"start": v(-275.37, 352.91) * mm, "end": v(-203.43, 351.25) * mm});
            skLineSegment(sketch, "E1302", {"start": v(-203.43, 351.25) * mm, "end": v(-131.67, 349.23) * mm});
            skLineSegment(sketch, "E1303", {"start": v(-131.67, 349.23) * mm, "end": v(-60.07, 346.77) * mm});
            skLineSegment(sketch, "E1304", {"start": v(-60.07, 346.77) * mm, "end": v(11.36, 343.73) * mm});
            skLineSegment(sketch, "E1305", {"start": v(11.36, 343.73) * mm, "end": v(84.84, 339.99) * mm});
            skLineSegment(sketch, "E1306", {"start": v(84.84, 339.99) * mm, "end": v(158.2, 335.34) * mm});
            skLineSegment(sketch, "E1307", {"start": v(158.2, 335.34) * mm, "end": v(231.31, 329.57) * mm});
            skLineSegment(sketch, "E1308", {"start": v(231.31, 329.57) * mm, "end": v(242.4, 406.77) * mm});
            skLineSegment(sketch, "E1309", {"start": v(128.43, -1362.8) * mm, "end": v(29.55, -1314.89) * mm});
            skLineSegment(sketch, "E1310", {"start": v(29.55, -1314.89) * mm, "end": v(-63.53, -1272.94) * mm});
            skLineSegment(sketch, "E1311", {"start": v(-63.53, -1272.94) * mm, "end": v(-159.79, -1232.6) * mm});
            skLineSegment(sketch, "E1312", {"start": v(-159.79, -1232.6) * mm, "end": v(-257.19, -1194.95) * mm});
            skLineSegment(sketch, "E1313", {"start": v(-257.19, -1194.95) * mm, "end": v(-355.67, -1160.02) * mm});
            skLineSegment(sketch, "E1314", {"start": v(-355.67, -1160.02) * mm, "end": v(-455.15, -1127.9) * mm});
            skLineSegment(sketch, "E1315", {"start": v(-455.15, -1127.9) * mm, "end": v(-555.56, -1098.61) * mm});
            skLineSegment(sketch, "E1316", {"start": v(-555.56, -1098.61) * mm, "end": v(-656.8, -1072.22) * mm});
            skLineSegment(sketch, "E1317", {"start": v(-656.8, -1072.22) * mm, "end": v(-758.8, -1048.75) * mm});
            skLineSegment(sketch, "E1318", {"start": v(-758.8, -1048.75) * mm, "end": v(-861.12, -1028.28) * mm});
            skLineSegment(sketch, "E1319", {"start": v(-861.12, -1028.28) * mm, "end": v(-963.15, -1010.91) * mm});
            skLineSegment(sketch, "E1320", {"start": v(-963.15, -1010.91) * mm, "end": v(-1065.65, -996.46) * mm});
            skLineSegment(sketch, "E1321", {"start": v(-1065.65, -996.46) * mm, "end": v(-1168.54, -984.95) * mm});
            skLineSegment(sketch, "E1322", {"start": v(-1168.54, -984.95) * mm, "end": v(-1271.73, -976.39) * mm});
            skLineSegment(sketch, "E1323", {"start": v(-1271.73, -976.39) * mm, "end": v(-1375.13, -970.78) * mm});
            skLineSegment(sketch, "E1324", {"start": v(-1375.13, -970.78) * mm, "end": v(-1478.65, -968.13) * mm});
            skLineSegment(sketch, "E1325", {"start": v(-1478.65, -968.13) * mm, "end": v(-1582.2, -968.45) * mm});
            skLineSegment(sketch, "E1326", {"start": v(-1582.2, -968.45) * mm, "end": v(-1685.71, -971.73) * mm});
            skLineSegment(sketch, "E1327", {"start": v(-1685.71, -971.73) * mm, "end": v(-1789.07, -977.97) * mm});
            skLineSegment(sketch, "E1328", {"start": v(-1789.07, -977.97) * mm, "end": v(-1892.2, -987.17) * mm});
            skLineSegment(sketch, "E1329", {"start": v(-1892.2, -987.17) * mm, "end": v(-1995.02, -999.3) * mm});
            skLineSegment(sketch, "E1330", {"start": v(-1995.02, -999.3) * mm, "end": v(-2097.43, -1014.39) * mm});
            skLineSegment(sketch, "E1331", {"start": v(-2097.43, -1014.39) * mm, "end": v(-2199.35, -1032.38) * mm});
            skLineSegment(sketch, "E1332", {"start": v(-2199.35, -1032.38) * mm, "end": v(-2300.7, -1053.28) * mm});
            skLineSegment(sketch, "E1333", {"start": v(-2300.7, -1053.28) * mm, "end": v(-2401.36, -1077.06) * mm});
            skLineSegment(sketch, "E1334", {"start": v(-2401.36, -1077.06) * mm, "end": v(-2501.29, -1103.67) * mm});
            skLineSegment(sketch, "E1335", {"start": v(-2501.29, -1103.67) * mm, "end": v(-2600.38, -1133.1) * mm});
            skLineSegment(sketch, "E1336", {"start": v(-2600.38, -1133.1) * mm, "end": v(-2698.55, -1165.31) * mm});
            skLineSegment(sketch, "E1337", {"start": v(-2698.55, -1165.31) * mm, "end": v(-2795.73, -1200.25) * mm});
            skLineSegment(sketch, "E1338", {"start": v(-2795.73, -1200.25) * mm, "end": v(-2891.85, -1237.86) * mm});
            skLineSegment(sketch, "E1339", {"start": v(-2891.85, -1237.86) * mm, "end": v(-2986.84, -1278.06) * mm});
            skLineSegment(sketch, "E1340", {"start": v(-2986.84, -1278.06) * mm, "end": v(-3080.64, -1320.78) * mm});
            skLineSegment(sketch, "E1341", {"start": v(-3080.64, -1320.78) * mm, "end": v(-3173.24, -1365.88) * mm});
            skLineSegment(sketch, "E1342", {"start": v(-3173.24, -1365.88) * mm, "end": v(-3264.62, -1413.23) * mm});
            skLineSegment(sketch, "E1343", {"start": v(-3264.62, -1413.23) * mm, "end": v(-3216.83, -1506.2) * mm});
            skLineSegment(sketch, "E1344", {"start": v(-3216.83, -1506.2) * mm, "end": v(-3169.1, -1598.36) * mm});
            skLineSegment(sketch, "E1345", {"start": v(-3169.1, -1598.36) * mm, "end": v(-3120.1, -1692.13) * mm});
            skLineSegment(sketch, "E1346", {"start": v(-3120.1, -1692.13) * mm, "end": v(-3069.87, -1787.29) * mm});
            skLineSegment(sketch, "E1347", {"start": v(-3069.87, -1787.29) * mm, "end": v(-3019.67, -1881.3) * mm});
            skLineSegment(sketch, "E1348", {"start": v(-3019.67, -1881.3) * mm, "end": v(-2968.62, -1975.88) * mm});
            skLineSegment(sketch, "E1349", {"start": v(-2968.62, -1975.88) * mm, "end": v(-2917.04, -2070.46) * mm});
            skLineSegment(sketch, "E1350", {"start": v(-2917.04, -2070.46) * mm, "end": v(-2865.16, -2164.69) * mm});
            skLineSegment(sketch, "E1351", {"start": v(-2865.16, -2164.69) * mm, "end": v(-2813.23, -2258.18) * mm});
            skLineSegment(sketch, "E1352", {"start": v(-2813.23, -2258.18) * mm, "end": v(-2761.53, -2350.61) * mm});
            skLineSegment(sketch, "E1353", {"start": v(-2761.53, -2350.61) * mm, "end": v(-2710.3, -2441.68) * mm});
            skLineSegment(sketch, "E1354", {"start": v(-2710.3, -2441.68) * mm, "end": v(-2659.79, -2531.12) * mm});
            skLineSegment(sketch, "E1355", {"start": v(-2659.79, -2531.12) * mm, "end": v(-2610.22, -2618.7) * mm});
            skLineSegment(sketch, "E1356", {"start": v(-2610.22, -2618.7) * mm, "end": v(-2558.67, -2709.51) * mm});
            skLineSegment(sketch, "E1357", {"start": v(-2558.67, -2709.51) * mm, "end": v(-2507.74, -2799.11) * mm});
            skLineSegment(sketch, "E1358", {"start": v(-2507.74, -2799.11) * mm, "end": v(-2456.06, -2889.96) * mm});
            skLineSegment(sketch, "E1359", {"start": v(-2456.06, -2889.96) * mm, "end": v(-2403.75, -2982.05) * mm});
            skLineSegment(sketch, "E1360", {"start": v(-2403.75, -2982.05) * mm, "end": v(-2351.11, -3075.13) * mm});
            skLineSegment(sketch, "E1361", {"start": v(-2351.11, -3075.13) * mm, "end": v(-2297.24, -3171.02) * mm});
            skLineSegment(sketch, "E1362", {"start": v(-2297.24, -3171.02) * mm, "end": v(-2246.44, -3262.78) * mm});
            skLineSegment(sketch, "E1363", {"start": v(-2246.44, -3262.78) * mm, "end": v(-2196.3, -3354.83) * mm});
            skLineSegment(sketch, "E1364", {"start": v(-2196.3, -3354.83) * mm, "end": v(-2147, -3447.25) * mm});
            skLineSegment(sketch, "E1365", {"start": v(-2147, -3447.25) * mm, "end": v(-2098.79, -3540.18) * mm});
            skLineSegment(sketch, "E1366", {"start": v(-2098.79, -3540.18) * mm, "end": v(-2051.88, -3633.72) * mm});
            skLineSegment(sketch, "E1367", {"start": v(-2051.88, -3633.72) * mm, "end": v(-2004.82, -3732.13) * mm});
            skLineSegment(sketch, "E1368", {"start": v(-2004.82, -3732.13) * mm, "end": v(-1960.73, -3829.22) * mm});
            skLineSegment(sketch, "E1369", {"start": v(-1960.73, -3829.22) * mm, "end": v(-1919.9, -3924.79) * mm});
            skLineSegment(sketch, "E1370", {"start": v(-1919.9, -3924.79) * mm, "end": v(-1882.45, -4018.63) * mm});
            skLineSegment(sketch, "E1371", {"start": v(-1882.45, -4018.63) * mm, "end": v(-1848.18, -4110.55) * mm});
            skLineSegment(sketch, "E1372", {"start": v(-1848.18, -4110.55) * mm, "end": v(-1830.43, -4102.34) * mm});
            skLineSegment(sketch, "E1373", {"start": v(-1830.43, -4102.34) * mm, "end": v(-1812.7, -4094.1) * mm});
            skLineSegment(sketch, "E1374", {"start": v(-1812.7, -4094.1) * mm, "end": v(-1794.89, -4086.04) * mm});
            skLineSegment(sketch, "E1375", {"start": v(-1794.89, -4086.04) * mm, "end": v(-1776.96, -4078.24) * mm});
            skLineSegment(sketch, "E1376", {"start": v(-1776.96, -4078.24) * mm, "end": v(-1758.9, -4070.8) * mm});
            skLineSegment(sketch, "E1377", {"start": v(-1758.9, -4070.8) * mm, "end": v(-1740.66, -4063.78) * mm});
            skLineSegment(sketch, "E1378", {"start": v(-1740.66, -4063.78) * mm, "end": v(-1722.27, -4057.21) * mm});
            skLineSegment(sketch, "E1379", {"start": v(-1722.27, -4057.21) * mm, "end": v(-1703.71, -4051.15) * mm});
            skLineSegment(sketch, "E1380", {"start": v(-1703.71, -4051.15) * mm, "end": v(-1685, -4045.62) * mm});
            skLineSegment(sketch, "E1381", {"start": v(-1685, -4045.62) * mm, "end": v(-1666.13, -4040.64) * mm});
            skLineSegment(sketch, "E1382", {"start": v(-1666.13, -4040.64) * mm, "end": v(-1647.12, -4036.24) * mm});
            skLineSegment(sketch, "E1383", {"start": v(-1647.12, -4036.24) * mm, "end": v(-1628, -4032.43) * mm});
            skLineSegment(sketch, "E1384", {"start": v(-1628, -4032.43) * mm, "end": v(-1608.76, -4029.23) * mm});
            skLineSegment(sketch, "E1385", {"start": v(-1608.76, -4029.23) * mm, "end": v(-1589.44, -4026.64) * mm});
            skLineSegment(sketch, "E1386", {"start": v(-1589.44, -4026.64) * mm, "end": v(-1570.04, -4024.68) * mm});
            skLineSegment(sketch, "E1387", {"start": v(-1570.04, -4024.68) * mm, "end": v(-1550.6, -4023.35) * mm});
            skLineSegment(sketch, "E1388", {"start": v(-1550.6, -4023.35) * mm, "end": v(-1531.12, -4022.65) * mm});
            skLineSegment(sketch, "E1389", {"start": v(-1531.12, -4022.65) * mm, "end": v(-1511.63, -4022.59) * mm});
            skLineSegment(sketch, "E1390", {"start": v(-1511.63, -4022.59) * mm, "end": v(-1492.14, -4023.16) * mm});
            skLineSegment(sketch, "E1391", {"start": v(-1492.14, -4023.16) * mm, "end": v(-1472.69, -4024.36) * mm});
            skLineSegment(sketch, "E1392", {"start": v(-1472.69, -4024.36) * mm, "end": v(-1453.28, -4026.2) * mm});
            skLineSegment(sketch, "E1393", {"start": v(-1453.28, -4026.2) * mm, "end": v(-1433.94, -4028.66) * mm});
            skLineSegment(sketch, "E1394", {"start": v(-1433.94, -4028.66) * mm, "end": v(-1414.69, -4031.73) * mm});
            skLineSegment(sketch, "E1395", {"start": v(-1414.69, -4031.73) * mm, "end": v(-1395.54, -4035.43) * mm});
            skLineSegment(sketch, "E1396", {"start": v(-1395.54, -4035.43) * mm, "end": v(-1376.35, -4039.74) * mm});
            skLineSegment(sketch, "E1397", {"start": v(-1376.35, -4039.74) * mm, "end": v(-1357.23, -4044.66) * mm});
            skLineSegment(sketch, "E1398", {"start": v(-1357.23, -4044.66) * mm, "end": v(-1338.26, -4050.15) * mm});
            skLineSegment(sketch, "E1399", {"start": v(-1338.26, -4050.15) * mm, "end": v(-1319.46, -4056.19) * mm});
            skLineSegment(sketch, "E1400", {"start": v(-1319.46, -4056.19) * mm, "end": v(-1300.82, -4062.74) * mm});
            skLineSegment(sketch, "E1401", {"start": v(-1300.82, -4062.74) * mm, "end": v(-1282.35, -4069.77) * mm});
            skLineSegment(sketch, "E1402", {"start": v(-1282.35, -4069.77) * mm, "end": v(-1264.04, -4077.23) * mm});
            skLineSegment(sketch, "E1403", {"start": v(-1264.04, -4077.23) * mm, "end": v(-1245.88, -4085.06) * mm});
            skLineSegment(sketch, "E1404", {"start": v(-1245.88, -4085.06) * mm, "end": v(-1228.23, -4093.02) * mm});
            skLineSegment(sketch, "E1405", {"start": v(-1228.23, -4093.02) * mm, "end": v(-1209.27, -4101.72) * mm});
            skLineSegment(sketch, "E1406", {"start": v(-1209.27, -4101.72) * mm, "end": v(-1190.72, -4110.28) * mm});
            skLineSegment(sketch, "E1407", {"start": v(-1190.72, -4110.28) * mm, "end": v(-1156.5, -4018.35) * mm});
            skLineSegment(sketch, "E1408", {"start": v(-1156.5, -4018.35) * mm, "end": v(-1119.11, -3924.5) * mm});
            skLineSegment(sketch, "E1409", {"start": v(-1119.11, -3924.5) * mm, "end": v(-1078.35, -3828.9) * mm});
            skLineSegment(sketch, "E1410", {"start": v(-1078.35, -3828.9) * mm, "end": v(-1034.32, -3731.8) * mm});
            skLineSegment(sketch, "E1411", {"start": v(-1034.32, -3731.8) * mm, "end": v(-987.34, -3633.38) * mm});
            skLineSegment(sketch, "E1412", {"start": v(-987.34, -3633.38) * mm, "end": v(-940.5, -3539.81) * mm});
            skLineSegment(sketch, "E1413", {"start": v(-940.5, -3539.81) * mm, "end": v(-892.35, -3446.87) * mm});
            skLineSegment(sketch, "E1414", {"start": v(-892.35, -3446.87) * mm, "end": v(-843.13, -3354.42) * mm});
            skLineSegment(sketch, "E1415", {"start": v(-843.13, -3354.42) * mm, "end": v(-793.05, -3262.35) * mm});
            skLineSegment(sketch, "E1416", {"start": v(-793.05, -3262.35) * mm, "end": v(-742.3, -3170.56) * mm});
            skLineSegment(sketch, "E1417", {"start": v(-742.3, -3170.56) * mm, "end": v(-688.5, -3074.64) * mm});
            skLineSegment(sketch, "E1418", {"start": v(-688.5, -3074.64) * mm, "end": v(-635.93, -2981.53) * mm});
            skLineSegment(sketch, "E1419", {"start": v(-635.93, -2981.53) * mm, "end": v(-583.68, -2889.4) * mm});
            skLineSegment(sketch, "E1420", {"start": v(-583.68, -2889.4) * mm, "end": v(-532.06, -2798.53) * mm});
            skLineSegment(sketch, "E1421", {"start": v(-532.06, -2798.53) * mm, "end": v(-481.18, -2708.9) * mm});
            skLineSegment(sketch, "E1422", {"start": v(-481.18, -2708.9) * mm, "end": v(-429.69, -2618.05) * mm});
            skLineSegment(sketch, "E1423", {"start": v(-429.69, -2618.05) * mm, "end": v(-380.17, -2530.44) * mm});
            skLineSegment(sketch, "E1424", {"start": v(-380.17, -2530.44) * mm, "end": v(-329.72, -2440.97) * mm});
            skLineSegment(sketch, "E1425", {"start": v(-329.72, -2440.97) * mm, "end": v(-278.54, -2349.88) * mm});
            skLineSegment(sketch, "E1426", {"start": v(-278.54, -2349.88) * mm, "end": v(-226.89, -2257.42) * mm});
            skLineSegment(sketch, "E1427", {"start": v(-226.89, -2257.42) * mm, "end": v(-175.02, -2163.9) * mm});
            skLineSegment(sketch, "E1428", {"start": v(-175.02, -2163.9) * mm, "end": v(-123.2, -2069.64) * mm});
            skLineSegment(sketch, "E1429", {"start": v(-123.2, -2069.64) * mm, "end": v(-71.67, -1975.03) * mm});
            skLineSegment(sketch, "E1430", {"start": v(-71.67, -1975.03) * mm, "end": v(-20.68, -1880.43) * mm});
            skLineSegment(sketch, "E1431", {"start": v(-20.68, -1880.43) * mm, "end": v(29.47, -1786.38) * mm});
            skLineSegment(sketch, "E1432", {"start": v(29.47, -1786.38) * mm, "end": v(79.64, -1691.2) * mm});
            skLineSegment(sketch, "E1433", {"start": v(79.64, -1691.2) * mm, "end": v(128.58, -1597.4) * mm});
            skLineSegment(sketch, "E1434", {"start": v(128.58, -1597.4) * mm, "end": v(176.23, -1505.2) * mm});
            skLineSegment(sketch, "E1435", {"start": v(176.23, -1505.2) * mm, "end": v(223.95, -1412.2) * mm});
            skLineSegment(sketch, "E1436", {"start": v(223.95, -1412.2) * mm, "end": v(128.43, -1362.8) * mm});
            skArc(sketch, "E1437", {"start": v(691.54, 13103.73) * mm, "mid": v(-7537.97, 7931.53) * mm, "end": v(691.54, 2759.33) * mm});
            skLineSegment(sketch, "E1438", {"start": v(691.54, 2759.33) * mm, "end": v(781.65, 2802.7) * mm});
            skLineSegment(sketch, "E1439", {"start": v(781.65, 2802.7) * mm, "end": v(738.28, 2892.8) * mm});
            skLineSegment(sketch, "E1440", {"start": v(738.28, 2892.8) * mm, "end": v(-1534.28, 7614.47) * mm});
            skLineSegment(sketch, "E1441", {"start": v(-1534.28, 7614.47) * mm, "end": v(-1577.65, 7704.58) * mm});
            skLineSegment(sketch, "E1442", {"start": v(-1577.65, 7704.58) * mm, "end": v(-1667.76, 7661.2) * mm});
            skArc(sketch, "E1443", {"start": v(-1667.76, 7661.2) * mm, "mid": v(-2097.86, 7931.53) * mm, "end": v(-1667.76, 8201.85) * mm});
            skLineSegment(sketch, "E1444", {"start": v(-1667.76, 8201.85) * mm, "end": v(-1577.65, 8158.48) * mm});
            skLineSegment(sketch, "E1445", {"start": v(-1577.65, 8158.48) * mm, "end": v(-1534.28, 8248.58) * mm});
            skLineSegment(sketch, "E1446", {"start": v(-1534.28, 8248.58) * mm, "end": v(738.28, 12970.25) * mm});
            skLineSegment(sketch, "E1447", {"start": v(738.28, 12970.25) * mm, "end": v(781.65, 13060.36) * mm});
            skLineSegment(sketch, "E1448", {"start": v(781.65, 13060.36) * mm, "end": v(691.54, 13103.73) * mm});
            skArc(sketch, "E1449", {"start": v(648.17, 13013.62) * mm, "mid": v(-7437.97, 7931.53) * mm, "end": v(648.17, 2849.43) * mm});
            skLineSegment(sketch, "E1450", {"start": v(648.17, 2849.43) * mm, "end": v(-1624.4, 7571.1) * mm});
            skArc(sketch, "E1451", {"start": v(-1624.4, 7571.1) * mm, "mid": v(-2197.86, 7931.53) * mm, "end": v(-1624.4, 8291.95) * mm});
            skLineSegment(sketch, "E1452", {"start": v(-1624.4, 8291.95) * mm, "end": v(648.17, 13013.62) * mm});
            skLineSegment(sketch, "E1453", {"start": v(-6306.25, 12525.27) * mm, "end": v(-5382.84, 12830) * mm});
            skLineSegment(sketch, "E1454", {"start": v(-5382.84, 12830) * mm, "end": v(-5287.88, 12861.34) * mm});
            skLineSegment(sketch, "E1455", {"start": v(-5287.88, 12861.34) * mm, "end": v(-5319.22, 12956.3) * mm});
            skArc(sketch, "E1456", {"start": v(-5319.22, 12956.3) * mm, "mid": v(-7161.18, 13411.66) * mm, "end": v(-6772.65, 11554.45) * mm});
            skLineSegment(sketch, "E1457", {"start": v(-6772.65, 11554.45) * mm, "end": v(-6678.88, 11519.7) * mm});
            skLineSegment(sketch, "E1458", {"start": v(-6678.88, 11519.7) * mm, "end": v(-6644.13, 11613.47) * mm});
            skLineSegment(sketch, "E1459", {"start": v(-6644.13, 11613.47) * mm, "end": v(-6306.25, 12525.27) * mm});
            skLineSegment(sketch, "E1460", {"start": v(-6383.3, 12605.15) * mm, "end": v(-5414.18, 12924.97) * mm});
            skArc(sketch, "E1461", {"start": v(-5414.18, 12924.97) * mm, "mid": v(-7091.76, 13339.68) * mm, "end": v(-6737.9, 11648.22) * mm});
            skLineSegment(sketch, "E1462", {"start": v(-6737.9, 11648.22) * mm, "end": v(-6383.3, 12605.15) * mm});
            skSolve(sketch);
        }
        {
            var Q0;
            Q0=sQuery(id+"F0.wireOp",EDGE,"E183");
            var Q1;
            Q1=sQuery(id+"F0.wireOp",EDGE,"E184");
            revolve(context, id + "F1", {"bodyType" : ToolBodyType.SURFACE, "surfaceEntities" : qUnion([Q0]), "axis" : qUnion([Q1]), "revolveType" : RevolveType.FULL});
        }
        {
            var Q0;
            Q0=sQuery(id+"F0.wireOp",EDGE,"E186");
            var Q1;
            Q1=sQuery(id+"F0.wireOp",EDGE,"E187");
            var Q2;
            Q2=sQuery(id+"F0.wireOp",EDGE,"E188");
            var Q3;
            Q3=sQuery(id+"F0.wireOp",EDGE,"E189");
            var Q4;
            Q4=sQuery(id+"F0.wireOp",EDGE,"E190");
            var Q5;
            Q5=sQuery(id+"F0.wireOp",EDGE,"E191");
            var Q6;
            Q6=sQuery(id+"F0.wireOp",EDGE,"E192");
            var Q7;
            Q7=sQuery(id+"F0.wireOp",EDGE,"E193");
            var Q8;
            Q8=sQuery(id+"F0.wireOp",EDGE,"E194");
            var Q9;
            Q9=sQuery(id+"F0.wireOp",EDGE,"E195");
            var Q10;
            Q10=sQuery(id+"F0.wireOp",EDGE,"E196");
            var Q11;
            Q11=sQuery(id+"F0.wireOp",EDGE,"E197");
            var Q12;
            Q12=sQuery(id+"F0.wireOp",EDGE,"E198");
            var Q13;
            Q13=sQuery(id+"F0.wireOp",EDGE,"E199");
            var Q14;
            Q14=sQuery(id+"F0.wireOp",EDGE,"E200");
            var Q15;
            Q15=sQuery(id+"F0.wireOp",EDGE,"E201");
            var Q16;
            Q16=sQuery(id+"F0.wireOp",EDGE,"E202");
            var Q17;
            Q17=sQuery(id+"F0.wireOp",EDGE,"E203");
            var Q18;
            Q18=sQuery(id+"F0.wireOp",EDGE,"E204");
            var Q19;
            Q19=sQuery(id+"F0.wireOp",EDGE,"E205");
            var Q20;
            Q20=sQuery(id+"F0.wireOp",EDGE,"E206");
            var Q21;
            Q21=sQuery(id+"F0.wireOp",EDGE,"E207");
            var Q22;
            Q22=sQuery(id+"F0.wireOp",EDGE,"E208");
            var Q23;
            Q23=sQuery(id+"F0.wireOp",EDGE,"E209");
            var Q24;
            Q24=sQuery(id+"F0.wireOp",EDGE,"E210");
            var Q25;
            Q25=sQuery(id+"F0.wireOp",EDGE,"E211");
            var Q26;
            Q26=sQuery(id+"F0.wireOp",EDGE,"E212");
            var Q27;
            Q27=sQuery(id+"F0.wireOp",EDGE,"E213");
            var Q28;
            Q28=sQuery(id+"F0.wireOp",EDGE,"E214");
            var Q29;
            Q29=sQuery(id+"F0.wireOp",EDGE,"E215");
            var Q30;
            Q30=sQuery(id+"F0.wireOp",EDGE,"E216");
            var Q31;
            Q31=sQuery(id+"F0.wireOp",EDGE,"E217");
            var Q32;
            Q32=sQuery(id+"F0.wireOp",EDGE,"E218");
            var Q33;
            Q33=sQuery(id+"F0.wireOp",EDGE,"E219");
            var Q34;
            Q34=sQuery(id+"F0.wireOp",EDGE,"E220");
            var Q35;
            Q35=sQuery(id+"F0.wireOp",EDGE,"E221");
            var Q36;
            Q36=sQuery(id+"F0.wireOp",EDGE,"E222");
            var Q37;
            Q37=sQuery(id+"F0.wireOp",EDGE,"E223");
            var Q38;
            Q38=sQuery(id+"F0.wireOp",EDGE,"E224");
            var Q39;
            Q39=sQuery(id+"F0.wireOp",EDGE,"E225");
            var Q40;
            Q40=sQuery(id+"F0.wireOp",EDGE,"E226");
            var Q41;
            Q41=sQuery(id+"F0.wireOp",EDGE,"E227");
            var Q42;
            Q42=sQuery(id+"F0.wireOp",EDGE,"E228");
            var Q43;
            Q43=sQuery(id+"F0.wireOp",EDGE,"E229");
            var Q44;
            Q44=sQuery(id+"F0.wireOp",EDGE,"E230");
            var Q45;
            Q45=sQuery(id+"F0.wireOp",EDGE,"E231");
            var Q46;
            Q46=sQuery(id+"F0.wireOp",EDGE,"E232");
            var Q47;
            Q47=sQuery(id+"F0.wireOp",EDGE,"E233");
            var Q48;
            Q48=sQuery(id+"F0.wireOp",EDGE,"E234");
            var Q49;
            Q49=sQuery(id+"F0.wireOp",EDGE,"E235");
            var Q50;
            Q50=sQuery(id+"F0.wireOp",EDGE,"E236");
            var Q51;
            Q51=sQuery(id+"F0.wireOp",EDGE,"E237");
            var Q52;
            Q52=sQuery(id+"F0.wireOp",EDGE,"E238");
            var Q53;
            Q53=sQuery(id+"F0.wireOp",EDGE,"E239");
            var Q54;
            Q54=sQuery(id+"F0.wireOp",EDGE,"E240");
            var Q55;
            Q55=sQuery(id+"F0.wireOp",EDGE,"E241");
            var Q56;
            Q56=sQuery(id+"F0.wireOp",EDGE,"E242");
            var Q57;
            Q57=sQuery(id+"F0.wireOp",EDGE,"E243");
            var Q58;
            Q58=sQuery(id+"F0.wireOp",EDGE,"E244");
            var Q59;
            Q59=sQuery(id+"F0.wireOp",EDGE,"E245");
            var Q60;
            Q60=sQuery(id+"F0.wireOp",EDGE,"E246");
            var Q61;
            Q61=sQuery(id+"F0.wireOp",EDGE,"E247");
            var Q62;
            Q62=sQuery(id+"F0.wireOp",EDGE,"E248");
            var Q63;
            Q63=sQuery(id+"F0.wireOp",EDGE,"E249");
            var Q64;
            Q64=sQuery(id+"F0.wireOp",EDGE,"E250");
            var Q65;
            Q65=sQuery(id+"F0.wireOp",EDGE,"E184");
            revolve(context, id + "F2", {"bodyType" : ToolBodyType.SURFACE, "surfaceEntities" : qUnion([Q0, Q1, Q2, Q3, Q4, Q5, Q6, Q7, Q8, Q9, Q10, Q11, Q12, Q13, Q14, Q15, Q16, Q17, Q18, Q19, Q20, Q21, Q22, Q23, Q24, Q25, Q26, Q27, Q28, Q29, Q30, Q31, Q32, Q33, Q34, Q35, Q36, Q37, Q38, Q39, Q40, Q41, Q42, Q43, Q44, Q45, Q46, Q47, Q48, Q49, Q50, Q51, Q52, Q53, Q54, Q55, Q56, Q57, Q58, Q59, Q60, Q61, Q62, Q63, Q64]), "axis" : qUnion([Q65]), "revolveType" : RevolveType.FULL});
        }
        {
            var Q0;
            Q0=sQuery(id+"F0.wireOp",EDGE,"E255");
            var Q1;
            Q1=sQuery(id+"F0.wireOp",EDGE,"E256");
            var Q2;
            Q2=sQuery(id+"F0.wireOp",EDGE,"E257");
            var Q3;
            Q3=sQuery(id+"F0.wireOp",EDGE,"E258");
            var Q4;
            Q4=sQuery(id+"F0.wireOp",EDGE,"E259");
            var Q5;
            Q5=sQuery(id+"F0.wireOp",EDGE,"E260");
            var Q6;
            Q6=sQuery(id+"F0.wireOp",EDGE,"E261");
            var Q7;
            Q7=sQuery(id+"F0.wireOp",EDGE,"E262");
            var Q8;
            Q8=sQuery(id+"F0.wireOp",EDGE,"E263");
            var Q9;
            Q9=sQuery(id+"F0.wireOp",EDGE,"E269");
            var Q10;
            Q10=sQuery(id+"F0.wireOp",EDGE,"E271");
            var Q11;
            Q11=sQuery(id+"F0.wireOp",EDGE,"E264");
            var Q12;
            Q12=sQuery(id+"F0.wireOp",EDGE,"E266");
            var Q13;
            Q13=sQuery(id+"F0.wireOp",EDGE,"E267");
            var Q14;
            Q14=sQuery(id+"F0.wireOp",EDGE,"E270");
            var Q15;
            Q15=sQuery(id+"F0.wireOp",EDGE,"E272");
            var Q16;
            Q16=sQuery(id+"F0.wireOp",EDGE,"E273");
            var Q17;
            Q17=sQuery(id+"F0.wireOp",EDGE,"E274");
            var Q18;
            Q18=sQuery(id+"F0.wireOp",EDGE,"E275");
            var Q19;
            Q19=sQuery(id+"F0.wireOp",EDGE,"E276");
            var Q20;
            Q20=sQuery(id+"F0.wireOp",EDGE,"E277");
            var Q21;
            Q21=sQuery(id+"F0.wireOp",EDGE,"E278");
            var Q22;
            Q22=sQuery(id+"F0.wireOp",EDGE,"E279");
            var Q23;
            Q23=sQuery(id+"F0.wireOp",EDGE,"E265");
            var Q24;
            Q24=sQuery(id+"F0.wireOp",EDGE,"E268");
            var Q25;
            Q25=sQuery(id+"F0.wireOp",EDGE,"E285");
            var Q26;
            Q26=sQuery(id+"F0.wireOp",EDGE,"E287");
            var Q27;
            Q27=sQuery(id+"F0.wireOp",EDGE,"E290");
            var Q28;
            Q28=sQuery(id+"F0.wireOp",EDGE,"E291");
            var Q29;
            Q29=sQuery(id+"F0.wireOp",EDGE,"E286");
            var Q30;
            Q30=sQuery(id+"F0.wireOp",EDGE,"E288");
            var Q31;
            Q31=sQuery(id+"F0.wireOp",EDGE,"E289");
            var Q32;
            Q32=sQuery(id+"F0.wireOp",EDGE,"E292");
            var Q33;
            Q33=sQuery(id+"F0.wireOp",EDGE,"E280");
            var Q34;
            Q34=sQuery(id+"F0.wireOp",EDGE,"E281");
            var Q35;
            Q35=sQuery(id+"F0.wireOp",EDGE,"E282");
            var Q36;
            Q36=sQuery(id+"F0.wireOp",EDGE,"E283");
            var Q37;
            Q37=sQuery(id+"F0.wireOp",EDGE,"E284");
            var Q38;
            Q38=sQuery(id+"F0.wireOp",EDGE,"E301");
            var Q39;
            Q39=sQuery(id+"F0.wireOp",EDGE,"E302");
            var Q40;
            Q40=sQuery(id+"F0.wireOp",EDGE,"E303");
            var Q41;
            Q41=sQuery(id+"F0.wireOp",EDGE,"E304");
            var Q42;
            Q42=sQuery(id+"F0.wireOp",EDGE,"E305");
            var Q43;
            Q43=sQuery(id+"F0.wireOp",EDGE,"E306");
            var Q44;
            Q44=sQuery(id+"F0.wireOp",EDGE,"E307");
            var Q45;
            Q45=sQuery(id+"F0.wireOp",EDGE,"E308");
            var Q46;
            Q46=sQuery(id+"F0.wireOp",EDGE,"E309");
            var Q47;
            Q47=sQuery(id+"F0.wireOp",EDGE,"E293");
            var Q48;
            Q48=sQuery(id+"F0.wireOp",EDGE,"E310");
            var Q49;
            Q49=sQuery(id+"F0.wireOp",EDGE,"E294");
            var Q50;
            Q50=sQuery(id+"F0.wireOp",EDGE,"E295");
            var Q51;
            Q51=sQuery(id+"F0.wireOp",EDGE,"E311");
            var Q52;
            Q52=sQuery(id+"F0.wireOp",EDGE,"E296");
            var Q53;
            Q53=sQuery(id+"F0.wireOp",EDGE,"E312");
            var Q54;
            Q54=sQuery(id+"F0.wireOp",EDGE,"E297");
            var Q55;
            Q55=sQuery(id+"F0.wireOp",EDGE,"E313");
            var Q56;
            Q56=sQuery(id+"F0.wireOp",EDGE,"E298");
            var Q57;
            Q57=sQuery(id+"F0.wireOp",EDGE,"E299");
            var Q58;
            Q58=sQuery(id+"F0.wireOp",EDGE,"E300");
            var Q59;
            Q59=sQuery(id+"F0.wireOp",EDGE,"E315");
            var Q60;
            Q60=sQuery(id+"F0.wireOp",EDGE,"E314");
            var Q61;
            Q61=sQuery(id+"F0.wireOp",EDGE,"E254");
            var Q62;
            Q62=sQuery(id+"F0.wireOp",EDGE,"E253");
            var Q63;
            Q63=sQuery(id+"F0.wireOp",EDGE,"E184");
            revolve(context, id + "F3", {"bodyType" : ToolBodyType.SURFACE, "surfaceEntities" : qUnion([Q0, Q1, Q2, Q3, Q4, Q5, Q6, Q7, Q8, Q9, Q10, Q11, Q12, Q13, Q14, Q15, Q16, Q17, Q18, Q19, Q20, Q21, Q22, Q23, Q24, Q25, Q26, Q27, Q28, Q29, Q30, Q31, Q32, Q33, Q34, Q35, Q36, Q37, Q38, Q39, Q40, Q41, Q42, Q43, Q44, Q45, Q46, Q47, Q48, Q49, Q50, Q51, Q52, Q53, Q54, Q55, Q56, Q57, Q58, Q59, Q60, Q61, Q62]), "axis" : qUnion([Q63]), "revolveType" : RevolveType.FULL});
        }
    });
